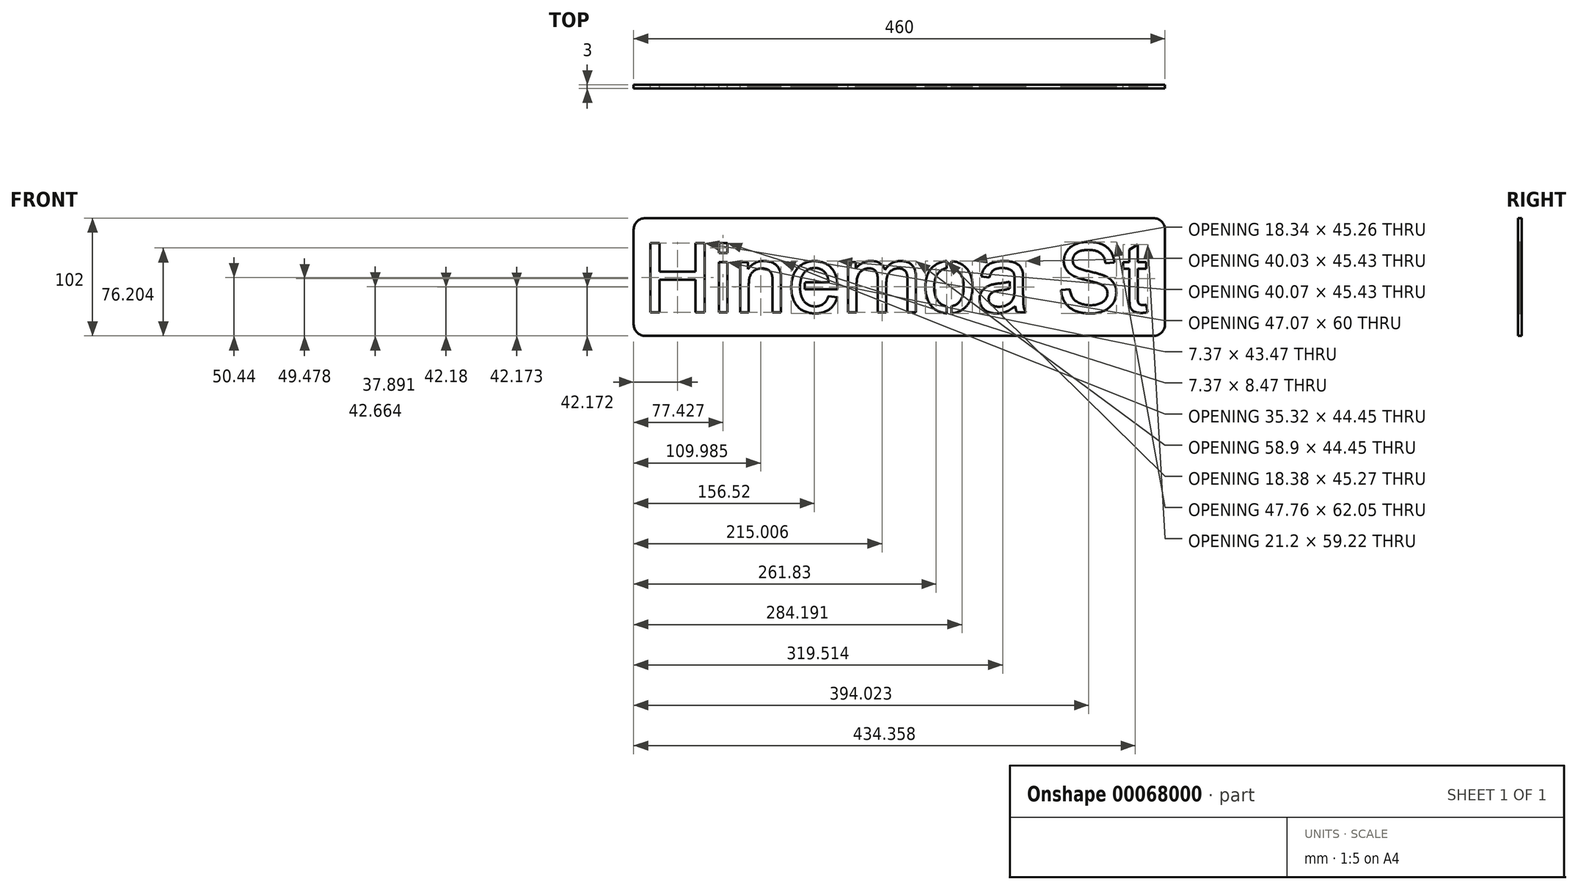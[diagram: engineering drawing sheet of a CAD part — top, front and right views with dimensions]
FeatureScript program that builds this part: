
annotation { "Feature Type Name" : "Feature", "Feature Type Description" : "" }
export const myFeature = defineFeature(function(context is Context, id is Id, definition is map)
    precondition{}
    {
        {
            var Q0;
            Q0=qCreatedBy(makeId("Front.planeOp"),FACE);
            var sketch = newSketch(context, id + "F0", { "sketchPlane" : qUnion([Q0])});
            skLineSegment(sketch, "E0", {"start": v(45.02, -25.34) * mm, "end": v(45.02, -31.45) * mm});
            skLineSegment(sketch, "E1", {"start": v(45.02, -25.34) * mm, "end": v(45.65, -25.22) * mm});
            skLineSegment(sketch, "E2", {"start": v(45.65, -25.22) * mm, "end": v(46.27, -25.08) * mm});
            skLineSegment(sketch, "E3", {"start": v(46.27, -25.08) * mm, "end": v(46.87, -24.9) * mm});
            skLineSegment(sketch, "E4", {"start": v(46.87, -24.9) * mm, "end": v(47.47, -24.69) * mm});
            skLineSegment(sketch, "E5", {"start": v(47.47, -24.69) * mm, "end": v(48.04, -24.44) * mm});
            skLineSegment(sketch, "E6", {"start": v(48.04, -24.44) * mm, "end": v(48.6, -24.16) * mm});
            skLineSegment(sketch, "E7", {"start": v(48.6, -24.16) * mm, "end": v(49.16, -23.85) * mm});
            skLineSegment(sketch, "E8", {"start": v(49.16, -23.85) * mm, "end": v(49.7, -23.51) * mm});
            skLineSegment(sketch, "E9", {"start": v(49.7, -23.51) * mm, "end": v(50.21, -23.14) * mm});
            skLineSegment(sketch, "E10", {"start": v(50.21, -23.14) * mm, "end": v(50.72, -22.73) * mm});
            skLineSegment(sketch, "E11", {"start": v(50.72, -22.73) * mm, "end": v(51.2, -22.29) * mm});
            skLineSegment(sketch, "E12", {"start": v(51.2, -22.29) * mm, "end": v(51.69, -21.82) * mm});
            skLineSegment(sketch, "E13", {"start": v(51.69, -21.82) * mm, "end": v(52.15, -21.31) * mm});
            skLineSegment(sketch, "E14", {"start": v(52.15, -21.31) * mm, "end": v(52.59, -20.77) * mm});
            skLineSegment(sketch, "E15", {"start": v(52.59, -20.77) * mm, "end": v(53, -20.2) * mm});
            skLineSegment(sketch, "E16", {"start": v(53, -20.2) * mm, "end": v(53.39, -19.6) * mm});
            skLineSegment(sketch, "E17", {"start": v(53.39, -19.6) * mm, "end": v(53.74, -18.95) * mm});
            skLineSegment(sketch, "E18", {"start": v(53.74, -18.95) * mm, "end": v(54.07, -18.27) * mm});
            skLineSegment(sketch, "E19", {"start": v(54.07, -18.27) * mm, "end": v(54.37, -17.56) * mm});
            skLineSegment(sketch, "E20", {"start": v(54.37, -17.56) * mm, "end": v(54.64, -16.82) * mm});
            skLineSegment(sketch, "E21", {"start": v(54.64, -16.82) * mm, "end": v(54.88, -16.04) * mm});
            skLineSegment(sketch, "E22", {"start": v(54.88, -16.04) * mm, "end": v(55.1, -15.23) * mm});
            skLineSegment(sketch, "E23", {"start": v(55.1, -15.23) * mm, "end": v(55.28, -14.38) * mm});
            skLineSegment(sketch, "E24", {"start": v(55.28, -14.38) * mm, "end": v(55.43, -13.5) * mm});
            skLineSegment(sketch, "E25", {"start": v(55.43, -13.5) * mm, "end": v(55.56, -12.59) * mm});
            skLineSegment(sketch, "E26", {"start": v(55.56, -12.59) * mm, "end": v(55.66, -11.64) * mm});
            skLineSegment(sketch, "E27", {"start": v(55.66, -11.64) * mm, "end": v(55.73, -10.65) * mm});
            skLineSegment(sketch, "E28", {"start": v(55.73, -10.65) * mm, "end": v(55.78, -9.63) * mm});
            skLineSegment(sketch, "E29", {"start": v(55.78, -9.63) * mm, "end": v(55.8, -8.58) * mm});
            skLineSegment(sketch, "E30", {"start": v(55.8, -8.58) * mm, "end": v(55.78, -7.59) * mm});
            skLineSegment(sketch, "E31", {"start": v(55.78, -7.59) * mm, "end": v(55.73, -6.63) * mm});
            skLineSegment(sketch, "E32", {"start": v(55.73, -6.63) * mm, "end": v(55.66, -5.7) * mm});
            skLineSegment(sketch, "E33", {"start": v(55.66, -5.7) * mm, "end": v(55.56, -4.8) * mm});
            skLineSegment(sketch, "E34", {"start": v(55.56, -4.8) * mm, "end": v(55.43, -3.92) * mm});
            skLineSegment(sketch, "E35", {"start": v(55.43, -3.92) * mm, "end": v(55.28, -3.08) * mm});
            skLineSegment(sketch, "E36", {"start": v(55.28, -3.08) * mm, "end": v(55.09, -2.28) * mm});
            skLineSegment(sketch, "E37", {"start": v(55.09, -2.28) * mm, "end": v(54.87, -1.5) * mm});
            skLineSegment(sketch, "E38", {"start": v(54.87, -1.5) * mm, "end": v(54.63, -0.75) * mm});
            skLineSegment(sketch, "E39", {"start": v(54.63, -0.75) * mm, "end": v(54.36, -0.03) * mm});
            skLineSegment(sketch, "E40", {"start": v(54.36, -0.03) * mm, "end": v(54.06, 0.66) * mm});
            skLineSegment(sketch, "E41", {"start": v(54.06, 0.66) * mm, "end": v(53.73, 1.31) * mm});
            skLineSegment(sketch, "E42", {"start": v(53.73, 1.31) * mm, "end": v(53.37, 1.94) * mm});
            skLineSegment(sketch, "E43", {"start": v(53.37, 1.94) * mm, "end": v(52.99, 2.54) * mm});
            skLineSegment(sketch, "E44", {"start": v(52.99, 2.54) * mm, "end": v(52.57, 3.1) * mm});
            skLineSegment(sketch, "E45", {"start": v(52.57, 3.1) * mm, "end": v(52.13, 3.64) * mm});
            skLineSegment(sketch, "E46", {"start": v(52.13, 3.64) * mm, "end": v(51.66, 4.14) * mm});
            skLineSegment(sketch, "E47", {"start": v(51.66, 4.14) * mm, "end": v(51.18, 4.6) * mm});
            skLineSegment(sketch, "E48", {"start": v(51.18, 4.6) * mm, "end": v(50.7, 5.05) * mm});
            skLineSegment(sketch, "E49", {"start": v(50.7, 5.05) * mm, "end": v(50.18, 5.45) * mm});
            skLineSegment(sketch, "E50", {"start": v(50.18, 5.45) * mm, "end": v(49.66, 5.83) * mm});
            skLineSegment(sketch, "E51", {"start": v(49.66, 5.83) * mm, "end": v(49.13, 6.17) * mm});
            skLineSegment(sketch, "E52", {"start": v(49.13, 6.17) * mm, "end": v(48.58, 6.47) * mm});
            skLineSegment(sketch, "E53", {"start": v(48.58, 6.47) * mm, "end": v(48.02, 6.75) * mm});
            skLineSegment(sketch, "E54", {"start": v(48.02, 6.75) * mm, "end": v(47.44, 7) * mm});
            skLineSegment(sketch, "E55", {"start": v(47.44, 7) * mm, "end": v(46.85, 7.2) * mm});
            skLineSegment(sketch, "E56", {"start": v(46.85, 7.2) * mm, "end": v(46.25, 7.38) * mm});
            skLineSegment(sketch, "E57", {"start": v(46.25, 7.38) * mm, "end": v(45.63, 7.53) * mm});
            skLineSegment(sketch, "E58", {"start": v(45.63, 7.53) * mm, "end": v(45.02, 7.64) * mm});
            skLineSegment(sketch, "E59", {"start": v(45.02, 13.8) * mm, "end": v(45.02, 7.64) * mm});
            skLineSegment(sketch, "E60", {"start": v(45.02, 13.8) * mm, "end": v(45.21, 13.8) * mm});
            skLineSegment(sketch, "E61", {"start": v(45.21, 13.8) * mm, "end": v(46.27, 13.68) * mm});
            skLineSegment(sketch, "E62", {"start": v(46.27, 13.68) * mm, "end": v(47.3, 13.52) * mm});
            skLineSegment(sketch, "E63", {"start": v(47.3, 13.52) * mm, "end": v(48.3, 13.31) * mm});
            skLineSegment(sketch, "E64", {"start": v(48.3, 13.31) * mm, "end": v(49.28, 13.06) * mm});
            skLineSegment(sketch, "E65", {"start": v(49.28, 13.06) * mm, "end": v(50.24, 12.76) * mm});
            skLineSegment(sketch, "E66", {"start": v(50.24, 12.76) * mm, "end": v(51.17, 12.42) * mm});
            skLineSegment(sketch, "E67", {"start": v(51.17, 12.42) * mm, "end": v(52.07, 12.03) * mm});
            skLineSegment(sketch, "E68", {"start": v(52.07, 12.03) * mm, "end": v(52.95, 11.6) * mm});
            skLineSegment(sketch, "E69", {"start": v(52.95, 11.6) * mm, "end": v(53.8, 11.11) * mm});
            skLineSegment(sketch, "E70", {"start": v(53.8, 11.11) * mm, "end": v(54.62, 10.58) * mm});
            skLineSegment(sketch, "E71", {"start": v(54.62, 10.58) * mm, "end": v(55.42, 10.01) * mm});
            skLineSegment(sketch, "E72", {"start": v(55.42, 10.01) * mm, "end": v(56.2, 9.4) * mm});
            skLineSegment(sketch, "E73", {"start": v(56.2, 9.4) * mm, "end": v(56.95, 8.73) * mm});
            skLineSegment(sketch, "E74", {"start": v(56.95, 8.73) * mm, "end": v(57.67, 8.01) * mm});
            skLineSegment(sketch, "E75", {"start": v(57.67, 8.01) * mm, "end": v(58.36, 7.26) * mm});
            skLineSegment(sketch, "E76", {"start": v(58.36, 7.26) * mm, "end": v(59, 6.48) * mm});
            skLineSegment(sketch, "E77", {"start": v(59, 6.48) * mm, "end": v(59.6, 5.65) * mm});
            skLineSegment(sketch, "E78", {"start": v(59.6, 5.65) * mm, "end": v(60.16, 4.8) * mm});
            skLineSegment(sketch, "E79", {"start": v(60.16, 4.8) * mm, "end": v(60.67, 3.9) * mm});
            skLineSegment(sketch, "E80", {"start": v(60.67, 3.9) * mm, "end": v(61.14, 2.98) * mm});
            skLineSegment(sketch, "E81", {"start": v(61.14, 2.98) * mm, "end": v(61.56, 2.02) * mm});
            skLineSegment(sketch, "E82", {"start": v(61.56, 2.02) * mm, "end": v(61.94, 1.02) * mm});
            skLineSegment(sketch, "E83", {"start": v(61.94, 1.02) * mm, "end": v(62.27, -0.01) * mm});
            skLineSegment(sketch, "E84", {"start": v(62.27, -0.01) * mm, "end": v(62.56, -1.08) * mm});
            skLineSegment(sketch, "E85", {"start": v(62.56, -1.08) * mm, "end": v(62.8, -2.18) * mm});
            skLineSegment(sketch, "E86", {"start": v(62.8, -2.18) * mm, "end": v(63, -3.32) * mm});
            skLineSegment(sketch, "E87", {"start": v(63, -3.32) * mm, "end": v(63.16, -4.49) * mm});
            skLineSegment(sketch, "E88", {"start": v(63.16, -4.49) * mm, "end": v(63.27, -5.7) * mm});
            skLineSegment(sketch, "E89", {"start": v(63.27, -5.7) * mm, "end": v(63.34, -6.94) * mm});
            skLineSegment(sketch, "E90", {"start": v(63.34, -6.94) * mm, "end": v(63.36, -8.21) * mm});
            skLineSegment(sketch, "E91", {"start": v(63.36, -8.21) * mm, "end": v(63.35, -9.25) * mm});
            skLineSegment(sketch, "E92", {"start": v(63.35, -9.25) * mm, "end": v(63.32, -10.26) * mm});
            skLineSegment(sketch, "E93", {"start": v(63.32, -10.26) * mm, "end": v(63.27, -11.23) * mm});
            skLineSegment(sketch, "E94", {"start": v(63.27, -11.23) * mm, "end": v(63.2, -12.18) * mm});
            skLineSegment(sketch, "E95", {"start": v(63.2, -12.18) * mm, "end": v(63.12, -13.1) * mm});
            skLineSegment(sketch, "E96", {"start": v(63.12, -13.1) * mm, "end": v(63, -14) * mm});
            skLineSegment(sketch, "E97", {"start": v(63, -14) * mm, "end": v(62.88, -14.87) * mm});
            skLineSegment(sketch, "E98", {"start": v(62.88, -14.87) * mm, "end": v(62.73, -15.7) * mm});
            skLineSegment(sketch, "E99", {"start": v(62.73, -15.7) * mm, "end": v(62.57, -16.52) * mm});
            skLineSegment(sketch, "E100", {"start": v(62.57, -16.52) * mm, "end": v(62.38, -17.3) * mm});
            skLineSegment(sketch, "E101", {"start": v(62.38, -17.3) * mm, "end": v(62.17, -18.06) * mm});
            skLineSegment(sketch, "E102", {"start": v(62.17, -18.06) * mm, "end": v(61.95, -18.78) * mm});
            skLineSegment(sketch, "E103", {"start": v(61.95, -18.78) * mm, "end": v(61.7, -19.48) * mm});
            skLineSegment(sketch, "E104", {"start": v(61.7, -19.48) * mm, "end": v(61.43, -20.15) * mm});
            skLineSegment(sketch, "E105", {"start": v(61.43, -20.15) * mm, "end": v(61.15, -20.8) * mm});
            skLineSegment(sketch, "E106", {"start": v(61.15, -20.8) * mm, "end": v(60.84, -21.41) * mm});
            skLineSegment(sketch, "E107", {"start": v(60.84, -21.41) * mm, "end": v(60.52, -22) * mm});
            skLineSegment(sketch, "E108", {"start": v(60.52, -22) * mm, "end": v(60.18, -22.58) * mm});
            skLineSegment(sketch, "E109", {"start": v(60.18, -22.58) * mm, "end": v(59.82, -23.14) * mm});
            skLineSegment(sketch, "E110", {"start": v(59.82, -23.14) * mm, "end": v(59.44, -23.68) * mm});
            skLineSegment(sketch, "E111", {"start": v(59.44, -23.68) * mm, "end": v(59.05, -24.2) * mm});
            skLineSegment(sketch, "E112", {"start": v(59.05, -24.2) * mm, "end": v(58.63, -24.72) * mm});
            skLineSegment(sketch, "E113", {"start": v(58.63, -24.72) * mm, "end": v(58.2, -25.2) * mm});
            skLineSegment(sketch, "E114", {"start": v(58.2, -25.2) * mm, "end": v(57.75, -25.68) * mm});
            skLineSegment(sketch, "E115", {"start": v(57.75, -25.68) * mm, "end": v(57.29, -26.14) * mm});
            skLineSegment(sketch, "E116", {"start": v(57.29, -26.14) * mm, "end": v(56.8, -26.58) * mm});
            skLineSegment(sketch, "E117", {"start": v(56.8, -26.58) * mm, "end": v(56.3, -27) * mm});
            skLineSegment(sketch, "E118", {"start": v(56.3, -27) * mm, "end": v(55.78, -27.42) * mm});
            skLineSegment(sketch, "E119", {"start": v(55.78, -27.42) * mm, "end": v(55.24, -27.8) * mm});
            skLineSegment(sketch, "E120", {"start": v(55.24, -27.8) * mm, "end": v(54.69, -28.18) * mm});
            skLineSegment(sketch, "E121", {"start": v(54.69, -28.18) * mm, "end": v(54.11, -28.54) * mm});
            skLineSegment(sketch, "E122", {"start": v(54.11, -28.54) * mm, "end": v(53.52, -28.88) * mm});
            skLineSegment(sketch, "E123", {"start": v(53.52, -28.88) * mm, "end": v(52.3, -29.5) * mm});
            skLineSegment(sketch, "E124", {"start": v(52.3, -29.5) * mm, "end": v(51.06, -30.05) * mm});
            skLineSegment(sketch, "E125", {"start": v(51.06, -30.05) * mm, "end": v(49.79, -30.5) * mm});
            skLineSegment(sketch, "E126", {"start": v(49.79, -30.5) * mm, "end": v(48.49, -30.88) * mm});
            skLineSegment(sketch, "E127", {"start": v(48.49, -30.88) * mm, "end": v(47.16, -31.17) * mm});
            skLineSegment(sketch, "E128", {"start": v(47.16, -31.17) * mm, "end": v(45.81, -31.38) * mm});
            skLineSegment(sketch, "E129", {"start": v(45.81, -31.38) * mm, "end": v(45.02, -31.45) * mm});
            skLineSegment(sketch, "E130", {"start": v(-230, -41) * mm, "end": v(-230, 41) * mm});
            skArc(sketch, "E131", {"start": v(-220, -51) * mm, "mid": v(-227.07, -48.07) * mm, "end": v(-230, -41) * mm});
            skLineSegment(sketch, "E132", {"start": v(220, -51) * mm, "end": v(-220, -51) * mm});
            skArc(sketch, "E133", {"start": v(230, -41) * mm, "mid": v(227.07, -48.07) * mm, "end": v(220, -51) * mm});
            skLineSegment(sketch, "E134", {"start": v(230, 41) * mm, "end": v(230, -41) * mm});
            skArc(sketch, "E135", {"start": v(220, 51) * mm, "mid": v(227.07, 48.07) * mm, "end": v(230, 41) * mm});
            skLineSegment(sketch, "E136", {"start": v(-220, 51) * mm, "end": v(220, 51) * mm});
            skArc(sketch, "E137", {"start": v(-230, 41) * mm, "mid": v(-227.07, 48.07) * mm, "end": v(-220, 51) * mm});
            skLineSegment(sketch, "E138", {"start": v(95.75, -10.01) * mm, "end": v(95.75, -4.06) * mm});
            skLineSegment(sketch, "E139", {"start": v(95.75, -10.01) * mm, "end": v(95.47, -10.08) * mm});
            skLineSegment(sketch, "E140", {"start": v(95.47, -10.08) * mm, "end": v(94.73, -10.26) * mm});
            skLineSegment(sketch, "E141", {"start": v(94.73, -10.26) * mm, "end": v(93.97, -10.43) * mm});
            skLineSegment(sketch, "E142", {"start": v(93.97, -10.43) * mm, "end": v(93.17, -10.6) * mm});
            skLineSegment(sketch, "E143", {"start": v(93.17, -10.6) * mm, "end": v(92.34, -10.76) * mm});
            skLineSegment(sketch, "E144", {"start": v(92.34, -10.76) * mm, "end": v(91.47, -10.92) * mm});
            skLineSegment(sketch, "E145", {"start": v(91.47, -10.92) * mm, "end": v(90.58, -11.08) * mm});
            skLineSegment(sketch, "E146", {"start": v(90.58, -11.08) * mm, "end": v(89.66, -11.23) * mm});
            skLineSegment(sketch, "E147", {"start": v(89.66, -11.23) * mm, "end": v(88.7, -11.38) * mm});
            skLineSegment(sketch, "E148", {"start": v(88.7, -11.38) * mm, "end": v(87.71, -11.53) * mm});
            skLineSegment(sketch, "E149", {"start": v(87.71, -11.53) * mm, "end": v(86.62, -11.7) * mm});
            skLineSegment(sketch, "E150", {"start": v(86.62, -11.7) * mm, "end": v(85.6, -11.87) * mm});
            skLineSegment(sketch, "E151", {"start": v(85.6, -11.87) * mm, "end": v(84.68, -12.04) * mm});
            skLineSegment(sketch, "E152", {"start": v(84.68, -12.04) * mm, "end": v(83.84, -12.22) * mm});
            skLineSegment(sketch, "E153", {"start": v(83.84, -12.22) * mm, "end": v(83.07, -12.41) * mm});
            skLineSegment(sketch, "E154", {"start": v(83.07, -12.41) * mm, "end": v(82.4, -12.6) * mm});
            skLineSegment(sketch, "E155", {"start": v(82.4, -12.6) * mm, "end": v(81.8, -12.8) * mm});
            skLineSegment(sketch, "E156", {"start": v(81.8, -12.8) * mm, "end": v(81.29, -13) * mm});
            skLineSegment(sketch, "E157", {"start": v(81.29, -13) * mm, "end": v(80.83, -13.22) * mm});
            skLineSegment(sketch, "E158", {"start": v(80.83, -13.22) * mm, "end": v(80.4, -13.46) * mm});
            skLineSegment(sketch, "E159", {"start": v(80.4, -13.46) * mm, "end": v(80, -13.72) * mm});
            skLineSegment(sketch, "E160", {"start": v(80, -13.72) * mm, "end": v(79.62, -14) * mm});
            skLineSegment(sketch, "E161", {"start": v(79.62, -14) * mm, "end": v(79.27, -14.32) * mm});
            skLineSegment(sketch, "E162", {"start": v(79.27, -14.32) * mm, "end": v(78.95, -14.66) * mm});
            skLineSegment(sketch, "E163", {"start": v(78.95, -14.66) * mm, "end": v(78.65, -15.01) * mm});
            skLineSegment(sketch, "E164", {"start": v(78.65, -15.01) * mm, "end": v(78.38, -15.4) * mm});
            skLineSegment(sketch, "E165", {"start": v(78.38, -15.4) * mm, "end": v(78.14, -15.8) * mm});
            skLineSegment(sketch, "E166", {"start": v(78.14, -15.8) * mm, "end": v(77.93, -16.2) * mm});
            skLineSegment(sketch, "E167", {"start": v(77.93, -16.2) * mm, "end": v(77.76, -16.63) * mm});
            skLineSegment(sketch, "E168", {"start": v(77.76, -16.63) * mm, "end": v(77.61, -17.06) * mm});
            skLineSegment(sketch, "E169", {"start": v(77.61, -17.06) * mm, "end": v(77.5, -17.5) * mm});
            skLineSegment(sketch, "E170", {"start": v(77.5, -17.5) * mm, "end": v(77.42, -17.96) * mm});
            skLineSegment(sketch, "E171", {"start": v(77.42, -17.96) * mm, "end": v(77.38, -18.42) * mm});
            skLineSegment(sketch, "E172", {"start": v(77.38, -18.42) * mm, "end": v(77.36, -18.9) * mm});
            skLineSegment(sketch, "E173", {"start": v(77.36, -18.9) * mm, "end": v(77.4, -19.62) * mm});
            skLineSegment(sketch, "E174", {"start": v(77.4, -19.62) * mm, "end": v(77.5, -20.3) * mm});
            skLineSegment(sketch, "E175", {"start": v(77.5, -20.3) * mm, "end": v(77.67, -20.97) * mm});
            skLineSegment(sketch, "E176", {"start": v(77.67, -20.97) * mm, "end": v(77.92, -21.6) * mm});
            skLineSegment(sketch, "E177", {"start": v(77.92, -21.6) * mm, "end": v(78.23, -22.2) * mm});
            skLineSegment(sketch, "E178", {"start": v(78.23, -22.2) * mm, "end": v(78.61, -22.76) * mm});
            skLineSegment(sketch, "E179", {"start": v(78.61, -22.76) * mm, "end": v(79.07, -23.3) * mm});
            skLineSegment(sketch, "E180", {"start": v(79.07, -23.3) * mm, "end": v(79.59, -23.8) * mm});
            skLineSegment(sketch, "E181", {"start": v(79.59, -23.8) * mm, "end": v(80.18, -24.27) * mm});
            skLineSegment(sketch, "E182", {"start": v(80.18, -24.27) * mm, "end": v(80.83, -24.67) * mm});
            skLineSegment(sketch, "E183", {"start": v(80.83, -24.67) * mm, "end": v(81.55, -25) * mm});
            skLineSegment(sketch, "E184", {"start": v(81.55, -25) * mm, "end": v(82.34, -25.28) * mm});
            skLineSegment(sketch, "E185", {"start": v(82.34, -25.28) * mm, "end": v(83.19, -25.5) * mm});
            skLineSegment(sketch, "E186", {"start": v(83.19, -25.5) * mm, "end": v(84.1, -25.65) * mm});
            skLineSegment(sketch, "E187", {"start": v(84.1, -25.65) * mm, "end": v(85.08, -25.74) * mm});
            skLineSegment(sketch, "E188", {"start": v(85.08, -25.74) * mm, "end": v(86.12, -25.77) * mm});
            skLineSegment(sketch, "E189", {"start": v(86.12, -25.77) * mm, "end": v(87.17, -25.74) * mm});
            skLineSegment(sketch, "E190", {"start": v(87.17, -25.74) * mm, "end": v(88.19, -25.66) * mm});
            skLineSegment(sketch, "E191", {"start": v(88.19, -25.66) * mm, "end": v(89.18, -25.5) * mm});
            skLineSegment(sketch, "E192", {"start": v(89.18, -25.5) * mm, "end": v(90.14, -25.3) * mm});
            skLineSegment(sketch, "E193", {"start": v(90.14, -25.3) * mm, "end": v(91.07, -25.04) * mm});
            skLineSegment(sketch, "E194", {"start": v(91.07, -25.04) * mm, "end": v(91.97, -24.72) * mm});
            skLineSegment(sketch, "E195", {"start": v(91.97, -24.72) * mm, "end": v(92.85, -24.35) * mm});
            skLineSegment(sketch, "E196", {"start": v(92.85, -24.35) * mm, "end": v(93.69, -23.9) * mm});
            skLineSegment(sketch, "E197", {"start": v(93.69, -23.9) * mm, "end": v(94.5, -23.42) * mm});
            skLineSegment(sketch, "E198", {"start": v(94.5, -23.42) * mm, "end": v(95.24, -22.9) * mm});
            skLineSegment(sketch, "E199", {"start": v(95.24, -22.9) * mm, "end": v(95.93, -22.32) * mm});
            skLineSegment(sketch, "E200", {"start": v(95.93, -22.32) * mm, "end": v(96.56, -21.7) * mm});
            skLineSegment(sketch, "E201", {"start": v(96.56, -21.7) * mm, "end": v(97.15, -21.05) * mm});
            skLineSegment(sketch, "E202", {"start": v(97.15, -21.05) * mm, "end": v(97.67, -20.34) * mm});
            skLineSegment(sketch, "E203", {"start": v(97.67, -20.34) * mm, "end": v(98.14, -19.6) * mm});
            skLineSegment(sketch, "E204", {"start": v(98.14, -19.6) * mm, "end": v(98.56, -18.81) * mm});
            skLineSegment(sketch, "E205", {"start": v(98.56, -18.81) * mm, "end": v(98.84, -18.15) * mm});
            skLineSegment(sketch, "E206", {"start": v(98.84, -18.15) * mm, "end": v(99.08, -17.42) * mm});
            skLineSegment(sketch, "E207", {"start": v(99.08, -17.42) * mm, "end": v(99.28, -16.6) * mm});
            skLineSegment(sketch, "E208", {"start": v(99.28, -16.6) * mm, "end": v(99.45, -15.72) * mm});
            skLineSegment(sketch, "E209", {"start": v(99.45, -15.72) * mm, "end": v(99.58, -14.77) * mm});
            skLineSegment(sketch, "E210", {"start": v(99.58, -14.77) * mm, "end": v(99.67, -13.73) * mm});
            skLineSegment(sketch, "E211", {"start": v(99.67, -13.73) * mm, "end": v(99.73, -12.63) * mm});
            skLineSegment(sketch, "E212", {"start": v(99.73, -12.63) * mm, "end": v(99.75, -11.45) * mm});
            skLineSegment(sketch, "E213", {"start": v(99.75, -11.45) * mm, "end": v(99.76, -2.61) * mm});
            skLineSegment(sketch, "E214", {"start": v(99.76, -2.61) * mm, "end": v(99.76, -2.29) * mm});
            skLineSegment(sketch, "E215", {"start": v(99.76, -2.29) * mm, "end": v(99.77, -2) * mm});
            skLineSegment(sketch, "E216", {"start": v(99.77, -2) * mm, "end": v(99.78, -1.74) * mm});
            skLineSegment(sketch, "E217", {"start": v(99.78, -1.74) * mm, "end": v(99.78, -1.51) * mm});
            skLineSegment(sketch, "E218", {"start": v(99.78, -1.51) * mm, "end": v(99.78, -1.32) * mm});
            skLineSegment(sketch, "E219", {"start": v(99.78, -1.32) * mm, "end": v(99.79, -1.17) * mm});
            skLineSegment(sketch, "E220", {"start": v(99.79, -1.17) * mm, "end": v(99.79, -1.05) * mm});
            skLineSegment(sketch, "E221", {"start": v(99.79, -1.05) * mm, "end": v(99.78, -0.5) * mm});
            skLineSegment(sketch, "E222", {"start": v(99.78, -0.5) * mm, "end": v(99.75, 0.03) * mm});
            skLineSegment(sketch, "E223", {"start": v(99.75, 0.03) * mm, "end": v(99.71, 0.54) * mm});
            skLineSegment(sketch, "E224", {"start": v(99.71, 0.54) * mm, "end": v(99.66, 1.03) * mm});
            skLineSegment(sketch, "E225", {"start": v(99.66, 1.03) * mm, "end": v(99.58, 1.5) * mm});
            skLineSegment(sketch, "E226", {"start": v(99.58, 1.5) * mm, "end": v(99.5, 1.95) * mm});
            skLineSegment(sketch, "E227", {"start": v(99.5, 1.95) * mm, "end": v(99.39, 2.38) * mm});
            skLineSegment(sketch, "E228", {"start": v(99.39, 2.38) * mm, "end": v(99.27, 2.79) * mm});
            skLineSegment(sketch, "E229", {"start": v(99.27, 2.79) * mm, "end": v(99.13, 3.17) * mm});
            skLineSegment(sketch, "E230", {"start": v(99.13, 3.17) * mm, "end": v(98.97, 3.54) * mm});
            skLineSegment(sketch, "E231", {"start": v(98.97, 3.54) * mm, "end": v(98.8, 3.88) * mm});
            skLineSegment(sketch, "E232", {"start": v(98.8, 3.88) * mm, "end": v(98.61, 4.2) * mm});
            skLineSegment(sketch, "E233", {"start": v(98.61, 4.2) * mm, "end": v(98.4, 4.5) * mm});
            skLineSegment(sketch, "E234", {"start": v(98.4, 4.5) * mm, "end": v(98.19, 4.8) * mm});
            skLineSegment(sketch, "E235", {"start": v(98.19, 4.8) * mm, "end": v(97.95, 5.05) * mm});
            skLineSegment(sketch, "E236", {"start": v(97.95, 5.05) * mm, "end": v(97.7, 5.3) * mm});
            skLineSegment(sketch, "E237", {"start": v(97.7, 5.3) * mm, "end": v(97.34, 5.6) * mm});
            skLineSegment(sketch, "E238", {"start": v(97.34, 5.6) * mm, "end": v(96.95, 5.88) * mm});
            skLineSegment(sketch, "E239", {"start": v(96.95, 5.88) * mm, "end": v(96.54, 6.14) * mm});
            skLineSegment(sketch, "E240", {"start": v(96.54, 6.14) * mm, "end": v(96.12, 6.38) * mm});
            skLineSegment(sketch, "E241", {"start": v(96.12, 6.38) * mm, "end": v(95.67, 6.6) * mm});
            skLineSegment(sketch, "E242", {"start": v(95.67, 6.6) * mm, "end": v(95.2, 6.81) * mm});
            skLineSegment(sketch, "E243", {"start": v(95.2, 6.81) * mm, "end": v(94.7, 7) * mm});
            skLineSegment(sketch, "E244", {"start": v(94.7, 7) * mm, "end": v(94.2, 7.17) * mm});
            skLineSegment(sketch, "E245", {"start": v(94.2, 7.17) * mm, "end": v(93.66, 7.31) * mm});
            skLineSegment(sketch, "E246", {"start": v(93.66, 7.31) * mm, "end": v(93.1, 7.44) * mm});
            skLineSegment(sketch, "E247", {"start": v(93.1, 7.44) * mm, "end": v(92.52, 7.55) * mm});
            skLineSegment(sketch, "E248", {"start": v(92.52, 7.55) * mm, "end": v(91.92, 7.63) * mm});
            skLineSegment(sketch, "E249", {"start": v(91.92, 7.63) * mm, "end": v(91.3, 7.7) * mm});
            skLineSegment(sketch, "E250", {"start": v(91.3, 7.7) * mm, "end": v(90.66, 7.75) * mm});
            skLineSegment(sketch, "E251", {"start": v(90.66, 7.75) * mm, "end": v(90, 7.78) * mm});
            skLineSegment(sketch, "E252", {"start": v(90, 7.78) * mm, "end": v(89.3, 7.79) * mm});
            skLineSegment(sketch, "E253", {"start": v(89.3, 7.79) * mm, "end": v(88.67, 7.78) * mm});
            skLineSegment(sketch, "E254", {"start": v(88.67, 7.78) * mm, "end": v(88.05, 7.76) * mm});
            skLineSegment(sketch, "E255", {"start": v(88.05, 7.76) * mm, "end": v(87.46, 7.73) * mm});
            skLineSegment(sketch, "E256", {"start": v(87.46, 7.73) * mm, "end": v(86.88, 7.68) * mm});
            skLineSegment(sketch, "E257", {"start": v(86.88, 7.68) * mm, "end": v(86.33, 7.61) * mm});
            skLineSegment(sketch, "E258", {"start": v(86.33, 7.61) * mm, "end": v(85.8, 7.53) * mm});
            skLineSegment(sketch, "E259", {"start": v(85.8, 7.53) * mm, "end": v(85.28, 7.44) * mm});
            skLineSegment(sketch, "E260", {"start": v(85.28, 7.44) * mm, "end": v(84.8, 7.33) * mm});
            skLineSegment(sketch, "E261", {"start": v(84.8, 7.33) * mm, "end": v(84.32, 7.21) * mm});
            skLineSegment(sketch, "E262", {"start": v(84.32, 7.21) * mm, "end": v(83.88, 7.08) * mm});
            skLineSegment(sketch, "E263", {"start": v(83.88, 7.08) * mm, "end": v(83.45, 6.93) * mm});
            skLineSegment(sketch, "E264", {"start": v(83.45, 6.93) * mm, "end": v(83.04, 6.76) * mm});
            skLineSegment(sketch, "E265", {"start": v(83.04, 6.76) * mm, "end": v(82.66, 6.59) * mm});
            skLineSegment(sketch, "E266", {"start": v(82.66, 6.59) * mm, "end": v(82.3, 6.4) * mm});
            skLineSegment(sketch, "E267", {"start": v(82.3, 6.4) * mm, "end": v(81.96, 6.19) * mm});
            skLineSegment(sketch, "E268", {"start": v(81.96, 6.19) * mm, "end": v(81.64, 5.97) * mm});
            skLineSegment(sketch, "E269", {"start": v(81.64, 5.97) * mm, "end": v(81.33, 5.73) * mm});
            skLineSegment(sketch, "E270", {"start": v(81.33, 5.73) * mm, "end": v(81.04, 5.47) * mm});
            skLineSegment(sketch, "E271", {"start": v(81.04, 5.47) * mm, "end": v(80.75, 5.19) * mm});
            skLineSegment(sketch, "E272", {"start": v(80.75, 5.19) * mm, "end": v(80.48, 4.88) * mm});
            skLineSegment(sketch, "E273", {"start": v(80.48, 4.88) * mm, "end": v(80.21, 4.56) * mm});
            skLineSegment(sketch, "E274", {"start": v(80.21, 4.56) * mm, "end": v(79.96, 4.2) * mm});
            skLineSegment(sketch, "E275", {"start": v(79.96, 4.2) * mm, "end": v(79.72, 3.84) * mm});
            skLineSegment(sketch, "E276", {"start": v(79.72, 3.84) * mm, "end": v(79.48, 3.45) * mm});
            skLineSegment(sketch, "E277", {"start": v(79.48, 3.45) * mm, "end": v(79.26, 3.03) * mm});
            skLineSegment(sketch, "E278", {"start": v(79.26, 3.03) * mm, "end": v(79.04, 2.6) * mm});
            skLineSegment(sketch, "E279", {"start": v(79.04, 2.6) * mm, "end": v(78.84, 2.14) * mm});
            skLineSegment(sketch, "E280", {"start": v(78.84, 2.14) * mm, "end": v(78.65, 1.66) * mm});
            skLineSegment(sketch, "E281", {"start": v(78.65, 1.66) * mm, "end": v(78.46, 1.16) * mm});
            skLineSegment(sketch, "E282", {"start": v(78.46, 1.16) * mm, "end": v(78.29, 0.63) * mm});
            skLineSegment(sketch, "E283", {"start": v(78.29, 0.63) * mm, "end": v(78.13, 0.09) * mm});
            skLineSegment(sketch, "E284", {"start": v(78.13, 0.09) * mm, "end": v(77.97, -0.48) * mm});
            skLineSegment(sketch, "E285", {"start": v(77.97, -0.48) * mm, "end": v(70.77, 0.5) * mm});
            skLineSegment(sketch, "E286", {"start": v(70.77, 0.5) * mm, "end": v(71.04, 1.63) * mm});
            skLineSegment(sketch, "E287", {"start": v(71.04, 1.63) * mm, "end": v(71.34, 2.7) * mm});
            skLineSegment(sketch, "E288", {"start": v(71.34, 2.7) * mm, "end": v(71.68, 3.72) * mm});
            skLineSegment(sketch, "E289", {"start": v(71.68, 3.72) * mm, "end": v(72.07, 4.68) * mm});
            skLineSegment(sketch, "E290", {"start": v(72.07, 4.68) * mm, "end": v(72.5, 5.59) * mm});
            skLineSegment(sketch, "E291", {"start": v(72.5, 5.59) * mm, "end": v(72.96, 6.44) * mm});
            skLineSegment(sketch, "E292", {"start": v(72.96, 6.44) * mm, "end": v(73.46, 7.23) * mm});
            skLineSegment(sketch, "E293", {"start": v(73.46, 7.23) * mm, "end": v(74, 7.97) * mm});
            skLineSegment(sketch, "E294", {"start": v(74, 7.97) * mm, "end": v(74.6, 8.66) * mm});
            skLineSegment(sketch, "E295", {"start": v(74.6, 8.66) * mm, "end": v(75.25, 9.31) * mm});
            skLineSegment(sketch, "E296", {"start": v(75.25, 9.31) * mm, "end": v(75.97, 9.92) * mm});
            skLineSegment(sketch, "E297", {"start": v(75.97, 9.92) * mm, "end": v(76.76, 10.5) * mm});
            skLineSegment(sketch, "E298", {"start": v(76.76, 10.5) * mm, "end": v(77.6, 11.02) * mm});
            skLineSegment(sketch, "E299", {"start": v(77.6, 11.02) * mm, "end": v(78.5, 11.5) * mm});
            skLineSegment(sketch, "E300", {"start": v(78.5, 11.5) * mm, "end": v(79.48, 11.95) * mm});
            skLineSegment(sketch, "E301", {"start": v(79.48, 11.95) * mm, "end": v(80.51, 12.35) * mm});
            skLineSegment(sketch, "E302", {"start": v(80.51, 12.35) * mm, "end": v(81.6, 12.71) * mm});
            skLineSegment(sketch, "E303", {"start": v(81.6, 12.71) * mm, "end": v(82.72, 13.02) * mm});
            skLineSegment(sketch, "E304", {"start": v(82.72, 13.02) * mm, "end": v(83.9, 13.29) * mm});
            skLineSegment(sketch, "E305", {"start": v(83.9, 13.29) * mm, "end": v(85.1, 13.5) * mm});
            skLineSegment(sketch, "E306", {"start": v(85.1, 13.5) * mm, "end": v(86.36, 13.67) * mm});
            skLineSegment(sketch, "E307", {"start": v(86.36, 13.67) * mm, "end": v(87.65, 13.8) * mm});
            skLineSegment(sketch, "E308", {"start": v(87.65, 13.8) * mm, "end": v(89, 13.86) * mm});
            skLineSegment(sketch, "E309", {"start": v(89, 13.86) * mm, "end": v(90.37, 13.89) * mm});
            skLineSegment(sketch, "E310", {"start": v(90.37, 13.89) * mm, "end": v(91.73, 13.87) * mm});
            skLineSegment(sketch, "E311", {"start": v(91.73, 13.87) * mm, "end": v(93.03, 13.8) * mm});
            skLineSegment(sketch, "E312", {"start": v(93.03, 13.8) * mm, "end": v(94.26, 13.7) * mm});
            skLineSegment(sketch, "E313", {"start": v(94.26, 13.7) * mm, "end": v(95.42, 13.56) * mm});
            skLineSegment(sketch, "E314", {"start": v(95.42, 13.56) * mm, "end": v(96.52, 13.38) * mm});
            skLineSegment(sketch, "E315", {"start": v(96.52, 13.38) * mm, "end": v(97.55, 13.15) * mm});
            skLineSegment(sketch, "E316", {"start": v(97.55, 13.15) * mm, "end": v(98.52, 12.88) * mm});
            skLineSegment(sketch, "E317", {"start": v(98.52, 12.88) * mm, "end": v(99.42, 12.58) * mm});
            skLineSegment(sketch, "E318", {"start": v(99.42, 12.58) * mm, "end": v(100.26, 12.24) * mm});
            skLineSegment(sketch, "E319", {"start": v(100.26, 12.24) * mm, "end": v(101.04, 11.88) * mm});
            skLineSegment(sketch, "E320", {"start": v(101.04, 11.88) * mm, "end": v(101.77, 11.5) * mm});
            skLineSegment(sketch, "E321", {"start": v(101.77, 11.5) * mm, "end": v(102.44, 11.1) * mm});
            skLineSegment(sketch, "E322", {"start": v(102.44, 11.1) * mm, "end": v(103.05, 10.68) * mm});
            skLineSegment(sketch, "E323", {"start": v(103.05, 10.68) * mm, "end": v(103.6, 10.23) * mm});
            skLineSegment(sketch, "E324", {"start": v(103.6, 10.23) * mm, "end": v(104.1, 9.77) * mm});
            skLineSegment(sketch, "E325", {"start": v(104.1, 9.77) * mm, "end": v(104.54, 9.28) * mm});
            skLineSegment(sketch, "E326", {"start": v(104.54, 9.28) * mm, "end": v(104.93, 8.77) * mm});
            skLineSegment(sketch, "E327", {"start": v(104.93, 8.77) * mm, "end": v(105.3, 8.23) * mm});
            skLineSegment(sketch, "E328", {"start": v(105.3, 8.23) * mm, "end": v(105.62, 7.65) * mm});
            skLineSegment(sketch, "E329", {"start": v(105.62, 7.65) * mm, "end": v(105.93, 7.04) * mm});
            skLineSegment(sketch, "E330", {"start": v(105.93, 7.04) * mm, "end": v(106.2, 6.4) * mm});
            skLineSegment(sketch, "E331", {"start": v(106.2, 6.4) * mm, "end": v(106.44, 5.72) * mm});
            skLineSegment(sketch, "E332", {"start": v(106.44, 5.72) * mm, "end": v(106.65, 5.01) * mm});
            skLineSegment(sketch, "E333", {"start": v(106.65, 5.01) * mm, "end": v(106.83, 4.27) * mm});
            skLineSegment(sketch, "E334", {"start": v(106.83, 4.27) * mm, "end": v(106.91, 3.75) * mm});
            skLineSegment(sketch, "E335", {"start": v(106.91, 3.75) * mm, "end": v(106.99, 3.14) * mm});
            skLineSegment(sketch, "E336", {"start": v(106.99, 3.14) * mm, "end": v(107.05, 2.43) * mm});
            skLineSegment(sketch, "E337", {"start": v(107.05, 2.43) * mm, "end": v(107.1, 1.63) * mm});
            skLineSegment(sketch, "E338", {"start": v(107.1, 1.63) * mm, "end": v(107.14, 0.73) * mm});
            skLineSegment(sketch, "E339", {"start": v(107.14, 0.73) * mm, "end": v(107.17, -0.26) * mm});
            skLineSegment(sketch, "E340", {"start": v(107.17, -0.26) * mm, "end": v(107.19, -1.34) * mm});
            skLineSegment(sketch, "E341", {"start": v(107.19, -1.34) * mm, "end": v(107.2, -2.52) * mm});
            skLineSegment(sketch, "E342", {"start": v(107.2, -2.52) * mm, "end": v(107.2, -12.35) * mm});
            skLineSegment(sketch, "E343", {"start": v(107.2, -12.35) * mm, "end": v(107.2, -13.6) * mm});
            skLineSegment(sketch, "E344", {"start": v(107.2, -13.6) * mm, "end": v(107.2, -14.8) * mm});
            skLineSegment(sketch, "E345", {"start": v(107.2, -14.8) * mm, "end": v(107.21, -15.93) * mm});
            skLineSegment(sketch, "E346", {"start": v(107.21, -15.93) * mm, "end": v(107.22, -17.01) * mm});
            skLineSegment(sketch, "E347", {"start": v(107.22, -17.01) * mm, "end": v(107.24, -18.03) * mm});
            skLineSegment(sketch, "E348", {"start": v(107.24, -18.03) * mm, "end": v(107.26, -18.99) * mm});
            skLineSegment(sketch, "E349", {"start": v(107.26, -18.99) * mm, "end": v(107.29, -19.9) * mm});
            skLineSegment(sketch, "E350", {"start": v(107.29, -19.9) * mm, "end": v(107.31, -20.73) * mm});
            skLineSegment(sketch, "E351", {"start": v(107.31, -20.73) * mm, "end": v(107.34, -21.51) * mm});
            skLineSegment(sketch, "E352", {"start": v(107.34, -21.51) * mm, "end": v(107.38, -22.24) * mm});
            skLineSegment(sketch, "E353", {"start": v(107.38, -22.24) * mm, "end": v(107.42, -22.9) * mm});
            skLineSegment(sketch, "E354", {"start": v(107.42, -22.9) * mm, "end": v(107.46, -23.5) * mm});
            skLineSegment(sketch, "E355", {"start": v(107.46, -23.5) * mm, "end": v(107.5, -24.06) * mm});
            skLineSegment(sketch, "E356", {"start": v(107.5, -24.06) * mm, "end": v(107.56, -24.54) * mm});
            skLineSegment(sketch, "E357", {"start": v(107.56, -24.54) * mm, "end": v(107.6, -24.97) * mm});
            skLineSegment(sketch, "E358", {"start": v(107.6, -24.97) * mm, "end": v(107.67, -25.34) * mm});
            skLineSegment(sketch, "E359", {"start": v(107.67, -25.34) * mm, "end": v(107.8, -26.02) * mm});
            skLineSegment(sketch, "E360", {"start": v(107.8, -26.02) * mm, "end": v(107.96, -26.69) * mm});
            skLineSegment(sketch, "E361", {"start": v(107.96, -26.69) * mm, "end": v(108.15, -27.35) * mm});
            skLineSegment(sketch, "E362", {"start": v(108.15, -27.35) * mm, "end": v(108.37, -28) * mm});
            skLineSegment(sketch, "E363", {"start": v(108.37, -28) * mm, "end": v(108.61, -28.66) * mm});
            skLineSegment(sketch, "E364", {"start": v(108.61, -28.66) * mm, "end": v(108.9, -29.3) * mm});
            skLineSegment(sketch, "E365", {"start": v(108.9, -29.3) * mm, "end": v(109.2, -29.93) * mm});
            skLineSegment(sketch, "E366", {"start": v(109.2, -29.93) * mm, "end": v(109.53, -30.56) * mm});
            skLineSegment(sketch, "E367", {"start": v(109.53, -30.56) * mm, "end": v(101.83, -30.56) * mm});
            skLineSegment(sketch, "E368", {"start": v(101.83, -30.56) * mm, "end": v(101.56, -29.97) * mm});
            skLineSegment(sketch, "E369", {"start": v(101.56, -29.97) * mm, "end": v(101.31, -29.37) * mm});
            skLineSegment(sketch, "E370", {"start": v(101.31, -29.37) * mm, "end": v(101.09, -28.73) * mm});
            skLineSegment(sketch, "E371", {"start": v(101.09, -28.73) * mm, "end": v(100.9, -28.07) * mm});
            skLineSegment(sketch, "E372", {"start": v(100.9, -28.07) * mm, "end": v(100.72, -27.4) * mm});
            skLineSegment(sketch, "E373", {"start": v(100.72, -27.4) * mm, "end": v(100.58, -26.68) * mm});
            skLineSegment(sketch, "E374", {"start": v(100.58, -26.68) * mm, "end": v(100.46, -25.95) * mm});
            skLineSegment(sketch, "E375", {"start": v(100.46, -25.95) * mm, "end": v(100.36, -25.2) * mm});
            skLineSegment(sketch, "E376", {"start": v(100.36, -25.2) * mm, "end": v(99.34, -26.04) * mm});
            skLineSegment(sketch, "E377", {"start": v(99.34, -26.04) * mm, "end": v(98.33, -26.8) * mm});
            skLineSegment(sketch, "E378", {"start": v(98.33, -26.8) * mm, "end": v(97.33, -27.52) * mm});
            skLineSegment(sketch, "E379", {"start": v(97.33, -27.52) * mm, "end": v(96.34, -28.17) * mm});
            skLineSegment(sketch, "E380", {"start": v(96.34, -28.17) * mm, "end": v(95.36, -28.75) * mm});
            skLineSegment(sketch, "E381", {"start": v(95.36, -28.75) * mm, "end": v(94.4, -29.27) * mm});
            skLineSegment(sketch, "E382", {"start": v(94.4, -29.27) * mm, "end": v(93.43, -29.72) * mm});
            skLineSegment(sketch, "E383", {"start": v(93.43, -29.72) * mm, "end": v(92.48, -30.1) * mm});
            skLineSegment(sketch, "E384", {"start": v(92.48, -30.1) * mm, "end": v(91.53, -30.45) * mm});
            skLineSegment(sketch, "E385", {"start": v(91.53, -30.45) * mm, "end": v(90.55, -30.74) * mm});
            skLineSegment(sketch, "E386", {"start": v(90.55, -30.74) * mm, "end": v(89.56, -30.98) * mm});
            skLineSegment(sketch, "E387", {"start": v(89.56, -30.98) * mm, "end": v(88.56, -31.18) * mm});
            skLineSegment(sketch, "E388", {"start": v(88.56, -31.18) * mm, "end": v(87.53, -31.34) * mm});
            skLineSegment(sketch, "E389", {"start": v(87.53, -31.34) * mm, "end": v(86.5, -31.45) * mm});
            skLineSegment(sketch, "E390", {"start": v(86.5, -31.45) * mm, "end": v(85.43, -31.52) * mm});
            skLineSegment(sketch, "E391", {"start": v(85.43, -31.52) * mm, "end": v(84.36, -31.54) * mm});
            skLineSegment(sketch, "E392", {"start": v(84.36, -31.54) * mm, "end": v(83.48, -31.53) * mm});
            skLineSegment(sketch, "E393", {"start": v(83.48, -31.53) * mm, "end": v(82.62, -31.49) * mm});
            skLineSegment(sketch, "E394", {"start": v(82.62, -31.49) * mm, "end": v(81.79, -31.42) * mm});
            skLineSegment(sketch, "E395", {"start": v(81.79, -31.42) * mm, "end": v(80.98, -31.32) * mm});
            skLineSegment(sketch, "E396", {"start": v(80.98, -31.32) * mm, "end": v(80.2, -31.2) * mm});
            skLineSegment(sketch, "E397", {"start": v(80.2, -31.2) * mm, "end": v(79.45, -31.05) * mm});
            skLineSegment(sketch, "E398", {"start": v(79.45, -31.05) * mm, "end": v(78.73, -30.87) * mm});
            skLineSegment(sketch, "E399", {"start": v(78.73, -30.87) * mm, "end": v(78.02, -30.67) * mm});
            skLineSegment(sketch, "E400", {"start": v(78.02, -30.67) * mm, "end": v(77.35, -30.44) * mm});
            skLineSegment(sketch, "E401", {"start": v(77.35, -30.44) * mm, "end": v(76.7, -30.18) * mm});
            skLineSegment(sketch, "E402", {"start": v(76.7, -30.18) * mm, "end": v(76.08, -29.89) * mm});
            skLineSegment(sketch, "E403", {"start": v(76.08, -29.89) * mm, "end": v(75.48, -29.57) * mm});
            skLineSegment(sketch, "E404", {"start": v(75.48, -29.57) * mm, "end": v(74.9, -29.23) * mm});
            skLineSegment(sketch, "E405", {"start": v(74.9, -29.23) * mm, "end": v(74.36, -28.86) * mm});
            skLineSegment(sketch, "E406", {"start": v(74.36, -28.86) * mm, "end": v(73.84, -28.47) * mm});
            skLineSegment(sketch, "E407", {"start": v(73.84, -28.47) * mm, "end": v(73.35, -28.04) * mm});
            skLineSegment(sketch, "E408", {"start": v(73.35, -28.04) * mm, "end": v(72.88, -27.6) * mm});
            skLineSegment(sketch, "E409", {"start": v(72.88, -27.6) * mm, "end": v(72.45, -27.14) * mm});
            skLineSegment(sketch, "E410", {"start": v(72.45, -27.14) * mm, "end": v(72.04, -26.66) * mm});
            skLineSegment(sketch, "E411", {"start": v(72.04, -26.66) * mm, "end": v(71.66, -26.17) * mm});
            skLineSegment(sketch, "E412", {"start": v(71.66, -26.17) * mm, "end": v(71.32, -25.67) * mm});
            skLineSegment(sketch, "E413", {"start": v(71.32, -25.67) * mm, "end": v(71, -25.15) * mm});
            skLineSegment(sketch, "E414", {"start": v(71, -25.15) * mm, "end": v(70.72, -24.6) * mm});
            skLineSegment(sketch, "E415", {"start": v(70.72, -24.6) * mm, "end": v(70.46, -24.06) * mm});
            skLineSegment(sketch, "E416", {"start": v(70.46, -24.06) * mm, "end": v(70.24, -23.5) * mm});
            skLineSegment(sketch, "E417", {"start": v(70.24, -23.5) * mm, "end": v(70.04, -22.9) * mm});
            skLineSegment(sketch, "E418", {"start": v(70.04, -22.9) * mm, "end": v(69.88, -22.31) * mm});
            skLineSegment(sketch, "E419", {"start": v(69.88, -22.31) * mm, "end": v(69.74, -21.7) * mm});
            skLineSegment(sketch, "E420", {"start": v(69.74, -21.7) * mm, "end": v(69.64, -21.07) * mm});
            skLineSegment(sketch, "E421", {"start": v(69.64, -21.07) * mm, "end": v(69.56, -20.43) * mm});
            skLineSegment(sketch, "E422", {"start": v(69.56, -20.43) * mm, "end": v(69.52, -19.77) * mm});
            skLineSegment(sketch, "E423", {"start": v(69.52, -19.77) * mm, "end": v(69.5, -19.1) * mm});
            skLineSegment(sketch, "E424", {"start": v(69.5, -19.1) * mm, "end": v(69.52, -18.31) * mm});
            skLineSegment(sketch, "E425", {"start": v(69.52, -18.31) * mm, "end": v(69.6, -17.54) * mm});
            skLineSegment(sketch, "E426", {"start": v(69.6, -17.54) * mm, "end": v(69.7, -16.78) * mm});
            skLineSegment(sketch, "E427", {"start": v(69.7, -16.78) * mm, "end": v(69.86, -16.05) * mm});
            skLineSegment(sketch, "E428", {"start": v(69.86, -16.05) * mm, "end": v(70.07, -15.33) * mm});
            skLineSegment(sketch, "E429", {"start": v(70.07, -15.33) * mm, "end": v(70.32, -14.62) * mm});
            skLineSegment(sketch, "E430", {"start": v(70.32, -14.62) * mm, "end": v(70.61, -13.94) * mm});
            skLineSegment(sketch, "E431", {"start": v(70.61, -13.94) * mm, "end": v(70.95, -13.27) * mm});
            skLineSegment(sketch, "E432", {"start": v(70.95, -13.27) * mm, "end": v(71.33, -12.62) * mm});
            skLineSegment(sketch, "E433", {"start": v(71.33, -12.62) * mm, "end": v(71.74, -12.01) * mm});
            skLineSegment(sketch, "E434", {"start": v(71.74, -12.01) * mm, "end": v(72.17, -11.43) * mm});
            skLineSegment(sketch, "E435", {"start": v(72.17, -11.43) * mm, "end": v(72.63, -10.89) * mm});
            skLineSegment(sketch, "E436", {"start": v(72.63, -10.89) * mm, "end": v(73.12, -10.38) * mm});
            skLineSegment(sketch, "E437", {"start": v(73.12, -10.38) * mm, "end": v(73.64, -9.9) * mm});
            skLineSegment(sketch, "E438", {"start": v(73.64, -9.9) * mm, "end": v(74.19, -9.45) * mm});
            skLineSegment(sketch, "E439", {"start": v(74.19, -9.45) * mm, "end": v(74.76, -9.03) * mm});
            skLineSegment(sketch, "E440", {"start": v(74.76, -9.03) * mm, "end": v(75.36, -8.65) * mm});
            skLineSegment(sketch, "E441", {"start": v(75.36, -8.65) * mm, "end": v(75.97, -8.28) * mm});
            skLineSegment(sketch, "E442", {"start": v(75.97, -8.28) * mm, "end": v(76.6, -7.94) * mm});
            skLineSegment(sketch, "E443", {"start": v(76.6, -7.94) * mm, "end": v(77.26, -7.63) * mm});
            skLineSegment(sketch, "E444", {"start": v(77.26, -7.63) * mm, "end": v(77.93, -7.34) * mm});
            skLineSegment(sketch, "E445", {"start": v(77.93, -7.34) * mm, "end": v(78.62, -7.08) * mm});
            skLineSegment(sketch, "E446", {"start": v(78.62, -7.08) * mm, "end": v(79.33, -6.83) * mm});
            skLineSegment(sketch, "E447", {"start": v(79.33, -6.83) * mm, "end": v(80.06, -6.62) * mm});
            skLineSegment(sketch, "E448", {"start": v(80.06, -6.62) * mm, "end": v(80.64, -6.47) * mm});
            skLineSegment(sketch, "E449", {"start": v(80.64, -6.47) * mm, "end": v(81.28, -6.33) * mm});
            skLineSegment(sketch, "E450", {"start": v(81.28, -6.33) * mm, "end": v(82, -6.2) * mm});
            skLineSegment(sketch, "E451", {"start": v(82, -6.2) * mm, "end": v(82.78, -6.05) * mm});
            skLineSegment(sketch, "E452", {"start": v(82.78, -6.05) * mm, "end": v(83.64, -5.92) * mm});
            skLineSegment(sketch, "E453", {"start": v(83.64, -5.92) * mm, "end": v(84.56, -5.78) * mm});
            skLineSegment(sketch, "E454", {"start": v(84.56, -5.78) * mm, "end": v(85.55, -5.65) * mm});
            skLineSegment(sketch, "E455", {"start": v(85.55, -5.65) * mm, "end": v(86.6, -5.51) * mm});
            skLineSegment(sketch, "E456", {"start": v(86.6, -5.51) * mm, "end": v(87.7, -5.38) * mm});
            skLineSegment(sketch, "E457", {"start": v(87.7, -5.38) * mm, "end": v(88.77, -5.24) * mm});
            skLineSegment(sketch, "E458", {"start": v(88.77, -5.24) * mm, "end": v(89.79, -5.1) * mm});
            skLineSegment(sketch, "E459", {"start": v(89.79, -5.1) * mm, "end": v(90.78, -4.95) * mm});
            skLineSegment(sketch, "E460", {"start": v(90.78, -4.95) * mm, "end": v(91.73, -4.8) * mm});
            skLineSegment(sketch, "E461", {"start": v(91.73, -4.8) * mm, "end": v(92.64, -4.66) * mm});
            skLineSegment(sketch, "E462", {"start": v(92.64, -4.66) * mm, "end": v(93.51, -4.5) * mm});
            skLineSegment(sketch, "E463", {"start": v(93.51, -4.5) * mm, "end": v(94.35, -4.35) * mm});
            skLineSegment(sketch, "E464", {"start": v(94.35, -4.35) * mm, "end": v(95.16, -4.19) * mm});
            skLineSegment(sketch, "E465", {"start": v(95.16, -4.19) * mm, "end": v(95.75, -4.06) * mm});
            skArc(sketch, "E466", {"start": v(-81.6, -4.65) * mm, "mid": v(-81.94, -7.67) * mm, "end": v(-81.9, -10.71) * mm});
            skLineSegment(sketch, "E467", {"start": v(-81.6, -4.65) * mm, "end": v(-61.22, -4.65) * mm});
            skLineSegment(sketch, "E468", {"start": v(-61.22, -4.65) * mm, "end": v(-61.3, -3.98) * mm});
            skLineSegment(sketch, "E469", {"start": v(-61.3, -3.98) * mm, "end": v(-61.37, -3.32) * mm});
            skLineSegment(sketch, "E470", {"start": v(-61.37, -3.32) * mm, "end": v(-61.47, -2.7) * mm});
            skLineSegment(sketch, "E471", {"start": v(-61.47, -2.7) * mm, "end": v(-61.58, -2.08) * mm});
            skLineSegment(sketch, "E472", {"start": v(-61.58, -2.08) * mm, "end": v(-61.7, -1.5) * mm});
            skLineSegment(sketch, "E473", {"start": v(-61.7, -1.5) * mm, "end": v(-61.84, -0.93) * mm});
            skLineSegment(sketch, "E474", {"start": v(-61.84, -0.93) * mm, "end": v(-62, -0.38) * mm});
            skLineSegment(sketch, "E475", {"start": v(-62, -0.38) * mm, "end": v(-62.16, 0.15) * mm});
            skLineSegment(sketch, "E476", {"start": v(-62.16, 0.15) * mm, "end": v(-62.34, 0.65) * mm});
            skLineSegment(sketch, "E477", {"start": v(-62.34, 0.65) * mm, "end": v(-62.54, 1.13) * mm});
            skLineSegment(sketch, "E478", {"start": v(-62.54, 1.13) * mm, "end": v(-62.75, 1.6) * mm});
            skLineSegment(sketch, "E479", {"start": v(-62.75, 1.6) * mm, "end": v(-62.97, 2.03) * mm});
            skLineSegment(sketch, "E480", {"start": v(-62.97, 2.03) * mm, "end": v(-63.2, 2.45) * mm});
            skLineSegment(sketch, "E481", {"start": v(-63.2, 2.45) * mm, "end": v(-63.46, 2.85) * mm});
            skLineSegment(sketch, "E482", {"start": v(-63.46, 2.85) * mm, "end": v(-63.73, 3.22) * mm});
            skLineSegment(sketch, "E483", {"start": v(-63.73, 3.22) * mm, "end": v(-64, 3.57) * mm});
            skLineSegment(sketch, "E484", {"start": v(-64, 3.57) * mm, "end": v(-64.45, 4.09) * mm});
            skLineSegment(sketch, "E485", {"start": v(-64.45, 4.09) * mm, "end": v(-64.92, 4.57) * mm});
            skLineSegment(sketch, "E486", {"start": v(-64.92, 4.57) * mm, "end": v(-65.4, 5.02) * mm});
            skLineSegment(sketch, "E487", {"start": v(-65.4, 5.02) * mm, "end": v(-65.9, 5.44) * mm});
            skLineSegment(sketch, "E488", {"start": v(-65.9, 5.44) * mm, "end": v(-66.4, 5.82) * mm});
            skLineSegment(sketch, "E489", {"start": v(-66.4, 5.82) * mm, "end": v(-66.94, 6.17) * mm});
            skLineSegment(sketch, "E490", {"start": v(-66.94, 6.17) * mm, "end": v(-67.48, 6.48) * mm});
            skLineSegment(sketch, "E491", {"start": v(-67.48, 6.48) * mm, "end": v(-68.05, 6.77) * mm});
            skLineSegment(sketch, "E492", {"start": v(-68.05, 6.77) * mm, "end": v(-68.63, 7.02) * mm});
            skLineSegment(sketch, "E493", {"start": v(-68.63, 7.02) * mm, "end": v(-69.22, 7.23) * mm});
            skLineSegment(sketch, "E494", {"start": v(-69.22, 7.23) * mm, "end": v(-69.83, 7.41) * mm});
            skLineSegment(sketch, "E495", {"start": v(-69.83, 7.41) * mm, "end": v(-70.46, 7.56) * mm});
            skLineSegment(sketch, "E496", {"start": v(-70.46, 7.56) * mm, "end": v(-71.1, 7.68) * mm});
            skLineSegment(sketch, "E497", {"start": v(-71.1, 7.68) * mm, "end": v(-71.76, 7.76) * mm});
            skLineSegment(sketch, "E498", {"start": v(-71.76, 7.76) * mm, "end": v(-72.44, 7.81) * mm});
            skLineSegment(sketch, "E499", {"start": v(-72.44, 7.81) * mm, "end": v(-73.13, 7.83) * mm});
            skLineSegment(sketch, "E500", {"start": v(-73.13, 7.83) * mm, "end": v(-73.76, 7.82) * mm});
            skLineSegment(sketch, "E501", {"start": v(-73.76, 7.82) * mm, "end": v(-74.38, 7.78) * mm});
            skLineSegment(sketch, "E502", {"start": v(-74.38, 7.78) * mm, "end": v(-74.98, 7.71) * mm});
            skLineSegment(sketch, "E503", {"start": v(-74.98, 7.71) * mm, "end": v(-75.57, 7.62) * mm});
            skLineSegment(sketch, "E504", {"start": v(-75.57, 7.62) * mm, "end": v(-76.15, 7.5) * mm});
            skLineSegment(sketch, "E505", {"start": v(-76.15, 7.5) * mm, "end": v(-76.71, 7.35) * mm});
            skLineSegment(sketch, "E506", {"start": v(-76.71, 7.35) * mm, "end": v(-77.26, 7.18) * mm});
            skLineSegment(sketch, "E507", {"start": v(-77.26, 7.18) * mm, "end": v(-77.8, 6.98) * mm});
            skLineSegment(sketch, "E508", {"start": v(-77.8, 6.98) * mm, "end": v(-78.33, 6.76) * mm});
            skLineSegment(sketch, "E509", {"start": v(-78.33, 6.76) * mm, "end": v(-78.84, 6.5) * mm});
            skLineSegment(sketch, "E510", {"start": v(-78.84, 6.5) * mm, "end": v(-79.35, 6.22) * mm});
            skLineSegment(sketch, "E511", {"start": v(-79.35, 6.22) * mm, "end": v(-79.84, 5.92) * mm});
            skLineSegment(sketch, "E512", {"start": v(-79.84, 5.92) * mm, "end": v(-80.31, 5.59) * mm});
            skLineSegment(sketch, "E513", {"start": v(-80.31, 5.59) * mm, "end": v(-80.78, 5.23) * mm});
            skLineSegment(sketch, "E514", {"start": v(-80.78, 5.23) * mm, "end": v(-81.23, 4.84) * mm});
            skLineSegment(sketch, "E515", {"start": v(-81.23, 4.84) * mm, "end": v(-81.67, 4.43) * mm});
            skLineSegment(sketch, "E516", {"start": v(-81.67, 4.43) * mm, "end": v(-82.09, 4) * mm});
            skLineSegment(sketch, "E517", {"start": v(-82.09, 4) * mm, "end": v(-82.48, 3.55) * mm});
            skLineSegment(sketch, "E518", {"start": v(-82.48, 3.55) * mm, "end": v(-82.85, 3.08) * mm});
            skLineSegment(sketch, "E519", {"start": v(-82.85, 3.08) * mm, "end": v(-83.2, 2.6) * mm});
            skLineSegment(sketch, "E520", {"start": v(-83.2, 2.6) * mm, "end": v(-83.53, 2.09) * mm});
            skLineSegment(sketch, "E521", {"start": v(-83.53, 2.09) * mm, "end": v(-83.82, 1.56) * mm});
            skLineSegment(sketch, "E522", {"start": v(-83.82, 1.56) * mm, "end": v(-84.1, 1.02) * mm});
            skLineSegment(sketch, "E523", {"start": v(-84.1, 1.02) * mm, "end": v(-84.35, 0.46) * mm});
            skLineSegment(sketch, "E524", {"start": v(-84.35, 0.46) * mm, "end": v(-84.58, -0.11) * mm});
            skLineSegment(sketch, "E525", {"start": v(-84.58, -0.11) * mm, "end": v(-84.96, -1.32) * mm});
            skArc(sketch, "E526", {"start": v(-84.96, -1.32) * mm, "mid": v(-85.82, -5.98) * mm, "end": v(-85.9, -10.71) * mm});
            skLineSegment(sketch, "E527", {"start": v(-85.9, -10.71) * mm, "end": v(-85.88, -11.01) * mm});
            skArc(sketch, "E528", {"start": v(-85.88, -11.01) * mm, "mid": v(-85.6, -13.33) * mm, "end": v(-85.14, -15.6) * mm});
            skLineSegment(sketch, "E529", {"start": v(-85.14, -15.6) * mm, "end": v(-84.68, -17.03) * mm});
            skLineSegment(sketch, "E530", {"start": v(-84.68, -17.03) * mm, "end": v(-84.42, -17.7) * mm});
            skLineSegment(sketch, "E531", {"start": v(-84.42, -17.7) * mm, "end": v(-84.13, -18.35) * mm});
            skLineSegment(sketch, "E532", {"start": v(-84.13, -18.35) * mm, "end": v(-83.81, -18.97) * mm});
            skLineSegment(sketch, "E533", {"start": v(-83.81, -18.97) * mm, "end": v(-83.47, -19.57) * mm});
            skLineSegment(sketch, "E534", {"start": v(-83.47, -19.57) * mm, "end": v(-83.1, -20.13) * mm});
            skLineSegment(sketch, "E535", {"start": v(-83.1, -20.13) * mm, "end": v(-82.7, -20.67) * mm});
            skLineSegment(sketch, "E536", {"start": v(-82.7, -20.67) * mm, "end": v(-82.3, -21.19) * mm});
            skLineSegment(sketch, "E537", {"start": v(-82.3, -21.19) * mm, "end": v(-81.85, -21.68) * mm});
            skLineSegment(sketch, "E538", {"start": v(-81.85, -21.68) * mm, "end": v(-81.39, -22.14) * mm});
            skLineSegment(sketch, "E539", {"start": v(-81.39, -22.14) * mm, "end": v(-80.91, -22.57) * mm});
            skLineSegment(sketch, "E540", {"start": v(-80.91, -22.57) * mm, "end": v(-80.42, -22.97) * mm});
            skLineSegment(sketch, "E541", {"start": v(-80.42, -22.97) * mm, "end": v(-79.92, -23.34) * mm});
            skLineSegment(sketch, "E542", {"start": v(-79.92, -23.34) * mm, "end": v(-79.4, -23.69) * mm});
            skLineSegment(sketch, "E543", {"start": v(-79.4, -23.69) * mm, "end": v(-78.86, -24) * mm});
            skLineSegment(sketch, "E544", {"start": v(-78.86, -24) * mm, "end": v(-78.32, -24.28) * mm});
            skLineSegment(sketch, "E545", {"start": v(-78.32, -24.28) * mm, "end": v(-77.76, -24.53) * mm});
            skLineSegment(sketch, "E546", {"start": v(-77.76, -24.53) * mm, "end": v(-77.18, -24.76) * mm});
            skLineSegment(sketch, "E547", {"start": v(-77.18, -24.76) * mm, "end": v(-76.6, -24.95) * mm});
            skLineSegment(sketch, "E548", {"start": v(-76.6, -24.95) * mm, "end": v(-75.99, -25.11) * mm});
            skLineSegment(sketch, "E549", {"start": v(-75.99, -25.11) * mm, "end": v(-75.37, -25.25) * mm});
            skLineSegment(sketch, "E550", {"start": v(-75.37, -25.25) * mm, "end": v(-74.74, -25.35) * mm});
            skLineSegment(sketch, "E551", {"start": v(-74.74, -25.35) * mm, "end": v(-74.1, -25.43) * mm});
            skLineSegment(sketch, "E552", {"start": v(-74.1, -25.43) * mm, "end": v(-73.44, -25.47) * mm});
            skLineSegment(sketch, "E553", {"start": v(-73.44, -25.47) * mm, "end": v(-72.76, -25.48) * mm});
            skLineSegment(sketch, "E554", {"start": v(-72.76, -25.48) * mm, "end": v(-71.77, -25.45) * mm});
            skLineSegment(sketch, "E555", {"start": v(-71.77, -25.45) * mm, "end": v(-70.81, -25.35) * mm});
            skLineSegment(sketch, "E556", {"start": v(-70.81, -25.35) * mm, "end": v(-69.9, -25.19) * mm});
            skLineSegment(sketch, "E557", {"start": v(-69.9, -25.19) * mm, "end": v(-69, -24.95) * mm});
            skLineSegment(sketch, "E558", {"start": v(-69, -24.95) * mm, "end": v(-68.16, -24.65) * mm});
            skLineSegment(sketch, "E559", {"start": v(-68.16, -24.65) * mm, "end": v(-67.35, -24.29) * mm});
            skLineSegment(sketch, "E560", {"start": v(-67.35, -24.29) * mm, "end": v(-66.58, -23.86) * mm});
            skLineSegment(sketch, "E561", {"start": v(-66.58, -23.86) * mm, "end": v(-65.85, -23.36) * mm});
            skLineSegment(sketch, "E562", {"start": v(-65.85, -23.36) * mm, "end": v(-65.15, -22.78) * mm});
            skLineSegment(sketch, "E563", {"start": v(-65.15, -22.78) * mm, "end": v(-64.49, -22.13) * mm});
            skLineSegment(sketch, "E564", {"start": v(-64.49, -22.13) * mm, "end": v(-63.87, -21.4) * mm});
            skLineSegment(sketch, "E565", {"start": v(-63.87, -21.4) * mm, "end": v(-63.28, -20.6) * mm});
            skLineSegment(sketch, "E566", {"start": v(-63.28, -20.6) * mm, "end": v(-62.73, -19.7) * mm});
            skLineSegment(sketch, "E567", {"start": v(-62.73, -19.7) * mm, "end": v(-62.22, -18.74) * mm});
            skLineSegment(sketch, "E568", {"start": v(-62.22, -18.74) * mm, "end": v(-61.74, -17.69) * mm});
            skLineSegment(sketch, "E569", {"start": v(-61.74, -17.69) * mm, "end": v(-61.3, -16.56) * mm});
            skLineSegment(sketch, "E570", {"start": v(-61.3, -16.56) * mm, "end": v(-53.7, -17.5) * mm});
            skLineSegment(sketch, "E571", {"start": v(-53.7, -17.5) * mm, "end": v(-53.93, -18.33) * mm});
            skLineSegment(sketch, "E572", {"start": v(-53.93, -18.33) * mm, "end": v(-54.19, -19.13) * mm});
            skLineSegment(sketch, "E573", {"start": v(-54.19, -19.13) * mm, "end": v(-54.47, -19.9) * mm});
            skLineSegment(sketch, "E574", {"start": v(-54.47, -19.9) * mm, "end": v(-54.78, -20.65) * mm});
            skLineSegment(sketch, "E575", {"start": v(-54.78, -20.65) * mm, "end": v(-55.12, -21.38) * mm});
            skLineSegment(sketch, "E576", {"start": v(-55.12, -21.38) * mm, "end": v(-55.47, -22.09) * mm});
            skLineSegment(sketch, "E577", {"start": v(-55.47, -22.09) * mm, "end": v(-55.85, -22.77) * mm});
            skLineSegment(sketch, "E578", {"start": v(-55.85, -22.77) * mm, "end": v(-56.26, -23.43) * mm});
            skLineSegment(sketch, "E579", {"start": v(-56.26, -23.43) * mm, "end": v(-56.69, -24.06) * mm});
            skLineSegment(sketch, "E580", {"start": v(-56.69, -24.06) * mm, "end": v(-57.14, -24.68) * mm});
            skLineSegment(sketch, "E581", {"start": v(-57.14, -24.68) * mm, "end": v(-57.62, -25.26) * mm});
            skLineSegment(sketch, "E582", {"start": v(-57.62, -25.26) * mm, "end": v(-58.12, -25.83) * mm});
            skLineSegment(sketch, "E583", {"start": v(-58.12, -25.83) * mm, "end": v(-58.64, -26.37) * mm});
            skLineSegment(sketch, "E584", {"start": v(-58.64, -26.37) * mm, "end": v(-59.2, -26.9) * mm});
            skLineSegment(sketch, "E585", {"start": v(-59.2, -26.9) * mm, "end": v(-59.77, -27.39) * mm});
            skLineSegment(sketch, "E586", {"start": v(-59.77, -27.39) * mm, "end": v(-60.36, -27.86) * mm});
            skLineSegment(sketch, "E587", {"start": v(-60.36, -27.86) * mm, "end": v(-60.98, -28.3) * mm});
            skLineSegment(sketch, "E588", {"start": v(-60.98, -28.3) * mm, "end": v(-61.62, -28.72) * mm});
            skLineSegment(sketch, "E589", {"start": v(-61.62, -28.72) * mm, "end": v(-62.28, -29.11) * mm});
            skLineSegment(sketch, "E590", {"start": v(-62.28, -29.11) * mm, "end": v(-62.97, -29.47) * mm});
            skLineSegment(sketch, "E591", {"start": v(-62.97, -29.47) * mm, "end": v(-63.67, -29.8) * mm});
            skLineSegment(sketch, "E592", {"start": v(-63.67, -29.8) * mm, "end": v(-64.4, -30.1) * mm});
            skLineSegment(sketch, "E593", {"start": v(-64.4, -30.1) * mm, "end": v(-65.14, -30.38) * mm});
            skLineSegment(sketch, "E594", {"start": v(-65.14, -30.38) * mm, "end": v(-65.9, -30.62) * mm});
            skLineSegment(sketch, "E595", {"start": v(-65.9, -30.62) * mm, "end": v(-66.7, -30.84) * mm});
            skLineSegment(sketch, "E596", {"start": v(-66.7, -30.84) * mm, "end": v(-67.5, -31.02) * mm});
            skLineSegment(sketch, "E597", {"start": v(-67.5, -31.02) * mm, "end": v(-68.34, -31.18) * mm});
            skLineSegment(sketch, "E598", {"start": v(-68.34, -31.18) * mm, "end": v(-69.19, -31.31) * mm});
            skLineSegment(sketch, "E599", {"start": v(-69.19, -31.31) * mm, "end": v(-70.06, -31.41) * mm});
            skLineSegment(sketch, "E600", {"start": v(-70.06, -31.41) * mm, "end": v(-70.95, -31.48) * mm});
            skLineSegment(sketch, "E601", {"start": v(-70.95, -31.48) * mm, "end": v(-71.87, -31.53) * mm});
            skLineSegment(sketch, "E602", {"start": v(-71.87, -31.53) * mm, "end": v(-72.8, -31.54) * mm});
            skLineSegment(sketch, "E603", {"start": v(-72.8, -31.54) * mm, "end": v(-73.98, -31.52) * mm});
            skLineSegment(sketch, "E604", {"start": v(-73.98, -31.52) * mm, "end": v(-75.13, -31.45) * mm});
            skLineSegment(sketch, "E605", {"start": v(-75.13, -31.45) * mm, "end": v(-76.24, -31.34) * mm});
            skLineSegment(sketch, "E606", {"start": v(-76.24, -31.34) * mm, "end": v(-77.33, -31.18) * mm});
            skLineSegment(sketch, "E607", {"start": v(-77.33, -31.18) * mm, "end": v(-78.38, -30.97) * mm});
            skLineSegment(sketch, "E608", {"start": v(-78.38, -30.97) * mm, "end": v(-79.4, -30.72) * mm});
            skLineSegment(sketch, "E609", {"start": v(-79.4, -30.72) * mm, "end": v(-80.4, -30.42) * mm});
            skLineSegment(sketch, "E610", {"start": v(-80.4, -30.42) * mm, "end": v(-81.35, -30.07) * mm});
            skLineSegment(sketch, "E611", {"start": v(-81.35, -30.07) * mm, "end": v(-82.28, -29.68) * mm});
            skLineSegment(sketch, "E612", {"start": v(-82.28, -29.68) * mm, "end": v(-83.18, -29.25) * mm});
            skLineSegment(sketch, "E613", {"start": v(-83.18, -29.25) * mm, "end": v(-84.05, -28.77) * mm});
            skLineSegment(sketch, "E614", {"start": v(-84.05, -28.77) * mm, "end": v(-84.89, -28.24) * mm});
            skLineSegment(sketch, "E615", {"start": v(-84.89, -28.24) * mm, "end": v(-85.7, -27.67) * mm});
            skLineSegment(sketch, "E616", {"start": v(-85.7, -27.67) * mm, "end": v(-86.47, -27.05) * mm});
            skLineSegment(sketch, "E617", {"start": v(-86.47, -27.05) * mm, "end": v(-87.21, -26.38) * mm});
            skLineSegment(sketch, "E618", {"start": v(-87.21, -26.38) * mm, "end": v(-87.93, -25.67) * mm});
            skLineSegment(sketch, "E619", {"start": v(-87.93, -25.67) * mm, "end": v(-88.6, -24.92) * mm});
            skLineSegment(sketch, "E620", {"start": v(-88.6, -24.92) * mm, "end": v(-89.24, -24.13) * mm});
            skLineSegment(sketch, "E621", {"start": v(-89.24, -24.13) * mm, "end": v(-89.83, -23.3) * mm});
            skLineSegment(sketch, "E622", {"start": v(-89.83, -23.3) * mm, "end": v(-90.37, -22.44) * mm});
            skLineSegment(sketch, "E623", {"start": v(-90.37, -22.44) * mm, "end": v(-90.87, -21.54) * mm});
            skLineSegment(sketch, "E624", {"start": v(-90.87, -21.54) * mm, "end": v(-91.33, -20.6) * mm});
            skLineSegment(sketch, "E625", {"start": v(-91.33, -20.6) * mm, "end": v(-91.75, -19.63) * mm});
            skLineSegment(sketch, "E626", {"start": v(-91.75, -19.63) * mm, "end": v(-92.12, -18.61) * mm});
            skLineSegment(sketch, "E627", {"start": v(-92.12, -18.61) * mm, "end": v(-92.44, -17.57) * mm});
            skLineSegment(sketch, "E628", {"start": v(-92.44, -17.57) * mm, "end": v(-92.73, -16.48) * mm});
            skLineSegment(sketch, "E629", {"start": v(-92.73, -16.48) * mm, "end": v(-92.97, -15.36) * mm});
            skLineSegment(sketch, "E630", {"start": v(-92.97, -15.36) * mm, "end": v(-93.16, -14.2) * mm});
            skLineSegment(sketch, "E631", {"start": v(-93.16, -14.2) * mm, "end": v(-93.32, -13) * mm});
            skLineSegment(sketch, "E632", {"start": v(-93.32, -13) * mm, "end": v(-93.43, -11.77) * mm});
            skLineSegment(sketch, "E633", {"start": v(-93.43, -11.77) * mm, "end": v(-93.5, -10.5) * mm});
            skLineSegment(sketch, "E634", {"start": v(-93.5, -10.5) * mm, "end": v(-93.51, -9.2) * mm});
            skLineSegment(sketch, "E635", {"start": v(-93.51, -9.2) * mm, "end": v(-93.5, -7.84) * mm});
            skLineSegment(sketch, "E636", {"start": v(-93.5, -7.84) * mm, "end": v(-93.43, -6.53) * mm});
            skLineSegment(sketch, "E637", {"start": v(-93.43, -6.53) * mm, "end": v(-93.32, -5.26) * mm});
            skLineSegment(sketch, "E638", {"start": v(-93.32, -5.26) * mm, "end": v(-93.16, -4.02) * mm});
            skLineSegment(sketch, "E639", {"start": v(-93.16, -4.02) * mm, "end": v(-92.96, -2.82) * mm});
            skLineSegment(sketch, "E640", {"start": v(-92.96, -2.82) * mm, "end": v(-92.72, -1.66) * mm});
            skLineSegment(sketch, "E641", {"start": v(-92.72, -1.66) * mm, "end": v(-92.43, -0.54) * mm});
            skLineSegment(sketch, "E642", {"start": v(-92.43, -0.54) * mm, "end": v(-92.1, 0.55) * mm});
            skLineSegment(sketch, "E643", {"start": v(-92.1, 0.55) * mm, "end": v(-91.73, 1.6) * mm});
            skLineSegment(sketch, "E644", {"start": v(-91.73, 1.6) * mm, "end": v(-91.3, 2.6) * mm});
            skLineSegment(sketch, "E645", {"start": v(-91.3, 2.6) * mm, "end": v(-90.84, 3.56) * mm});
            skLineSegment(sketch, "E646", {"start": v(-90.84, 3.56) * mm, "end": v(-90.34, 4.5) * mm});
            skLineSegment(sketch, "E647", {"start": v(-90.34, 4.5) * mm, "end": v(-89.79, 5.39) * mm});
            skLineSegment(sketch, "E648", {"start": v(-89.79, 5.39) * mm, "end": v(-89.19, 6.24) * mm});
            skLineSegment(sketch, "E649", {"start": v(-89.19, 6.24) * mm, "end": v(-88.55, 7.05) * mm});
            skLineSegment(sketch, "E650", {"start": v(-88.55, 7.05) * mm, "end": v(-87.87, 7.83) * mm});
            skLineSegment(sketch, "E651", {"start": v(-87.87, 7.83) * mm, "end": v(-87.15, 8.56) * mm});
            skLineSegment(sketch, "E652", {"start": v(-87.15, 8.56) * mm, "end": v(-86.4, 9.25) * mm});
            skLineSegment(sketch, "E653", {"start": v(-86.4, 9.25) * mm, "end": v(-85.63, 9.89) * mm});
            skLineSegment(sketch, "E654", {"start": v(-85.63, 9.89) * mm, "end": v(-84.83, 10.48) * mm});
            skLineSegment(sketch, "E655", {"start": v(-84.83, 10.48) * mm, "end": v(-84, 11.02) * mm});
            skLineSegment(sketch, "E656", {"start": v(-84, 11.02) * mm, "end": v(-83.16, 11.52) * mm});
            skLineSegment(sketch, "E657", {"start": v(-83.16, 11.52) * mm, "end": v(-82.28, 11.97) * mm});
            skLineSegment(sketch, "E658", {"start": v(-82.28, 11.97) * mm, "end": v(-81.38, 12.37) * mm});
            skLineSegment(sketch, "E659", {"start": v(-81.38, 12.37) * mm, "end": v(-80.45, 12.73) * mm});
            skLineSegment(sketch, "E660", {"start": v(-80.45, 12.73) * mm, "end": v(-79.5, 13.04) * mm});
            skLineSegment(sketch, "E661", {"start": v(-79.5, 13.04) * mm, "end": v(-78.51, 13.3) * mm});
            skLineSegment(sketch, "E662", {"start": v(-78.51, 13.3) * mm, "end": v(-77.5, 13.5) * mm});
            skLineSegment(sketch, "E663", {"start": v(-77.5, 13.5) * mm, "end": v(-76.47, 13.67) * mm});
            skLineSegment(sketch, "E664", {"start": v(-76.47, 13.67) * mm, "end": v(-75.41, 13.8) * mm});
            skLineSegment(sketch, "E665", {"start": v(-75.41, 13.8) * mm, "end": v(-74.33, 13.86) * mm});
            skLineSegment(sketch, "E666", {"start": v(-74.33, 13.86) * mm, "end": v(-73.21, 13.89) * mm});
            skLineSegment(sketch, "E667", {"start": v(-73.21, 13.89) * mm, "end": v(-72.14, 13.86) * mm});
            skLineSegment(sketch, "E668", {"start": v(-72.14, 13.86) * mm, "end": v(-71.08, 13.8) * mm});
            skLineSegment(sketch, "E669", {"start": v(-71.08, 13.8) * mm, "end": v(-70.06, 13.68) * mm});
            skLineSegment(sketch, "E670", {"start": v(-70.06, 13.68) * mm, "end": v(-69.05, 13.52) * mm});
            skLineSegment(sketch, "E671", {"start": v(-69.05, 13.52) * mm, "end": v(-68.08, 13.3) * mm});
            skLineSegment(sketch, "E672", {"start": v(-68.08, 13.3) * mm, "end": v(-67.12, 13.05) * mm});
            skLineSegment(sketch, "E673", {"start": v(-67.12, 13.05) * mm, "end": v(-66.2, 12.75) * mm});
            skLineSegment(sketch, "E674", {"start": v(-66.2, 12.75) * mm, "end": v(-65.3, 12.4) * mm});
            skLineSegment(sketch, "E675", {"start": v(-65.3, 12.4) * mm, "end": v(-64.42, 12) * mm});
            skLineSegment(sketch, "E676", {"start": v(-64.42, 12) * mm, "end": v(-63.56, 11.57) * mm});
            skLineSegment(sketch, "E677", {"start": v(-63.56, 11.57) * mm, "end": v(-62.74, 11.08) * mm});
            skLineSegment(sketch, "E678", {"start": v(-62.74, 11.08) * mm, "end": v(-61.93, 10.55) * mm});
            skLineSegment(sketch, "E679", {"start": v(-61.93, 10.55) * mm, "end": v(-61.16, 9.97) * mm});
            skLineSegment(sketch, "E680", {"start": v(-61.16, 9.97) * mm, "end": v(-60.4, 9.34) * mm});
            skLineSegment(sketch, "E681", {"start": v(-60.4, 9.34) * mm, "end": v(-59.67, 8.67) * mm});
            skLineSegment(sketch, "E682", {"start": v(-59.67, 8.67) * mm, "end": v(-58.97, 7.95) * mm});
            skLineSegment(sketch, "E683", {"start": v(-58.97, 7.95) * mm, "end": v(-58.3, 7.2) * mm});
            skLineSegment(sketch, "E684", {"start": v(-58.3, 7.2) * mm, "end": v(-57.68, 6.4) * mm});
            skLineSegment(sketch, "E685", {"start": v(-57.68, 6.4) * mm, "end": v(-57.1, 5.56) * mm});
            skLineSegment(sketch, "E686", {"start": v(-57.1, 5.56) * mm, "end": v(-56.55, 4.68) * mm});
            skLineSegment(sketch, "E687", {"start": v(-56.55, 4.68) * mm, "end": v(-56.06, 3.77) * mm});
            skLineSegment(sketch, "E688", {"start": v(-56.06, 3.77) * mm, "end": v(-55.6, 2.82) * mm});
            skLineSegment(sketch, "E689", {"start": v(-55.6, 2.82) * mm, "end": v(-55.2, 1.84) * mm});
            skLineSegment(sketch, "E690", {"start": v(-55.2, 1.84) * mm, "end": v(-54.83, 0.81) * mm});
            skLineSegment(sketch, "E691", {"start": v(-54.83, 0.81) * mm, "end": v(-54.5, -0.25) * mm});
            skLineSegment(sketch, "E692", {"start": v(-54.5, -0.25) * mm, "end": v(-54.22, -1.35) * mm});
            skLineSegment(sketch, "E693", {"start": v(-54.22, -1.35) * mm, "end": v(-53.99, -2.49) * mm});
            skLineSegment(sketch, "E694", {"start": v(-53.99, -2.49) * mm, "end": v(-53.8, -3.67) * mm});
            skLineSegment(sketch, "E695", {"start": v(-53.8, -3.67) * mm, "end": v(-53.64, -4.88) * mm});
            skLineSegment(sketch, "E696", {"start": v(-53.64, -4.88) * mm, "end": v(-53.53, -6.13) * mm});
            skLineSegment(sketch, "E697", {"start": v(-53.53, -6.13) * mm, "end": v(-53.47, -7.42) * mm});
            skLineSegment(sketch, "E698", {"start": v(-53.47, -7.42) * mm, "end": v(-53.45, -8.75) * mm});
            skLineSegment(sketch, "E699", {"start": v(-53.45, -8.75) * mm, "end": v(-53.45, -9.11) * mm});
            skLineSegment(sketch, "E700", {"start": v(-53.45, -9.11) * mm, "end": v(-53.46, -9.56) * mm});
            skLineSegment(sketch, "E701", {"start": v(-53.46, -9.56) * mm, "end": v(-53.47, -10.1) * mm});
            skLineSegment(sketch, "E702", {"start": v(-53.47, -10.1) * mm, "end": v(-53.49, -10.71) * mm});
            skLineSegment(sketch, "E703", {"start": v(-53.49, -10.71) * mm, "end": v(-81.9, -10.71) * mm});
            skLineSegment(sketch, "E704", {"start": v(213.4, -24.04) * mm, "end": v(213.9, -23.97) * mm});
            skLineSegment(sketch, "E705", {"start": v(213.9, -23.97) * mm, "end": v(214.96, -30.48) * mm});
            skLineSegment(sketch, "E706", {"start": v(214.96, -30.48) * mm, "end": v(214.2, -30.63) * mm});
            skLineSegment(sketch, "E707", {"start": v(214.2, -30.63) * mm, "end": v(213.44, -30.76) * mm});
            skLineSegment(sketch, "E708", {"start": v(213.44, -30.76) * mm, "end": v(212.72, -30.88) * mm});
            skLineSegment(sketch, "E709", {"start": v(212.72, -30.88) * mm, "end": v(212.01, -30.97) * mm});
            skLineSegment(sketch, "E710", {"start": v(212.01, -30.97) * mm, "end": v(211.33, -31.04) * mm});
            skLineSegment(sketch, "E711", {"start": v(211.33, -31.04) * mm, "end": v(210.66, -31.1) * mm});
            skLineSegment(sketch, "E712", {"start": v(210.66, -31.1) * mm, "end": v(210.02, -31.12) * mm});
            skLineSegment(sketch, "E713", {"start": v(210.02, -31.12) * mm, "end": v(209.4, -31.13) * mm});
            skLineSegment(sketch, "E714", {"start": v(209.4, -31.13) * mm, "end": v(208.42, -31.11) * mm});
            skLineSegment(sketch, "E715", {"start": v(208.42, -31.11) * mm, "end": v(207.5, -31.05) * mm});
            skLineSegment(sketch, "E716", {"start": v(207.5, -31.05) * mm, "end": v(206.64, -30.95) * mm});
            skLineSegment(sketch, "E717", {"start": v(206.64, -30.95) * mm, "end": v(205.83, -30.82) * mm});
            skLineSegment(sketch, "E718", {"start": v(205.83, -30.82) * mm, "end": v(205.08, -30.64) * mm});
            skLineSegment(sketch, "E719", {"start": v(205.08, -30.64) * mm, "end": v(204.39, -30.42) * mm});
            skLineSegment(sketch, "E720", {"start": v(204.39, -30.42) * mm, "end": v(203.75, -30.16) * mm});
            skLineSegment(sketch, "E721", {"start": v(203.75, -30.16) * mm, "end": v(203.17, -29.86) * mm});
            skLineSegment(sketch, "E722", {"start": v(203.17, -29.86) * mm, "end": v(202.64, -29.53) * mm});
            skLineSegment(sketch, "E723", {"start": v(202.64, -29.53) * mm, "end": v(202.15, -29.18) * mm});
            skLineSegment(sketch, "E724", {"start": v(202.15, -29.18) * mm, "end": v(201.7, -28.8) * mm});
            skLineSegment(sketch, "E725", {"start": v(201.7, -28.8) * mm, "end": v(201.29, -28.4) * mm});
            skLineSegment(sketch, "E726", {"start": v(201.29, -28.4) * mm, "end": v(200.92, -27.97) * mm});
            skLineSegment(sketch, "E727", {"start": v(200.92, -27.97) * mm, "end": v(200.6, -27.51) * mm});
            skLineSegment(sketch, "E728", {"start": v(200.6, -27.51) * mm, "end": v(200.3, -27.03) * mm});
            skLineSegment(sketch, "E729", {"start": v(200.3, -27.03) * mm, "end": v(200.06, -26.53) * mm});
            skLineSegment(sketch, "E730", {"start": v(200.06, -26.53) * mm, "end": v(199.95, -26.25) * mm});
            skLineSegment(sketch, "E731", {"start": v(199.95, -26.25) * mm, "end": v(199.85, -25.94) * mm});
            skLineSegment(sketch, "E732", {"start": v(199.85, -25.94) * mm, "end": v(199.75, -25.6) * mm});
            skLineSegment(sketch, "E733", {"start": v(199.75, -25.6) * mm, "end": v(199.67, -25.2) * mm});
            skLineSegment(sketch, "E734", {"start": v(199.67, -25.2) * mm, "end": v(199.59, -24.8) * mm});
            skLineSegment(sketch, "E735", {"start": v(199.59, -24.8) * mm, "end": v(199.51, -24.34) * mm});
            skLineSegment(sketch, "E736", {"start": v(199.51, -24.34) * mm, "end": v(199.44, -23.85) * mm});
            skLineSegment(sketch, "E737", {"start": v(199.44, -23.85) * mm, "end": v(199.38, -23.32) * mm});
            skLineSegment(sketch, "E738", {"start": v(199.38, -23.32) * mm, "end": v(199.33, -22.76) * mm});
            skLineSegment(sketch, "E739", {"start": v(199.33, -22.76) * mm, "end": v(199.29, -22.16) * mm});
            skLineSegment(sketch, "E740", {"start": v(199.29, -22.16) * mm, "end": v(199.25, -21.53) * mm});
            skLineSegment(sketch, "E741", {"start": v(199.25, -21.53) * mm, "end": v(199.22, -20.86) * mm});
            skLineSegment(sketch, "E742", {"start": v(199.22, -20.86) * mm, "end": v(199.2, -20.16) * mm});
            skLineSegment(sketch, "E743", {"start": v(199.2, -20.16) * mm, "end": v(199.17, -19.42) * mm});
            skLineSegment(sketch, "E744", {"start": v(199.17, -19.42) * mm, "end": v(199.16, -18.64) * mm});
            skLineSegment(sketch, "E745", {"start": v(199.16, -18.64) * mm, "end": v(199.16, -17.83) * mm});
            skLineSegment(sketch, "E746", {"start": v(199.16, -17.83) * mm, "end": v(199.16, 7.18) * mm});
            skLineSegment(sketch, "E747", {"start": v(199.16, 7.18) * mm, "end": v(193.76, 7.18) * mm});
            skLineSegment(sketch, "E748", {"start": v(193.76, 7.18) * mm, "end": v(193.76, 12.9) * mm});
            skLineSegment(sketch, "E749", {"start": v(193.76, 12.9) * mm, "end": v(199.16, 12.9) * mm});
            skLineSegment(sketch, "E750", {"start": v(199.16, 12.9) * mm, "end": v(199.16, 23.67) * mm});
            skLineSegment(sketch, "E751", {"start": v(199.16, 23.67) * mm, "end": v(206.49, 28.09) * mm});
            skLineSegment(sketch, "E752", {"start": v(206.49, 28.09) * mm, "end": v(206.49, 12.9) * mm});
            skLineSegment(sketch, "E753", {"start": v(206.49, 12.9) * mm, "end": v(213.9, 12.9) * mm});
            skLineSegment(sketch, "E754", {"start": v(213.9, 12.9) * mm, "end": v(213.9, 7.18) * mm});
            skLineSegment(sketch, "E755", {"start": v(213.9, 7.18) * mm, "end": v(206.49, 7.18) * mm});
            skLineSegment(sketch, "E756", {"start": v(206.49, 7.18) * mm, "end": v(206.49, -18.24) * mm});
            skLineSegment(sketch, "E757", {"start": v(206.49, -18.24) * mm, "end": v(206.5, -19) * mm});
            skLineSegment(sketch, "E758", {"start": v(206.5, -19) * mm, "end": v(206.51, -19.68) * mm});
            skLineSegment(sketch, "E759", {"start": v(206.51, -19.68) * mm, "end": v(206.54, -20.29) * mm});
            skLineSegment(sketch, "E760", {"start": v(206.54, -20.29) * mm, "end": v(206.58, -20.83) * mm});
            skLineSegment(sketch, "E761", {"start": v(206.58, -20.83) * mm, "end": v(206.64, -21.3) * mm});
            skLineSegment(sketch, "E762", {"start": v(206.64, -21.3) * mm, "end": v(206.7, -21.7) * mm});
            skLineSegment(sketch, "E763", {"start": v(206.7, -21.7) * mm, "end": v(206.78, -22.03) * mm});
            skLineSegment(sketch, "E764", {"start": v(206.78, -22.03) * mm, "end": v(206.87, -22.3) * mm});
            skLineSegment(sketch, "E765", {"start": v(206.87, -22.3) * mm, "end": v(207.1, -22.72) * mm});
            skLineSegment(sketch, "E766", {"start": v(207.1, -22.72) * mm, "end": v(207.39, -23.1) * mm});
            skLineSegment(sketch, "E767", {"start": v(207.39, -23.1) * mm, "end": v(207.73, -23.44) * mm});
            skLineSegment(sketch, "E768", {"start": v(207.73, -23.44) * mm, "end": v(208.14, -23.73) * mm});
            skLineSegment(sketch, "E769", {"start": v(208.14, -23.73) * mm, "end": v(208.38, -23.85) * mm});
            skLineSegment(sketch, "E770", {"start": v(208.38, -23.85) * mm, "end": v(208.63, -23.96) * mm});
            skLineSegment(sketch, "E771", {"start": v(208.63, -23.96) * mm, "end": v(208.9, -24.05) * mm});
            skLineSegment(sketch, "E772", {"start": v(208.9, -24.05) * mm, "end": v(209.21, -24.12) * mm});
            skLineSegment(sketch, "E773", {"start": v(209.21, -24.12) * mm, "end": v(209.54, -24.18) * mm});
            skLineSegment(sketch, "E774", {"start": v(209.54, -24.18) * mm, "end": v(209.89, -24.22) * mm});
            skLineSegment(sketch, "E775", {"start": v(209.89, -24.22) * mm, "end": v(210.26, -24.25) * mm});
            skLineSegment(sketch, "E776", {"start": v(210.26, -24.25) * mm, "end": v(210.66, -24.26) * mm});
            skLineSegment(sketch, "E777", {"start": v(210.66, -24.26) * mm, "end": v(210.98, -24.25) * mm});
            skLineSegment(sketch, "E778", {"start": v(210.98, -24.25) * mm, "end": v(211.32, -24.24) * mm});
            skLineSegment(sketch, "E779", {"start": v(211.32, -24.24) * mm, "end": v(211.7, -24.22) * mm});
            skLineSegment(sketch, "E780", {"start": v(211.7, -24.22) * mm, "end": v(212.08, -24.19) * mm});
            skLineSegment(sketch, "E781", {"start": v(212.08, -24.19) * mm, "end": v(212.5, -24.15) * mm});
            skLineSegment(sketch, "E782", {"start": v(212.5, -24.15) * mm, "end": v(212.94, -24.1) * mm});
            skLineSegment(sketch, "E783", {"start": v(212.94, -24.1) * mm, "end": v(213.4, -24.04) * mm});
            skLineSegment(sketch, "E784", {"start": v(140.17, -12.03) * mm, "end": v(140.14, -11.28) * mm});
            skLineSegment(sketch, "E785", {"start": v(140.14, -11.28) * mm, "end": v(147.63, -10.63) * mm});
            skLineSegment(sketch, "E786", {"start": v(147.63, -10.63) * mm, "end": v(147.79, -11.73) * mm});
            skLineSegment(sketch, "E787", {"start": v(147.79, -11.73) * mm, "end": v(147.99, -12.78) * mm});
            skLineSegment(sketch, "E788", {"start": v(147.99, -12.78) * mm, "end": v(148.23, -13.78) * mm});
            skLineSegment(sketch, "E789", {"start": v(148.23, -13.78) * mm, "end": v(148.52, -14.73) * mm});
            skLineSegment(sketch, "E790", {"start": v(148.52, -14.73) * mm, "end": v(148.85, -15.62) * mm});
            skLineSegment(sketch, "E791", {"start": v(148.85, -15.62) * mm, "end": v(149.22, -16.47) * mm});
            skLineSegment(sketch, "E792", {"start": v(149.22, -16.47) * mm, "end": v(149.64, -17.27) * mm});
            skLineSegment(sketch, "E793", {"start": v(149.64, -17.27) * mm, "end": v(150.1, -18.02) * mm});
            skLineSegment(sketch, "E794", {"start": v(150.1, -18.02) * mm, "end": v(150.63, -18.72) * mm});
            skLineSegment(sketch, "E795", {"start": v(150.63, -18.72) * mm, "end": v(151.21, -19.39) * mm});
            skLineSegment(sketch, "E796", {"start": v(151.21, -19.39) * mm, "end": v(151.87, -20.02) * mm});
            skLineSegment(sketch, "E797", {"start": v(151.87, -20.02) * mm, "end": v(152.59, -20.62) * mm});
            skLineSegment(sketch, "E798", {"start": v(152.59, -20.62) * mm, "end": v(153.38, -21.2) * mm});
            skLineSegment(sketch, "E799", {"start": v(153.38, -21.2) * mm, "end": v(154.23, -21.72) * mm});
            skLineSegment(sketch, "E800", {"start": v(154.23, -21.72) * mm, "end": v(155.16, -22.22) * mm});
            skLineSegment(sketch, "E801", {"start": v(155.16, -22.22) * mm, "end": v(156.14, -22.68) * mm});
            skLineSegment(sketch, "E802", {"start": v(156.14, -22.68) * mm, "end": v(157.18, -23.1) * mm});
            skLineSegment(sketch, "E803", {"start": v(157.18, -23.1) * mm, "end": v(158.26, -23.46) * mm});
            skLineSegment(sketch, "E804", {"start": v(158.26, -23.46) * mm, "end": v(159.36, -23.77) * mm});
            skLineSegment(sketch, "E805", {"start": v(159.36, -23.77) * mm, "end": v(160.5, -24.02) * mm});
            skLineSegment(sketch, "E806", {"start": v(160.5, -24.02) * mm, "end": v(161.66, -24.21) * mm});
            skLineSegment(sketch, "E807", {"start": v(161.66, -24.21) * mm, "end": v(162.86, -24.35) * mm});
            skLineSegment(sketch, "E808", {"start": v(162.86, -24.35) * mm, "end": v(164.1, -24.43) * mm});
            skLineSegment(sketch, "E809", {"start": v(164.1, -24.43) * mm, "end": v(165.35, -24.46) * mm});
            skLineSegment(sketch, "E810", {"start": v(165.35, -24.46) * mm, "end": v(166.47, -24.44) * mm});
            skLineSegment(sketch, "E811", {"start": v(166.47, -24.44) * mm, "end": v(167.56, -24.38) * mm});
            skLineSegment(sketch, "E812", {"start": v(167.56, -24.38) * mm, "end": v(168.61, -24.27) * mm});
            skLineSegment(sketch, "E813", {"start": v(168.61, -24.27) * mm, "end": v(169.63, -24.12) * mm});
            skLineSegment(sketch, "E814", {"start": v(169.63, -24.12) * mm, "end": v(170.62, -23.93) * mm});
            skLineSegment(sketch, "E815", {"start": v(170.62, -23.93) * mm, "end": v(171.57, -23.7) * mm});
            skLineSegment(sketch, "E816", {"start": v(171.57, -23.7) * mm, "end": v(172.49, -23.43) * mm});
            skLineSegment(sketch, "E817", {"start": v(172.49, -23.43) * mm, "end": v(173.38, -23.11) * mm});
            skLineSegment(sketch, "E818", {"start": v(173.38, -23.11) * mm, "end": v(174.22, -22.76) * mm});
            skLineSegment(sketch, "E819", {"start": v(174.22, -22.76) * mm, "end": v(175, -22.37) * mm});
            skLineSegment(sketch, "E820", {"start": v(175, -22.37) * mm, "end": v(175.73, -21.96) * mm});
            skLineSegment(sketch, "E821", {"start": v(175.73, -21.96) * mm, "end": v(176.4, -21.5) * mm});
            skLineSegment(sketch, "E822", {"start": v(176.4, -21.5) * mm, "end": v(177.03, -21.03) * mm});
            skLineSegment(sketch, "E823", {"start": v(177.03, -21.03) * mm, "end": v(177.6, -20.52) * mm});
            skLineSegment(sketch, "E824", {"start": v(177.6, -20.52) * mm, "end": v(178.1, -19.98) * mm});
            skLineSegment(sketch, "E825", {"start": v(178.1, -19.98) * mm, "end": v(178.55, -19.4) * mm});
            skLineSegment(sketch, "E826", {"start": v(178.55, -19.4) * mm, "end": v(178.95, -18.81) * mm});
            skLineSegment(sketch, "E827", {"start": v(178.95, -18.81) * mm, "end": v(179.3, -18.2) * mm});
            skLineSegment(sketch, "E828", {"start": v(179.3, -18.2) * mm, "end": v(179.59, -17.58) * mm});
            skLineSegment(sketch, "E829", {"start": v(179.59, -17.58) * mm, "end": v(179.83, -16.95) * mm});
            skLineSegment(sketch, "E830", {"start": v(179.83, -16.95) * mm, "end": v(180.01, -16.3) * mm});
            skLineSegment(sketch, "E831", {"start": v(180.01, -16.3) * mm, "end": v(180.15, -15.64) * mm});
            skLineSegment(sketch, "E832", {"start": v(180.15, -15.64) * mm, "end": v(180.22, -14.96) * mm});
            skLineSegment(sketch, "E833", {"start": v(180.22, -14.96) * mm, "end": v(180.25, -14.27) * mm});
            skLineSegment(sketch, "E834", {"start": v(180.25, -14.27) * mm, "end": v(180.23, -13.58) * mm});
            skLineSegment(sketch, "E835", {"start": v(180.23, -13.58) * mm, "end": v(180.15, -12.9) * mm});
            skLineSegment(sketch, "E836", {"start": v(180.15, -12.9) * mm, "end": v(180.02, -12.25) * mm});
            skLineSegment(sketch, "E837", {"start": v(180.02, -12.25) * mm, "end": v(179.84, -11.63) * mm});
            skLineSegment(sketch, "E838", {"start": v(179.84, -11.63) * mm, "end": v(179.61, -11.02) * mm});
            skLineSegment(sketch, "E839", {"start": v(179.61, -11.02) * mm, "end": v(179.33, -10.44) * mm});
            skLineSegment(sketch, "E840", {"start": v(179.33, -10.44) * mm, "end": v(179, -9.88) * mm});
            skLineSegment(sketch, "E841", {"start": v(179, -9.88) * mm, "end": v(178.61, -9.34) * mm});
            skLineSegment(sketch, "E842", {"start": v(178.61, -9.34) * mm, "end": v(178.17, -8.82) * mm});
            skLineSegment(sketch, "E843", {"start": v(178.17, -8.82) * mm, "end": v(177.66, -8.33) * mm});
            skLineSegment(sketch, "E844", {"start": v(177.66, -8.33) * mm, "end": v(177.09, -7.85) * mm});
            skLineSegment(sketch, "E845", {"start": v(177.09, -7.85) * mm, "end": v(176.45, -7.4) * mm});
            skLineSegment(sketch, "E846", {"start": v(176.45, -7.4) * mm, "end": v(175.74, -6.97) * mm});
            skLineSegment(sketch, "E847", {"start": v(175.74, -6.97) * mm, "end": v(174.96, -6.56) * mm});
            skLineSegment(sketch, "E848", {"start": v(174.96, -6.56) * mm, "end": v(174.12, -6.17) * mm});
            skLineSegment(sketch, "E849", {"start": v(174.12, -6.17) * mm, "end": v(173.21, -5.8) * mm});
            skLineSegment(sketch, "E850", {"start": v(173.21, -5.8) * mm, "end": v(172.89, -5.68) * mm});
            skLineSegment(sketch, "E851", {"start": v(172.89, -5.68) * mm, "end": v(172.52, -5.55) * mm});
            skLineSegment(sketch, "E852", {"start": v(172.52, -5.55) * mm, "end": v(172.1, -5.4) * mm});
            skLineSegment(sketch, "E853", {"start": v(172.1, -5.4) * mm, "end": v(171.64, -5.26) * mm});
            skLineSegment(sketch, "E854", {"start": v(171.64, -5.26) * mm, "end": v(171.13, -5.1) * mm});
            skLineSegment(sketch, "E855", {"start": v(171.13, -5.1) * mm, "end": v(170.58, -4.95) * mm});
            skLineSegment(sketch, "E856", {"start": v(170.58, -4.95) * mm, "end": v(169.98, -4.78) * mm});
            skLineSegment(sketch, "E857", {"start": v(169.98, -4.78) * mm, "end": v(169.33, -4.6) * mm});
            skLineSegment(sketch, "E858", {"start": v(169.33, -4.6) * mm, "end": v(168.64, -4.4) * mm});
            skLineSegment(sketch, "E859", {"start": v(168.64, -4.4) * mm, "end": v(167.9, -4.21) * mm});
            skLineSegment(sketch, "E860", {"start": v(167.9, -4.21) * mm, "end": v(167.13, -4.01) * mm});
            skLineSegment(sketch, "E861", {"start": v(167.13, -4.01) * mm, "end": v(166.3, -3.8) * mm});
            skLineSegment(sketch, "E862", {"start": v(166.3, -3.8) * mm, "end": v(165.42, -3.58) * mm});
            skLineSegment(sketch, "E863", {"start": v(165.42, -3.58) * mm, "end": v(164.5, -3.35) * mm});
            skLineSegment(sketch, "E864", {"start": v(164.5, -3.35) * mm, "end": v(163.54, -3.12) * mm});
            skLineSegment(sketch, "E865", {"start": v(163.54, -3.12) * mm, "end": v(162.53, -2.87) * mm});
            skLineSegment(sketch, "E866", {"start": v(162.53, -2.87) * mm, "end": v(161.52, -2.63) * mm});
            skLineSegment(sketch, "E867", {"start": v(161.52, -2.63) * mm, "end": v(160.54, -2.38) * mm});
            skLineSegment(sketch, "E868", {"start": v(160.54, -2.38) * mm, "end": v(159.6, -2.14) * mm});
            skLineSegment(sketch, "E869", {"start": v(159.6, -2.14) * mm, "end": v(158.7, -1.9) * mm});
            skLineSegment(sketch, "E870", {"start": v(158.7, -1.9) * mm, "end": v(157.85, -1.65) * mm});
            skLineSegment(sketch, "E871", {"start": v(157.85, -1.65) * mm, "end": v(157.03, -1.42) * mm});
            skLineSegment(sketch, "E872", {"start": v(157.03, -1.42) * mm, "end": v(156.24, -1.18) * mm});
            skLineSegment(sketch, "E873", {"start": v(156.24, -1.18) * mm, "end": v(155.5, -0.94) * mm});
            skLineSegment(sketch, "E874", {"start": v(155.5, -0.94) * mm, "end": v(154.8, -0.71) * mm});
            skLineSegment(sketch, "E875", {"start": v(154.8, -0.71) * mm, "end": v(154.13, -0.48) * mm});
            skLineSegment(sketch, "E876", {"start": v(154.13, -0.48) * mm, "end": v(153.5, -0.25) * mm});
            skLineSegment(sketch, "E877", {"start": v(153.5, -0.25) * mm, "end": v(152.91, -0.02) * mm});
            skLineSegment(sketch, "E878", {"start": v(152.91, -0.02) * mm, "end": v(152.36, 0.2) * mm});
            skLineSegment(sketch, "E879", {"start": v(152.36, 0.2) * mm, "end": v(151.85, 0.43) * mm});
            skLineSegment(sketch, "E880", {"start": v(151.85, 0.43) * mm, "end": v(151.38, 0.65) * mm});
            skLineSegment(sketch, "E881", {"start": v(151.38, 0.65) * mm, "end": v(150.95, 0.87) * mm});
            skLineSegment(sketch, "E882", {"start": v(150.95, 0.87) * mm, "end": v(149.9, 1.45) * mm});
            skLineSegment(sketch, "E883", {"start": v(149.9, 1.45) * mm, "end": v(148.94, 2.07) * mm});
            skLineSegment(sketch, "E884", {"start": v(148.94, 2.07) * mm, "end": v(148.03, 2.71) * mm});
            skLineSegment(sketch, "E885", {"start": v(148.03, 2.71) * mm, "end": v(147.2, 3.4) * mm});
            skLineSegment(sketch, "E886", {"start": v(147.2, 3.4) * mm, "end": v(146.43, 4.1) * mm});
            skLineSegment(sketch, "E887", {"start": v(146.43, 4.1) * mm, "end": v(145.73, 4.86) * mm});
            skLineSegment(sketch, "E888", {"start": v(145.73, 4.86) * mm, "end": v(145.1, 5.64) * mm});
            skLineSegment(sketch, "E889", {"start": v(145.1, 5.64) * mm, "end": v(144.54, 6.46) * mm});
            skLineSegment(sketch, "E890", {"start": v(144.54, 6.46) * mm, "end": v(144.05, 7.3) * mm});
            skLineSegment(sketch, "E891", {"start": v(144.05, 7.3) * mm, "end": v(143.62, 8.18) * mm});
            skLineSegment(sketch, "E892", {"start": v(143.62, 8.18) * mm, "end": v(143.26, 9.07) * mm});
            skLineSegment(sketch, "E893", {"start": v(143.26, 9.07) * mm, "end": v(142.96, 10) * mm});
            skLineSegment(sketch, "E894", {"start": v(142.96, 10) * mm, "end": v(142.73, 10.94) * mm});
            skLineSegment(sketch, "E895", {"start": v(142.73, 10.94) * mm, "end": v(142.57, 11.91) * mm});
            skLineSegment(sketch, "E896", {"start": v(142.57, 11.91) * mm, "end": v(142.47, 12.9) * mm});
            skLineSegment(sketch, "E897", {"start": v(142.47, 12.9) * mm, "end": v(142.43, 13.93) * mm});
            skLineSegment(sketch, "E898", {"start": v(142.43, 13.93) * mm, "end": v(142.47, 15.05) * mm});
            skLineSegment(sketch, "E899", {"start": v(142.47, 15.05) * mm, "end": v(142.6, 16.16) * mm});
            skLineSegment(sketch, "E900", {"start": v(142.6, 16.16) * mm, "end": v(142.8, 17.25) * mm});
            skLineSegment(sketch, "E901", {"start": v(142.8, 17.25) * mm, "end": v(143.08, 18.32) * mm});
            skLineSegment(sketch, "E902", {"start": v(143.08, 18.32) * mm, "end": v(143.44, 19.38) * mm});
            skLineSegment(sketch, "E903", {"start": v(143.44, 19.38) * mm, "end": v(143.88, 20.4) * mm});
            skLineSegment(sketch, "E904", {"start": v(143.88, 20.4) * mm, "end": v(144.4, 21.42) * mm});
            skLineSegment(sketch, "E905", {"start": v(144.4, 21.42) * mm, "end": v(145.01, 22.42) * mm});
            skLineSegment(sketch, "E906", {"start": v(145.01, 22.42) * mm, "end": v(145.7, 23.38) * mm});
            skLineSegment(sketch, "E907", {"start": v(145.7, 23.38) * mm, "end": v(146.45, 24.28) * mm});
            skLineSegment(sketch, "E908", {"start": v(146.45, 24.28) * mm, "end": v(147.28, 25.12) * mm});
            skLineSegment(sketch, "E909", {"start": v(147.28, 25.12) * mm, "end": v(148.18, 25.9) * mm});
            skLineSegment(sketch, "E910", {"start": v(148.18, 25.9) * mm, "end": v(149.16, 26.61) * mm});
            skLineSegment(sketch, "E911", {"start": v(149.16, 26.61) * mm, "end": v(150.22, 27.27) * mm});
            skLineSegment(sketch, "E912", {"start": v(150.22, 27.27) * mm, "end": v(151.34, 27.88) * mm});
            skLineSegment(sketch, "E913", {"start": v(151.34, 27.88) * mm, "end": v(152.54, 28.42) * mm});
            skLineSegment(sketch, "E914", {"start": v(152.54, 28.42) * mm, "end": v(153.8, 28.9) * mm});
            skLineSegment(sketch, "E915", {"start": v(153.8, 28.9) * mm, "end": v(155.09, 29.31) * mm});
            skLineSegment(sketch, "E916", {"start": v(155.09, 29.31) * mm, "end": v(156.41, 29.66) * mm});
            skLineSegment(sketch, "E917", {"start": v(156.41, 29.66) * mm, "end": v(157.77, 29.95) * mm});
            skLineSegment(sketch, "E918", {"start": v(157.77, 29.95) * mm, "end": v(159.17, 30.18) * mm});
            skLineSegment(sketch, "E919", {"start": v(159.17, 30.18) * mm, "end": v(160.6, 30.34) * mm});
            skLineSegment(sketch, "E920", {"start": v(160.6, 30.34) * mm, "end": v(162.06, 30.43) * mm});
            skLineSegment(sketch, "E921", {"start": v(162.06, 30.43) * mm, "end": v(163.55, 30.46) * mm});
            skLineSegment(sketch, "E922", {"start": v(163.55, 30.46) * mm, "end": v(165.2, 30.43) * mm});
            skLineSegment(sketch, "E923", {"start": v(165.2, 30.43) * mm, "end": v(166.79, 30.33) * mm});
            skLineSegment(sketch, "E924", {"start": v(166.79, 30.33) * mm, "end": v(168.33, 30.16) * mm});
            skLineSegment(sketch, "E925", {"start": v(168.33, 30.16) * mm, "end": v(169.83, 29.93) * mm});
            skLineSegment(sketch, "E926", {"start": v(169.83, 29.93) * mm, "end": v(171.28, 29.62) * mm});
            skLineSegment(sketch, "E927", {"start": v(171.28, 29.62) * mm, "end": v(172.67, 29.25) * mm});
            skLineSegment(sketch, "E928", {"start": v(172.67, 29.25) * mm, "end": v(174.02, 28.82) * mm});
            skLineSegment(sketch, "E929", {"start": v(174.02, 28.82) * mm, "end": v(175.32, 28.31) * mm});
            skLineSegment(sketch, "E930", {"start": v(175.32, 28.31) * mm, "end": v(175.95, 28.04) * mm});
            skLineSegment(sketch, "E931", {"start": v(175.95, 28.04) * mm, "end": v(176.56, 27.75) * mm});
            skLineSegment(sketch, "E932", {"start": v(176.56, 27.75) * mm, "end": v(177.15, 27.44) * mm});
            skLineSegment(sketch, "E933", {"start": v(177.15, 27.44) * mm, "end": v(177.72, 27.11) * mm});
            skLineSegment(sketch, "E934", {"start": v(177.72, 27.11) * mm, "end": v(178.27, 26.77) * mm});
            skLineSegment(sketch, "E935", {"start": v(178.27, 26.77) * mm, "end": v(178.81, 26.42) * mm});
            skLineSegment(sketch, "E936", {"start": v(178.81, 26.42) * mm, "end": v(179.33, 26.05) * mm});
            skLineSegment(sketch, "E937", {"start": v(179.33, 26.05) * mm, "end": v(179.83, 25.66) * mm});
            skLineSegment(sketch, "E938", {"start": v(179.83, 25.66) * mm, "end": v(180.3, 25.26) * mm});
            skLineSegment(sketch, "E939", {"start": v(180.3, 25.26) * mm, "end": v(180.77, 24.84) * mm});
            skLineSegment(sketch, "E940", {"start": v(180.77, 24.84) * mm, "end": v(181.21, 24.4) * mm});
            skLineSegment(sketch, "E941", {"start": v(181.21, 24.4) * mm, "end": v(181.64, 23.95) * mm});
            skLineSegment(sketch, "E942", {"start": v(181.64, 23.95) * mm, "end": v(182.05, 23.49) * mm});
            skLineSegment(sketch, "E943", {"start": v(182.05, 23.49) * mm, "end": v(182.43, 23) * mm});
            skLineSegment(sketch, "E944", {"start": v(182.43, 23) * mm, "end": v(182.8, 22.5) * mm});
            skLineSegment(sketch, "E945", {"start": v(182.8, 22.5) * mm, "end": v(183.16, 22) * mm});
            skLineSegment(sketch, "E946", {"start": v(183.16, 22) * mm, "end": v(183.8, 20.93) * mm});
            skLineSegment(sketch, "E947", {"start": v(183.8, 20.93) * mm, "end": v(184.37, 19.83) * mm});
            skLineSegment(sketch, "E948", {"start": v(184.37, 19.83) * mm, "end": v(184.86, 18.7) * mm});
            skLineSegment(sketch, "E949", {"start": v(184.86, 18.7) * mm, "end": v(185.26, 17.54) * mm});
            skLineSegment(sketch, "E950", {"start": v(185.26, 17.54) * mm, "end": v(185.6, 16.34) * mm});
            skLineSegment(sketch, "E951", {"start": v(185.6, 16.34) * mm, "end": v(185.84, 15.1) * mm});
            skLineSegment(sketch, "E952", {"start": v(185.84, 15.1) * mm, "end": v(186.01, 13.84) * mm});
            skLineSegment(sketch, "E953", {"start": v(186.01, 13.84) * mm, "end": v(186.1, 12.54) * mm});
            skLineSegment(sketch, "E954", {"start": v(186.1, 12.54) * mm, "end": v(178.5, 11.96) * mm});
            skLineSegment(sketch, "E955", {"start": v(178.5, 11.96) * mm, "end": v(178.4, 12.66) * mm});
            skLineSegment(sketch, "E956", {"start": v(178.4, 12.66) * mm, "end": v(178.3, 13.34) * mm});
            skLineSegment(sketch, "E957", {"start": v(178.3, 13.34) * mm, "end": v(178.16, 14) * mm});
            skLineSegment(sketch, "E958", {"start": v(178.16, 14) * mm, "end": v(178, 14.63) * mm});
            skLineSegment(sketch, "E959", {"start": v(178, 14.63) * mm, "end": v(177.82, 15.25) * mm});
            skLineSegment(sketch, "E960", {"start": v(177.82, 15.25) * mm, "end": v(177.62, 15.84) * mm});
            skLineSegment(sketch, "E961", {"start": v(177.62, 15.84) * mm, "end": v(177.4, 16.4) * mm});
            skLineSegment(sketch, "E962", {"start": v(177.4, 16.4) * mm, "end": v(177.15, 16.96) * mm});
            skLineSegment(sketch, "E963", {"start": v(177.15, 16.96) * mm, "end": v(176.87, 17.48) * mm});
            skLineSegment(sketch, "E964", {"start": v(176.87, 17.48) * mm, "end": v(176.58, 17.99) * mm});
            skLineSegment(sketch, "E965", {"start": v(176.58, 17.99) * mm, "end": v(176.26, 18.47) * mm});
            skLineSegment(sketch, "E966", {"start": v(176.26, 18.47) * mm, "end": v(175.92, 18.93) * mm});
            skLineSegment(sketch, "E967", {"start": v(175.92, 18.93) * mm, "end": v(175.56, 19.37) * mm});
            skLineSegment(sketch, "E968", {"start": v(175.56, 19.37) * mm, "end": v(175.18, 19.79) * mm});
            skLineSegment(sketch, "E969", {"start": v(175.18, 19.79) * mm, "end": v(174.77, 20.18) * mm});
            skLineSegment(sketch, "E970", {"start": v(174.77, 20.18) * mm, "end": v(174.34, 20.56) * mm});
            skLineSegment(sketch, "E971", {"start": v(174.34, 20.56) * mm, "end": v(173.88, 20.91) * mm});
            skLineSegment(sketch, "E972", {"start": v(173.88, 20.91) * mm, "end": v(173.4, 21.24) * mm});
            skLineSegment(sketch, "E973", {"start": v(173.4, 21.24) * mm, "end": v(172.9, 21.55) * mm});
            skLineSegment(sketch, "E974", {"start": v(172.9, 21.55) * mm, "end": v(172.36, 21.83) * mm});
            skLineSegment(sketch, "E975", {"start": v(172.36, 21.83) * mm, "end": v(171.8, 22.1) * mm});
            skLineSegment(sketch, "E976", {"start": v(171.8, 22.1) * mm, "end": v(171.2, 22.33) * mm});
            skLineSegment(sketch, "E977", {"start": v(171.2, 22.33) * mm, "end": v(170.6, 22.55) * mm});
            skLineSegment(sketch, "E978", {"start": v(170.6, 22.55) * mm, "end": v(169.95, 22.74) * mm});
            skLineSegment(sketch, "E979", {"start": v(169.95, 22.74) * mm, "end": v(169.29, 22.9) * mm});
            skLineSegment(sketch, "E980", {"start": v(169.29, 22.9) * mm, "end": v(168.6, 23.06) * mm});
            skLineSegment(sketch, "E981", {"start": v(168.6, 23.06) * mm, "end": v(167.87, 23.18) * mm});
            skLineSegment(sketch, "E982", {"start": v(167.87, 23.18) * mm, "end": v(167.13, 23.28) * mm});
            skLineSegment(sketch, "E983", {"start": v(167.13, 23.28) * mm, "end": v(166.36, 23.36) * mm});
            skLineSegment(sketch, "E984", {"start": v(166.36, 23.36) * mm, "end": v(165.56, 23.42) * mm});
            skLineSegment(sketch, "E985", {"start": v(165.56, 23.42) * mm, "end": v(164.73, 23.45) * mm});
            skLineSegment(sketch, "E986", {"start": v(164.73, 23.45) * mm, "end": v(163.88, 23.46) * mm});
            skLineSegment(sketch, "E987", {"start": v(163.88, 23.46) * mm, "end": v(163, 23.45) * mm});
            skLineSegment(sketch, "E988", {"start": v(163, 23.45) * mm, "end": v(162.14, 23.42) * mm});
            skLineSegment(sketch, "E989", {"start": v(162.14, 23.42) * mm, "end": v(161.32, 23.37) * mm});
            skLineSegment(sketch, "E990", {"start": v(161.32, 23.37) * mm, "end": v(160.52, 23.3) * mm});
            skLineSegment(sketch, "E991", {"start": v(160.52, 23.3) * mm, "end": v(159.76, 23.2) * mm});
            skLineSegment(sketch, "E992", {"start": v(159.76, 23.2) * mm, "end": v(159.03, 23.1) * mm});
            skLineSegment(sketch, "E993", {"start": v(159.03, 23.1) * mm, "end": v(158.33, 22.96) * mm});
            skLineSegment(sketch, "E994", {"start": v(158.33, 22.96) * mm, "end": v(157.65, 22.8) * mm});
            skLineSegment(sketch, "E995", {"start": v(157.65, 22.8) * mm, "end": v(157.01, 22.63) * mm});
            skLineSegment(sketch, "E996", {"start": v(157.01, 22.63) * mm, "end": v(156.4, 22.43) * mm});
            skLineSegment(sketch, "E997", {"start": v(156.4, 22.43) * mm, "end": v(155.82, 22.22) * mm});
            skLineSegment(sketch, "E998", {"start": v(155.82, 22.22) * mm, "end": v(155.27, 21.98) * mm});
            skLineSegment(sketch, "E999", {"start": v(155.27, 21.98) * mm, "end": v(154.76, 21.72) * mm});
            skLineSegment(sketch, "E1000", {"start": v(154.76, 21.72) * mm, "end": v(154.27, 21.44) * mm});
            skLineSegment(sketch, "E1001", {"start": v(154.27, 21.44) * mm, "end": v(153.8, 21.14) * mm});
            skLineSegment(sketch, "E1002", {"start": v(153.8, 21.14) * mm, "end": v(153.38, 20.82) * mm});
            skLineSegment(sketch, "E1003", {"start": v(153.38, 20.82) * mm, "end": v(152.98, 20.5) * mm});
            skLineSegment(sketch, "E1004", {"start": v(152.98, 20.5) * mm, "end": v(152.61, 20.15) * mm});
            skLineSegment(sketch, "E1005", {"start": v(152.61, 20.15) * mm, "end": v(152.26, 19.8) * mm});
            skLineSegment(sketch, "E1006", {"start": v(152.26, 19.8) * mm, "end": v(151.94, 19.44) * mm});
            skLineSegment(sketch, "E1007", {"start": v(151.94, 19.44) * mm, "end": v(151.64, 19.07) * mm});
            skLineSegment(sketch, "E1008", {"start": v(151.64, 19.07) * mm, "end": v(151.37, 18.7) * mm});
            skLineSegment(sketch, "E1009", {"start": v(151.37, 18.7) * mm, "end": v(151.13, 18.3) * mm});
            skLineSegment(sketch, "E1010", {"start": v(151.13, 18.3) * mm, "end": v(150.91, 17.91) * mm});
            skLineSegment(sketch, "E1011", {"start": v(150.91, 17.91) * mm, "end": v(150.72, 17.51) * mm});
            skLineSegment(sketch, "E1012", {"start": v(150.72, 17.51) * mm, "end": v(150.55, 17.1) * mm});
            skLineSegment(sketch, "E1013", {"start": v(150.55, 17.1) * mm, "end": v(150.4, 16.68) * mm});
            skLineSegment(sketch, "E1014", {"start": v(150.4, 16.68) * mm, "end": v(150.3, 16.25) * mm});
            skLineSegment(sketch, "E1015", {"start": v(150.3, 16.25) * mm, "end": v(150.2, 15.82) * mm});
            skLineSegment(sketch, "E1016", {"start": v(150.2, 15.82) * mm, "end": v(150.14, 15.37) * mm});
            skLineSegment(sketch, "E1017", {"start": v(150.14, 15.37) * mm, "end": v(150.1, 14.92) * mm});
            skLineSegment(sketch, "E1018", {"start": v(150.1, 14.92) * mm, "end": v(150.09, 14.46) * mm});
            skLineSegment(sketch, "E1019", {"start": v(150.09, 14.46) * mm, "end": v(150.12, 13.67) * mm});
            skLineSegment(sketch, "E1020", {"start": v(150.12, 13.67) * mm, "end": v(150.23, 12.92) * mm});
            skLineSegment(sketch, "E1021", {"start": v(150.23, 12.92) * mm, "end": v(150.42, 12.2) * mm});
            skLineSegment(sketch, "E1022", {"start": v(150.42, 12.2) * mm, "end": v(150.67, 11.51) * mm});
            skLineSegment(sketch, "E1023", {"start": v(150.67, 11.51) * mm, "end": v(151, 10.87) * mm});
            skLineSegment(sketch, "E1024", {"start": v(151, 10.87) * mm, "end": v(151.4, 10.26) * mm});
            skLineSegment(sketch, "E1025", {"start": v(151.4, 10.26) * mm, "end": v(151.87, 9.68) * mm});
            skLineSegment(sketch, "E1026", {"start": v(151.87, 9.68) * mm, "end": v(152.42, 9.14) * mm});
            skLineSegment(sketch, "E1027", {"start": v(152.42, 9.14) * mm, "end": v(152.74, 8.88) * mm});
            skLineSegment(sketch, "E1028", {"start": v(152.74, 8.88) * mm, "end": v(153.1, 8.62) * mm});
            skLineSegment(sketch, "E1029", {"start": v(153.1, 8.62) * mm, "end": v(153.54, 8.35) * mm});
            skLineSegment(sketch, "E1030", {"start": v(153.54, 8.35) * mm, "end": v(154.03, 8.09) * mm});
            skLineSegment(sketch, "E1031", {"start": v(154.03, 8.09) * mm, "end": v(154.57, 7.83) * mm});
            skLineSegment(sketch, "E1032", {"start": v(154.57, 7.83) * mm, "end": v(155.18, 7.56) * mm});
            skLineSegment(sketch, "E1033", {"start": v(155.18, 7.56) * mm, "end": v(155.84, 7.3) * mm});
            skLineSegment(sketch, "E1034", {"start": v(155.84, 7.3) * mm, "end": v(156.56, 7.03) * mm});
            skLineSegment(sketch, "E1035", {"start": v(156.56, 7.03) * mm, "end": v(157.34, 6.76) * mm});
            skLineSegment(sketch, "E1036", {"start": v(157.34, 6.76) * mm, "end": v(158.17, 6.5) * mm});
            skLineSegment(sketch, "E1037", {"start": v(158.17, 6.5) * mm, "end": v(159.06, 6.22) * mm});
            skLineSegment(sketch, "E1038", {"start": v(159.06, 6.22) * mm, "end": v(160.01, 5.95) * mm});
            skLineSegment(sketch, "E1039", {"start": v(160.01, 5.95) * mm, "end": v(161.02, 5.68) * mm});
            skLineSegment(sketch, "E1040", {"start": v(161.02, 5.68) * mm, "end": v(162.09, 5.4) * mm});
            skLineSegment(sketch, "E1041", {"start": v(162.09, 5.4) * mm, "end": v(163.21, 5.14) * mm});
            skLineSegment(sketch, "E1042", {"start": v(163.21, 5.14) * mm, "end": v(164.4, 4.86) * mm});
            skLineSegment(sketch, "E1043", {"start": v(164.4, 4.86) * mm, "end": v(165.58, 4.6) * mm});
            skLineSegment(sketch, "E1044", {"start": v(165.58, 4.6) * mm, "end": v(166.72, 4.32) * mm});
            skLineSegment(sketch, "E1045", {"start": v(166.72, 4.32) * mm, "end": v(167.8, 4.06) * mm});
            skLineSegment(sketch, "E1046", {"start": v(167.8, 4.06) * mm, "end": v(168.85, 3.8) * mm});
            skLineSegment(sketch, "E1047", {"start": v(168.85, 3.8) * mm, "end": v(169.85, 3.55) * mm});
            skLineSegment(sketch, "E1048", {"start": v(169.85, 3.55) * mm, "end": v(170.8, 3.3) * mm});
            skLineSegment(sketch, "E1049", {"start": v(170.8, 3.3) * mm, "end": v(171.7, 3.05) * mm});
            skLineSegment(sketch, "E1050", {"start": v(171.7, 3.05) * mm, "end": v(172.55, 2.81) * mm});
            skLineSegment(sketch, "E1051", {"start": v(172.55, 2.81) * mm, "end": v(173.36, 2.57) * mm});
            skLineSegment(sketch, "E1052", {"start": v(173.36, 2.57) * mm, "end": v(174.12, 2.34) * mm});
            skLineSegment(sketch, "E1053", {"start": v(174.12, 2.34) * mm, "end": v(174.83, 2.11) * mm});
            skLineSegment(sketch, "E1054", {"start": v(174.83, 2.11) * mm, "end": v(175.5, 1.89) * mm});
            skLineSegment(sketch, "E1055", {"start": v(175.5, 1.89) * mm, "end": v(176.1, 1.67) * mm});
            skLineSegment(sketch, "E1056", {"start": v(176.1, 1.67) * mm, "end": v(176.68, 1.45) * mm});
            skLineSegment(sketch, "E1057", {"start": v(176.68, 1.45) * mm, "end": v(177.2, 1.24) * mm});
            skLineSegment(sketch, "E1058", {"start": v(177.2, 1.24) * mm, "end": v(177.67, 1.04) * mm});
            skLineSegment(sketch, "E1059", {"start": v(177.67, 1.04) * mm, "end": v(178.94, 0.41) * mm});
            skLineSegment(sketch, "E1060", {"start": v(178.94, 0.41) * mm, "end": v(180.12, -0.25) * mm});
            skLineSegment(sketch, "E1061", {"start": v(180.12, -0.25) * mm, "end": v(181.22, -0.96) * mm});
            skLineSegment(sketch, "E1062", {"start": v(181.22, -0.96) * mm, "end": v(182.23, -1.7) * mm});
            skLineSegment(sketch, "E1063", {"start": v(182.23, -1.7) * mm, "end": v(183.15, -2.49) * mm});
            skLineSegment(sketch, "E1064", {"start": v(183.15, -2.49) * mm, "end": v(183.99, -3.31) * mm});
            skLineSegment(sketch, "E1065", {"start": v(183.99, -3.31) * mm, "end": v(184.74, -4.18) * mm});
            skLineSegment(sketch, "E1066", {"start": v(184.74, -4.18) * mm, "end": v(185.4, -5.08) * mm});
            skLineSegment(sketch, "E1067", {"start": v(185.4, -5.08) * mm, "end": v(186, -6.03) * mm});
            skLineSegment(sketch, "E1068", {"start": v(186, -6.03) * mm, "end": v(186.5, -7) * mm});
            skLineSegment(sketch, "E1069", {"start": v(186.5, -7) * mm, "end": v(186.93, -8.02) * mm});
            skLineSegment(sketch, "E1070", {"start": v(186.93, -8.02) * mm, "end": v(187.28, -9.07) * mm});
            skLineSegment(sketch, "E1071", {"start": v(187.28, -9.07) * mm, "end": v(187.55, -10.15) * mm});
            skLineSegment(sketch, "E1072", {"start": v(187.55, -10.15) * mm, "end": v(187.75, -11.27) * mm});
            skLineSegment(sketch, "E1073", {"start": v(187.75, -11.27) * mm, "end": v(187.87, -12.43) * mm});
            skLineSegment(sketch, "E1074", {"start": v(187.87, -12.43) * mm, "end": v(187.9, -13.62) * mm});
            skLineSegment(sketch, "E1075", {"start": v(187.9, -13.62) * mm, "end": v(187.86, -14.8) * mm});
            skLineSegment(sketch, "E1076", {"start": v(187.86, -14.8) * mm, "end": v(187.73, -15.98) * mm});
            skLineSegment(sketch, "E1077", {"start": v(187.73, -15.98) * mm, "end": v(187.52, -17.13) * mm});
            skLineSegment(sketch, "E1078", {"start": v(187.52, -17.13) * mm, "end": v(187.22, -18.27) * mm});
            skLineSegment(sketch, "E1079", {"start": v(187.22, -18.27) * mm, "end": v(186.83, -19.39) * mm});
            skLineSegment(sketch, "E1080", {"start": v(186.83, -19.39) * mm, "end": v(186.36, -20.49) * mm});
            skLineSegment(sketch, "E1081", {"start": v(186.36, -20.49) * mm, "end": v(185.8, -21.57) * mm});
            skLineSegment(sketch, "E1082", {"start": v(185.8, -21.57) * mm, "end": v(185.16, -22.64) * mm});
            skLineSegment(sketch, "E1083", {"start": v(185.16, -22.64) * mm, "end": v(184.44, -23.67) * mm});
            skLineSegment(sketch, "E1084", {"start": v(184.44, -23.67) * mm, "end": v(183.64, -24.64) * mm});
            skLineSegment(sketch, "E1085", {"start": v(183.64, -24.64) * mm, "end": v(182.77, -25.55) * mm});
            skLineSegment(sketch, "E1086", {"start": v(182.77, -25.55) * mm, "end": v(181.82, -26.4) * mm});
            skLineSegment(sketch, "E1087", {"start": v(181.82, -26.4) * mm, "end": v(180.8, -27.2) * mm});
            skLineSegment(sketch, "E1088", {"start": v(180.8, -27.2) * mm, "end": v(179.7, -27.94) * mm});
            skLineSegment(sketch, "E1089", {"start": v(179.7, -27.94) * mm, "end": v(178.53, -28.61) * mm});
            skLineSegment(sketch, "E1090", {"start": v(178.53, -28.61) * mm, "end": v(177.28, -29.23) * mm});
            skLineSegment(sketch, "E1091", {"start": v(177.28, -29.23) * mm, "end": v(175.98, -29.78) * mm});
            skLineSegment(sketch, "E1092", {"start": v(175.98, -29.78) * mm, "end": v(174.64, -30.26) * mm});
            skLineSegment(sketch, "E1093", {"start": v(174.64, -30.26) * mm, "end": v(173.25, -30.66) * mm});
            skLineSegment(sketch, "E1094", {"start": v(173.25, -30.66) * mm, "end": v(171.83, -31) * mm});
            skLineSegment(sketch, "E1095", {"start": v(171.83, -31) * mm, "end": v(170.36, -31.25) * mm});
            skLineSegment(sketch, "E1096", {"start": v(170.36, -31.25) * mm, "end": v(168.85, -31.44) * mm});
            skLineSegment(sketch, "E1097", {"start": v(168.85, -31.44) * mm, "end": v(167.3, -31.55) * mm});
            skLineSegment(sketch, "E1098", {"start": v(167.3, -31.55) * mm, "end": v(165.72, -31.58) * mm});
            skLineSegment(sketch, "E1099", {"start": v(165.72, -31.58) * mm, "end": v(164.71, -31.57) * mm});
            skLineSegment(sketch, "E1100", {"start": v(164.71, -31.57) * mm, "end": v(163.73, -31.55) * mm});
            skLineSegment(sketch, "E1101", {"start": v(163.73, -31.55) * mm, "end": v(162.76, -31.5) * mm});
            skLineSegment(sketch, "E1102", {"start": v(162.76, -31.5) * mm, "end": v(161.81, -31.43) * mm});
            skLineSegment(sketch, "E1103", {"start": v(161.81, -31.43) * mm, "end": v(160.89, -31.35) * mm});
            skLineSegment(sketch, "E1104", {"start": v(160.89, -31.35) * mm, "end": v(159.98, -31.25) * mm});
            skLineSegment(sketch, "E1105", {"start": v(159.98, -31.25) * mm, "end": v(159.1, -31.13) * mm});
            skLineSegment(sketch, "E1106", {"start": v(159.1, -31.13) * mm, "end": v(158.24, -30.99) * mm});
            skLineSegment(sketch, "E1107", {"start": v(158.24, -30.99) * mm, "end": v(157.4, -30.83) * mm});
            skLineSegment(sketch, "E1108", {"start": v(157.4, -30.83) * mm, "end": v(156.57, -30.66) * mm});
            skLineSegment(sketch, "E1109", {"start": v(156.57, -30.66) * mm, "end": v(155.77, -30.46) * mm});
            skLineSegment(sketch, "E1110", {"start": v(155.77, -30.46) * mm, "end": v(154.99, -30.25) * mm});
            skLineSegment(sketch, "E1111", {"start": v(154.99, -30.25) * mm, "end": v(154.23, -30.02) * mm});
            skLineSegment(sketch, "E1112", {"start": v(154.23, -30.02) * mm, "end": v(153.5, -29.77) * mm});
            skLineSegment(sketch, "E1113", {"start": v(153.5, -29.77) * mm, "end": v(152.77, -29.5) * mm});
            skLineSegment(sketch, "E1114", {"start": v(152.77, -29.5) * mm, "end": v(152.07, -29.2) * mm});
            skLineSegment(sketch, "E1115", {"start": v(152.07, -29.2) * mm, "end": v(151.4, -28.9) * mm});
            skLineSegment(sketch, "E1116", {"start": v(151.4, -28.9) * mm, "end": v(150.73, -28.58) * mm});
            skLineSegment(sketch, "E1117", {"start": v(150.73, -28.58) * mm, "end": v(150.1, -28.24) * mm});
            skLineSegment(sketch, "E1118", {"start": v(150.1, -28.24) * mm, "end": v(149.47, -27.87) * mm});
            skLineSegment(sketch, "E1119", {"start": v(149.47, -27.87) * mm, "end": v(148.86, -27.5) * mm});
            skLineSegment(sketch, "E1120", {"start": v(148.86, -27.5) * mm, "end": v(148.28, -27.1) * mm});
            skLineSegment(sketch, "E1121", {"start": v(148.28, -27.1) * mm, "end": v(147.71, -26.67) * mm});
            skLineSegment(sketch, "E1122", {"start": v(147.71, -26.67) * mm, "end": v(147.16, -26.24) * mm});
            skLineSegment(sketch, "E1123", {"start": v(147.16, -26.24) * mm, "end": v(146.63, -25.78) * mm});
            skLineSegment(sketch, "E1124", {"start": v(146.63, -25.78) * mm, "end": v(146.12, -25.3) * mm});
            skLineSegment(sketch, "E1125", {"start": v(146.12, -25.3) * mm, "end": v(145.63, -24.81) * mm});
            skLineSegment(sketch, "E1126", {"start": v(145.63, -24.81) * mm, "end": v(145.15, -24.3) * mm});
            skLineSegment(sketch, "E1127", {"start": v(145.15, -24.3) * mm, "end": v(144.7, -23.77) * mm});
            skLineSegment(sketch, "E1128", {"start": v(144.7, -23.77) * mm, "end": v(144.26, -23.22) * mm});
            skLineSegment(sketch, "E1129", {"start": v(144.26, -23.22) * mm, "end": v(143.84, -22.65) * mm});
            skLineSegment(sketch, "E1130", {"start": v(143.84, -22.65) * mm, "end": v(143.44, -22.07) * mm});
            skLineSegment(sketch, "E1131", {"start": v(143.44, -22.07) * mm, "end": v(143.06, -21.47) * mm});
            skLineSegment(sketch, "E1132", {"start": v(143.06, -21.47) * mm, "end": v(142.7, -20.86) * mm});
            skLineSegment(sketch, "E1133", {"start": v(142.7, -20.86) * mm, "end": v(142.37, -20.24) * mm});
            skLineSegment(sketch, "E1134", {"start": v(142.37, -20.24) * mm, "end": v(142.06, -19.6) * mm});
            skLineSegment(sketch, "E1135", {"start": v(142.06, -19.6) * mm, "end": v(141.77, -18.97) * mm});
            skLineSegment(sketch, "E1136", {"start": v(141.77, -18.97) * mm, "end": v(141.5, -18.32) * mm});
            skLineSegment(sketch, "E1137", {"start": v(141.5, -18.32) * mm, "end": v(141.27, -17.66) * mm});
            skLineSegment(sketch, "E1138", {"start": v(141.27, -17.66) * mm, "end": v(141.05, -16.99) * mm});
            skLineSegment(sketch, "E1139", {"start": v(141.05, -16.99) * mm, "end": v(140.85, -16.3) * mm});
            skLineSegment(sketch, "E1140", {"start": v(140.85, -16.3) * mm, "end": v(140.68, -15.62) * mm});
            skLineSegment(sketch, "E1141", {"start": v(140.68, -15.62) * mm, "end": v(140.53, -14.92) * mm});
            skLineSegment(sketch, "E1142", {"start": v(140.53, -14.92) * mm, "end": v(140.4, -14.21) * mm});
            skLineSegment(sketch, "E1143", {"start": v(140.4, -14.21) * mm, "end": v(140.3, -13.5) * mm});
            skLineSegment(sketch, "E1144", {"start": v(140.3, -13.5) * mm, "end": v(140.23, -12.77) * mm});
            skLineSegment(sketch, "E1145", {"start": v(140.23, -12.77) * mm, "end": v(140.17, -12.03) * mm});
            skLineSegment(sketch, "E1146", {"start": v(22.66, -10.18) * mm, "end": v(22.64, -8.83) * mm});
            skLineSegment(sketch, "E1147", {"start": v(22.64, -8.83) * mm, "end": v(22.66, -7.34) * mm});
            skLineSegment(sketch, "E1148", {"start": v(22.66, -7.34) * mm, "end": v(22.74, -5.9) * mm});
            skLineSegment(sketch, "E1149", {"start": v(22.74, -5.9) * mm, "end": v(22.87, -4.52) * mm});
            skLineSegment(sketch, "E1150", {"start": v(22.87, -4.52) * mm, "end": v(23.06, -3.18) * mm});
            skLineSegment(sketch, "E1151", {"start": v(23.06, -3.18) * mm, "end": v(23.3, -1.9) * mm});
            skLineSegment(sketch, "E1152", {"start": v(23.3, -1.9) * mm, "end": v(23.58, -0.65) * mm});
            skLineSegment(sketch, "E1153", {"start": v(23.58, -0.65) * mm, "end": v(23.92, 0.54) * mm});
            skLineSegment(sketch, "E1154", {"start": v(23.92, 0.54) * mm, "end": v(24.32, 1.68) * mm});
            skLineSegment(sketch, "E1155", {"start": v(24.32, 1.68) * mm, "end": v(24.76, 2.77) * mm});
            skLineSegment(sketch, "E1156", {"start": v(24.76, 2.77) * mm, "end": v(25.26, 3.82) * mm});
            skLineSegment(sketch, "E1157", {"start": v(25.26, 3.82) * mm, "end": v(25.81, 4.81) * mm});
            skLineSegment(sketch, "E1158", {"start": v(25.81, 4.81) * mm, "end": v(26.41, 5.76) * mm});
            skLineSegment(sketch, "E1159", {"start": v(26.41, 5.76) * mm, "end": v(27.07, 6.66) * mm});
            skLineSegment(sketch, "E1160", {"start": v(27.07, 6.66) * mm, "end": v(27.78, 7.5) * mm});
            skLineSegment(sketch, "E1161", {"start": v(27.78, 7.5) * mm, "end": v(28.54, 8.3) * mm});
            skLineSegment(sketch, "E1162", {"start": v(28.54, 8.3) * mm, "end": v(29.35, 9.06) * mm});
            skLineSegment(sketch, "E1163", {"start": v(29.35, 9.06) * mm, "end": v(30.06, 9.64) * mm});
            skLineSegment(sketch, "E1164", {"start": v(30.06, 9.64) * mm, "end": v(30.8, 10.19) * mm});
            skLineSegment(sketch, "E1165", {"start": v(30.8, 10.19) * mm, "end": v(31.54, 10.7) * mm});
            skLineSegment(sketch, "E1166", {"start": v(31.54, 10.7) * mm, "end": v(32.3, 11.17) * mm});
            skLineSegment(sketch, "E1167", {"start": v(32.3, 11.17) * mm, "end": v(33.1, 11.6) * mm});
            skLineSegment(sketch, "E1168", {"start": v(33.1, 11.6) * mm, "end": v(33.9, 12) * mm});
            skLineSegment(sketch, "E1169", {"start": v(33.9, 12) * mm, "end": v(34.73, 12.36) * mm});
            skLineSegment(sketch, "E1170", {"start": v(34.73, 12.36) * mm, "end": v(35.57, 12.68) * mm});
            skLineSegment(sketch, "E1171", {"start": v(35.57, 12.68) * mm, "end": v(36.44, 12.96) * mm});
            skLineSegment(sketch, "E1172", {"start": v(36.44, 12.96) * mm, "end": v(37.32, 13.2) * mm});
            skLineSegment(sketch, "E1173", {"start": v(37.32, 13.2) * mm, "end": v(38.22, 13.42) * mm});
            skLineSegment(sketch, "E1174", {"start": v(38.22, 13.42) * mm, "end": v(39.14, 13.59) * mm});
            skLineSegment(sketch, "E1175", {"start": v(39.14, 13.59) * mm, "end": v(40.08, 13.72) * mm});
            skLineSegment(sketch, "E1176", {"start": v(40.08, 13.72) * mm, "end": v(41.02, 13.8) * mm});
            skLineSegment(sketch, "E1177", {"start": v(41.02, 13.8) * mm, "end": v(41.02, 7.64) * mm});
            skLineSegment(sketch, "E1178", {"start": v(41.02, 7.64) * mm, "end": v(41.01, 7.64) * mm});
            skLineSegment(sketch, "E1179", {"start": v(41.01, 7.64) * mm, "end": v(40.38, 7.53) * mm});
            skLineSegment(sketch, "E1180", {"start": v(40.38, 7.53) * mm, "end": v(39.75, 7.39) * mm});
            skLineSegment(sketch, "E1181", {"start": v(39.75, 7.39) * mm, "end": v(39.14, 7.2) * mm});
            skLineSegment(sketch, "E1182", {"start": v(39.14, 7.2) * mm, "end": v(38.55, 7) * mm});
            skLineSegment(sketch, "E1183", {"start": v(38.55, 7) * mm, "end": v(37.97, 6.76) * mm});
            skLineSegment(sketch, "E1184", {"start": v(37.97, 6.76) * mm, "end": v(37.4, 6.48) * mm});
            skLineSegment(sketch, "E1185", {"start": v(37.4, 6.48) * mm, "end": v(36.85, 6.17) * mm});
            skLineSegment(sketch, "E1186", {"start": v(36.85, 6.17) * mm, "end": v(36.31, 5.84) * mm});
            skLineSegment(sketch, "E1187", {"start": v(36.31, 5.84) * mm, "end": v(35.8, 5.46) * mm});
            skLineSegment(sketch, "E1188", {"start": v(35.8, 5.46) * mm, "end": v(35.29, 5.06) * mm});
            skLineSegment(sketch, "E1189", {"start": v(35.29, 5.06) * mm, "end": v(34.8, 4.62) * mm});
            skLineSegment(sketch, "E1190", {"start": v(34.8, 4.62) * mm, "end": v(34.32, 4.16) * mm});
            skLineSegment(sketch, "E1191", {"start": v(34.32, 4.16) * mm, "end": v(33.85, 3.66) * mm});
            skLineSegment(sketch, "E1192", {"start": v(33.85, 3.66) * mm, "end": v(33.41, 3.12) * mm});
            skLineSegment(sketch, "E1193", {"start": v(33.41, 3.12) * mm, "end": v(33, 2.56) * mm});
            skLineSegment(sketch, "E1194", {"start": v(33, 2.56) * mm, "end": v(32.62, 1.96) * mm});
            skLineSegment(sketch, "E1195", {"start": v(32.62, 1.96) * mm, "end": v(32.26, 1.33) * mm});
            skLineSegment(sketch, "E1196", {"start": v(32.26, 1.33) * mm, "end": v(31.93, 0.66) * mm});
            skLineSegment(sketch, "E1197", {"start": v(31.93, 0.66) * mm, "end": v(31.63, -0.04) * mm});
            skLineSegment(sketch, "E1198", {"start": v(31.63, -0.04) * mm, "end": v(31.36, -0.77) * mm});
            skLineSegment(sketch, "E1199", {"start": v(31.36, -0.77) * mm, "end": v(31.12, -1.53) * mm});
            skLineSegment(sketch, "E1200", {"start": v(31.12, -1.53) * mm, "end": v(30.9, -2.33) * mm});
            skLineSegment(sketch, "E1201", {"start": v(30.9, -2.33) * mm, "end": v(30.72, -3.16) * mm});
            skLineSegment(sketch, "E1202", {"start": v(30.72, -3.16) * mm, "end": v(30.57, -4.02) * mm});
            skLineSegment(sketch, "E1203", {"start": v(30.57, -4.02) * mm, "end": v(30.44, -4.92) * mm});
            skLineSegment(sketch, "E1204", {"start": v(30.44, -4.92) * mm, "end": v(30.34, -5.84) * mm});
            skLineSegment(sketch, "E1205", {"start": v(30.34, -5.84) * mm, "end": v(30.27, -6.8) * mm});
            skLineSegment(sketch, "E1206", {"start": v(30.27, -6.8) * mm, "end": v(30.22, -7.8) * mm});
            skLineSegment(sketch, "E1207", {"start": v(30.22, -7.8) * mm, "end": v(30.21, -8.83) * mm});
            skLineSegment(sketch, "E1208", {"start": v(30.21, -8.83) * mm, "end": v(30.22, -9.85) * mm});
            skLineSegment(sketch, "E1209", {"start": v(30.22, -9.85) * mm, "end": v(30.27, -10.85) * mm});
            skLineSegment(sketch, "E1210", {"start": v(30.27, -10.85) * mm, "end": v(30.34, -11.81) * mm});
            skLineSegment(sketch, "E1211", {"start": v(30.34, -11.81) * mm, "end": v(30.44, -12.74) * mm});
            skLineSegment(sketch, "E1212", {"start": v(30.44, -12.74) * mm, "end": v(30.57, -13.64) * mm});
            skLineSegment(sketch, "E1213", {"start": v(30.57, -13.64) * mm, "end": v(30.72, -14.5) * mm});
            skLineSegment(sketch, "E1214", {"start": v(30.72, -14.5) * mm, "end": v(30.9, -15.33) * mm});
            skLineSegment(sketch, "E1215", {"start": v(30.9, -15.33) * mm, "end": v(31.12, -16.13) * mm});
            skLineSegment(sketch, "E1216", {"start": v(31.12, -16.13) * mm, "end": v(31.36, -16.9) * mm});
            skLineSegment(sketch, "E1217", {"start": v(31.36, -16.9) * mm, "end": v(31.63, -17.63) * mm});
            skLineSegment(sketch, "E1218", {"start": v(31.63, -17.63) * mm, "end": v(31.93, -18.32) * mm});
            skLineSegment(sketch, "E1219", {"start": v(31.93, -18.32) * mm, "end": v(32.26, -19) * mm});
            skLineSegment(sketch, "E1220", {"start": v(32.26, -19) * mm, "end": v(32.62, -19.63) * mm});
            skLineSegment(sketch, "E1221", {"start": v(32.62, -19.63) * mm, "end": v(33, -20.23) * mm});
            skLineSegment(sketch, "E1222", {"start": v(33, -20.23) * mm, "end": v(33.41, -20.8) * mm});
            skLineSegment(sketch, "E1223", {"start": v(33.41, -20.8) * mm, "end": v(33.85, -21.33) * mm});
            skLineSegment(sketch, "E1224", {"start": v(33.85, -21.33) * mm, "end": v(34.32, -21.83) * mm});
            skLineSegment(sketch, "E1225", {"start": v(34.32, -21.83) * mm, "end": v(34.8, -22.3) * mm});
            skLineSegment(sketch, "E1226", {"start": v(34.8, -22.3) * mm, "end": v(35.29, -22.74) * mm});
            skLineSegment(sketch, "E1227", {"start": v(35.29, -22.74) * mm, "end": v(35.8, -23.15) * mm});
            skLineSegment(sketch, "E1228", {"start": v(35.8, -23.15) * mm, "end": v(36.31, -23.52) * mm});
            skLineSegment(sketch, "E1229", {"start": v(36.31, -23.52) * mm, "end": v(36.85, -23.86) * mm});
            skLineSegment(sketch, "E1230", {"start": v(36.85, -23.86) * mm, "end": v(37.4, -24.17) * mm});
            skLineSegment(sketch, "E1231", {"start": v(37.4, -24.17) * mm, "end": v(37.97, -24.45) * mm});
            skLineSegment(sketch, "E1232", {"start": v(37.97, -24.45) * mm, "end": v(38.55, -24.69) * mm});
            skLineSegment(sketch, "E1233", {"start": v(38.55, -24.69) * mm, "end": v(39.14, -24.9) * mm});
            skLineSegment(sketch, "E1234", {"start": v(39.14, -24.9) * mm, "end": v(39.75, -25.08) * mm});
            skLineSegment(sketch, "E1235", {"start": v(39.75, -25.08) * mm, "end": v(40.38, -25.23) * mm});
            skLineSegment(sketch, "E1236", {"start": v(40.38, -25.23) * mm, "end": v(41.01, -25.34) * mm});
            skLineSegment(sketch, "E1237", {"start": v(41.01, -25.34) * mm, "end": v(41.02, -25.34) * mm});
            skLineSegment(sketch, "E1238", {"start": v(41.02, -25.34) * mm, "end": v(41.02, -31.46) * mm});
            skLineSegment(sketch, "E1239", {"start": v(41.02, -31.46) * mm, "end": v(40.8, -31.45) * mm});
            skLineSegment(sketch, "E1240", {"start": v(40.8, -31.45) * mm, "end": v(39.72, -31.34) * mm});
            skLineSegment(sketch, "E1241", {"start": v(39.72, -31.34) * mm, "end": v(38.68, -31.18) * mm});
            skLineSegment(sketch, "E1242", {"start": v(38.68, -31.18) * mm, "end": v(37.66, -30.97) * mm});
            skLineSegment(sketch, "E1243", {"start": v(37.66, -30.97) * mm, "end": v(36.67, -30.72) * mm});
            skLineSegment(sketch, "E1244", {"start": v(36.67, -30.72) * mm, "end": v(35.7, -30.42) * mm});
            skLineSegment(sketch, "E1245", {"start": v(35.7, -30.42) * mm, "end": v(34.77, -30.08) * mm});
            skLineSegment(sketch, "E1246", {"start": v(34.77, -30.08) * mm, "end": v(33.86, -29.7) * mm});
            skLineSegment(sketch, "E1247", {"start": v(33.86, -29.7) * mm, "end": v(32.98, -29.26) * mm});
            skLineSegment(sketch, "E1248", {"start": v(32.98, -29.26) * mm, "end": v(32.13, -28.78) * mm});
            skLineSegment(sketch, "E1249", {"start": v(32.13, -28.78) * mm, "end": v(31.3, -28.25) * mm});
            skLineSegment(sketch, "E1250", {"start": v(31.3, -28.25) * mm, "end": v(30.5, -27.68) * mm});
            skLineSegment(sketch, "E1251", {"start": v(30.5, -27.68) * mm, "end": v(29.73, -27.06) * mm});
            skLineSegment(sketch, "E1252", {"start": v(29.73, -27.06) * mm, "end": v(28.98, -26.4) * mm});
            skLineSegment(sketch, "E1253", {"start": v(28.98, -26.4) * mm, "end": v(28.27, -25.69) * mm});
            skLineSegment(sketch, "E1254", {"start": v(28.27, -25.69) * mm, "end": v(27.58, -24.94) * mm});
            skLineSegment(sketch, "E1255", {"start": v(27.58, -24.94) * mm, "end": v(26.95, -24.15) * mm});
            skLineSegment(sketch, "E1256", {"start": v(26.95, -24.15) * mm, "end": v(26.35, -23.31) * mm});
            skLineSegment(sketch, "E1257", {"start": v(26.35, -23.31) * mm, "end": v(25.8, -22.44) * mm});
            skLineSegment(sketch, "E1258", {"start": v(25.8, -22.44) * mm, "end": v(25.3, -21.53) * mm});
            skLineSegment(sketch, "E1259", {"start": v(25.3, -21.53) * mm, "end": v(24.84, -20.57) * mm});
            skLineSegment(sketch, "E1260", {"start": v(24.84, -20.57) * mm, "end": v(24.42, -19.58) * mm});
            skLineSegment(sketch, "E1261", {"start": v(24.42, -19.58) * mm, "end": v(24.05, -18.55) * mm});
            skLineSegment(sketch, "E1262", {"start": v(24.05, -18.55) * mm, "end": v(23.72, -17.47) * mm});
            skLineSegment(sketch, "E1263", {"start": v(23.72, -17.47) * mm, "end": v(23.43, -16.36) * mm});
            skLineSegment(sketch, "E1264", {"start": v(23.43, -16.36) * mm, "end": v(23.19, -15.2) * mm});
            skLineSegment(sketch, "E1265", {"start": v(23.19, -15.2) * mm, "end": v(23, -14) * mm});
            skLineSegment(sketch, "E1266", {"start": v(23, -14) * mm, "end": v(22.84, -12.77) * mm});
            skLineSegment(sketch, "E1267", {"start": v(22.84, -12.77) * mm, "end": v(22.73, -11.5) * mm});
            skLineSegment(sketch, "E1268", {"start": v(22.73, -11.5) * mm, "end": v(22.66, -10.18) * mm});
            skLineSegment(sketch, "E1269", {"start": v(-37.07, -30.56) * mm, "end": v(-44.44, -30.56) * mm});
            skLineSegment(sketch, "E1270", {"start": v(-44.44, -30.56) * mm, "end": v(-44.44, 12.9) * mm});
            skLineSegment(sketch, "E1271", {"start": v(-44.44, 12.9) * mm, "end": v(-37.85, 12.9) * mm});
            skLineSegment(sketch, "E1272", {"start": v(-37.85, 12.9) * mm, "end": v(-37.85, 6.8) * mm});
            skLineSegment(sketch, "E1273", {"start": v(-37.85, 6.8) * mm, "end": v(-37.32, 7.59) * mm});
            skLineSegment(sketch, "E1274", {"start": v(-37.32, 7.59) * mm, "end": v(-36.74, 8.33) * mm});
            skLineSegment(sketch, "E1275", {"start": v(-36.74, 8.33) * mm, "end": v(-36.13, 9.03) * mm});
            skLineSegment(sketch, "E1276", {"start": v(-36.13, 9.03) * mm, "end": v(-35.47, 9.69) * mm});
            skLineSegment(sketch, "E1277", {"start": v(-35.47, 9.69) * mm, "end": v(-34.77, 10.3) * mm});
            skLineSegment(sketch, "E1278", {"start": v(-34.77, 10.3) * mm, "end": v(-34.02, 10.9) * mm});
            skLineSegment(sketch, "E1279", {"start": v(-34.02, 10.9) * mm, "end": v(-33.24, 11.44) * mm});
            skLineSegment(sketch, "E1280", {"start": v(-33.24, 11.44) * mm, "end": v(-32.4, 11.94) * mm});
            skLineSegment(sketch, "E1281", {"start": v(-32.4, 11.94) * mm, "end": v(-31.55, 12.4) * mm});
            skLineSegment(sketch, "E1282", {"start": v(-31.55, 12.4) * mm, "end": v(-30.65, 12.8) * mm});
            skLineSegment(sketch, "E1283", {"start": v(-30.65, 12.8) * mm, "end": v(-29.73, 13.13) * mm});
            skLineSegment(sketch, "E1284", {"start": v(-29.73, 13.13) * mm, "end": v(-28.78, 13.4) * mm});
            skLineSegment(sketch, "E1285", {"start": v(-28.78, 13.4) * mm, "end": v(-27.8, 13.61) * mm});
            skLineSegment(sketch, "E1286", {"start": v(-27.8, 13.61) * mm, "end": v(-26.78, 13.77) * mm});
            skLineSegment(sketch, "E1287", {"start": v(-26.78, 13.77) * mm, "end": v(-25.74, 13.86) * mm});
            skLineSegment(sketch, "E1288", {"start": v(-25.74, 13.86) * mm, "end": v(-24.67, 13.89) * mm});
            skLineSegment(sketch, "E1289", {"start": v(-24.67, 13.89) * mm, "end": v(-23.5, 13.86) * mm});
            skLineSegment(sketch, "E1290", {"start": v(-23.5, 13.86) * mm, "end": v(-22.37, 13.76) * mm});
            skLineSegment(sketch, "E1291", {"start": v(-22.37, 13.76) * mm, "end": v(-21.3, 13.6) * mm});
            skLineSegment(sketch, "E1292", {"start": v(-21.3, 13.6) * mm, "end": v(-20.28, 13.39) * mm});
            skLineSegment(sketch, "E1293", {"start": v(-20.28, 13.39) * mm, "end": v(-19.32, 13.1) * mm});
            skLineSegment(sketch, "E1294", {"start": v(-19.32, 13.1) * mm, "end": v(-18.4, 12.76) * mm});
            skLineSegment(sketch, "E1295", {"start": v(-18.4, 12.76) * mm, "end": v(-17.55, 12.35) * mm});
            skLineSegment(sketch, "E1296", {"start": v(-17.55, 12.35) * mm, "end": v(-16.75, 11.88) * mm});
            skLineSegment(sketch, "E1297", {"start": v(-16.75, 11.88) * mm, "end": v(-16.01, 11.36) * mm});
            skLineSegment(sketch, "E1298", {"start": v(-16.01, 11.36) * mm, "end": v(-15.32, 10.78) * mm});
            skLineSegment(sketch, "E1299", {"start": v(-15.32, 10.78) * mm, "end": v(-14.7, 10.15) * mm});
            skLineSegment(sketch, "E1300", {"start": v(-14.7, 10.15) * mm, "end": v(-14.12, 9.48) * mm});
            skLineSegment(sketch, "E1301", {"start": v(-14.12, 9.48) * mm, "end": v(-13.6, 8.75) * mm});
            skLineSegment(sketch, "E1302", {"start": v(-13.6, 8.75) * mm, "end": v(-13.14, 7.98) * mm});
            skLineSegment(sketch, "E1303", {"start": v(-13.14, 7.98) * mm, "end": v(-12.74, 7.15) * mm});
            skLineSegment(sketch, "E1304", {"start": v(-12.74, 7.15) * mm, "end": v(-12.4, 6.27) * mm});
            skLineSegment(sketch, "E1305", {"start": v(-12.4, 6.27) * mm, "end": v(-11.74, 7.2) * mm});
            skLineSegment(sketch, "E1306", {"start": v(-11.74, 7.2) * mm, "end": v(-11.06, 8.06) * mm});
            skLineSegment(sketch, "E1307", {"start": v(-11.06, 8.06) * mm, "end": v(-10.35, 8.86) * mm});
            skLineSegment(sketch, "E1308", {"start": v(-10.35, 8.86) * mm, "end": v(-9.62, 9.6) * mm});
            skLineSegment(sketch, "E1309", {"start": v(-9.62, 9.6) * mm, "end": v(-8.87, 10.29) * mm});
            skLineSegment(sketch, "E1310", {"start": v(-8.87, 10.29) * mm, "end": v(-8.1, 10.91) * mm});
            skLineSegment(sketch, "E1311", {"start": v(-8.1, 10.91) * mm, "end": v(-7.29, 11.48) * mm});
            skLineSegment(sketch, "E1312", {"start": v(-7.29, 11.48) * mm, "end": v(-6.46, 11.98) * mm});
            skLineSegment(sketch, "E1313", {"start": v(-6.46, 11.98) * mm, "end": v(-5.6, 12.43) * mm});
            skLineSegment(sketch, "E1314", {"start": v(-5.6, 12.43) * mm, "end": v(-4.73, 12.82) * mm});
            skLineSegment(sketch, "E1315", {"start": v(-4.73, 12.82) * mm, "end": v(-3.83, 13.14) * mm});
            skLineSegment(sketch, "E1316", {"start": v(-3.83, 13.14) * mm, "end": v(-2.91, 13.41) * mm});
            skLineSegment(sketch, "E1317", {"start": v(-2.91, 13.41) * mm, "end": v(-1.96, 13.62) * mm});
            skLineSegment(sketch, "E1318", {"start": v(-1.96, 13.62) * mm, "end": v(-0.99, 13.77) * mm});
            skLineSegment(sketch, "E1319", {"start": v(-0.99, 13.77) * mm, "end": v(0, 13.86) * mm});
            skLineSegment(sketch, "E1320", {"start": v(0, 13.86) * mm, "end": v(1.03, 13.89) * mm});
            skLineSegment(sketch, "E1321", {"start": v(1.03, 13.89) * mm, "end": v(1.83, 13.87) * mm});
            skLineSegment(sketch, "E1322", {"start": v(1.83, 13.87) * mm, "end": v(2.6, 13.83) * mm});
            skLineSegment(sketch, "E1323", {"start": v(2.6, 13.83) * mm, "end": v(3.35, 13.76) * mm});
            skLineSegment(sketch, "E1324", {"start": v(3.35, 13.76) * mm, "end": v(4.08, 13.66) * mm});
            skLineSegment(sketch, "E1325", {"start": v(4.08, 13.66) * mm, "end": v(4.78, 13.54) * mm});
            skLineSegment(sketch, "E1326", {"start": v(4.78, 13.54) * mm, "end": v(5.46, 13.38) * mm});
            skLineSegment(sketch, "E1327", {"start": v(5.46, 13.38) * mm, "end": v(6.12, 13.2) * mm});
            skLineSegment(sketch, "E1328", {"start": v(6.12, 13.2) * mm, "end": v(6.75, 13) * mm});
            skLineSegment(sketch, "E1329", {"start": v(6.75, 13) * mm, "end": v(7.36, 12.75) * mm});
            skLineSegment(sketch, "E1330", {"start": v(7.36, 12.75) * mm, "end": v(7.95, 12.49) * mm});
            skLineSegment(sketch, "E1331", {"start": v(7.95, 12.49) * mm, "end": v(8.5, 12.2) * mm});
            skLineSegment(sketch, "E1332", {"start": v(8.5, 12.2) * mm, "end": v(9.05, 11.87) * mm});
            skLineSegment(sketch, "E1333", {"start": v(9.05, 11.87) * mm, "end": v(9.56, 11.52) * mm});
            skLineSegment(sketch, "E1334", {"start": v(9.56, 11.52) * mm, "end": v(10.06, 11.15) * mm});
            skLineSegment(sketch, "E1335", {"start": v(10.06, 11.15) * mm, "end": v(10.53, 10.74) * mm});
            skLineSegment(sketch, "E1336", {"start": v(10.53, 10.74) * mm, "end": v(10.97, 10.3) * mm});
            skLineSegment(sketch, "E1337", {"start": v(10.97, 10.3) * mm, "end": v(11.4, 9.84) * mm});
            skLineSegment(sketch, "E1338", {"start": v(11.4, 9.84) * mm, "end": v(11.79, 9.35) * mm});
            skLineSegment(sketch, "E1339", {"start": v(11.79, 9.35) * mm, "end": v(12.16, 8.83) * mm});
            skLineSegment(sketch, "E1340", {"start": v(12.16, 8.83) * mm, "end": v(12.5, 8.27) * mm});
            skLineSegment(sketch, "E1341", {"start": v(12.5, 8.27) * mm, "end": v(12.8, 7.7) * mm});
            skLineSegment(sketch, "E1342", {"start": v(12.8, 7.7) * mm, "end": v(13.1, 7.08) * mm});
            skLineSegment(sketch, "E1343", {"start": v(13.1, 7.08) * mm, "end": v(13.35, 6.43) * mm});
            skLineSegment(sketch, "E1344", {"start": v(13.35, 6.43) * mm, "end": v(13.58, 5.76) * mm});
            skLineSegment(sketch, "E1345", {"start": v(13.58, 5.76) * mm, "end": v(13.79, 5.05) * mm});
            skLineSegment(sketch, "E1346", {"start": v(13.79, 5.05) * mm, "end": v(13.96, 4.32) * mm});
            skLineSegment(sketch, "E1347", {"start": v(13.96, 4.32) * mm, "end": v(14.11, 3.55) * mm});
            skLineSegment(sketch, "E1348", {"start": v(14.11, 3.55) * mm, "end": v(14.24, 2.76) * mm});
            skLineSegment(sketch, "E1349", {"start": v(14.24, 2.76) * mm, "end": v(14.33, 1.93) * mm});
            skLineSegment(sketch, "E1350", {"start": v(14.33, 1.93) * mm, "end": v(14.4, 1.08) * mm});
            skLineSegment(sketch, "E1351", {"start": v(14.4, 1.08) * mm, "end": v(14.44, 0.2) * mm});
            skLineSegment(sketch, "E1352", {"start": v(14.44, 0.2) * mm, "end": v(14.45, -0.72) * mm});
            skLineSegment(sketch, "E1353", {"start": v(14.45, -0.72) * mm, "end": v(14.45, -30.56) * mm});
            skLineSegment(sketch, "E1354", {"start": v(14.45, -30.56) * mm, "end": v(7.13, -30.56) * mm});
            skLineSegment(sketch, "E1355", {"start": v(7.13, -30.56) * mm, "end": v(7.13, -3.18) * mm});
            skLineSegment(sketch, "E1356", {"start": v(7.13, -3.18) * mm, "end": v(7.12, -2.11) * mm});
            skLineSegment(sketch, "E1357", {"start": v(7.12, -2.11) * mm, "end": v(7.08, -1.12) * mm});
            skLineSegment(sketch, "E1358", {"start": v(7.08, -1.12) * mm, "end": v(7.03, -0.21) * mm});
            skLineSegment(sketch, "E1359", {"start": v(7.03, -0.21) * mm, "end": v(6.95, 0.62) * mm});
            skLineSegment(sketch, "E1360", {"start": v(6.95, 0.62) * mm, "end": v(6.85, 1.38) * mm});
            skLineSegment(sketch, "E1361", {"start": v(6.85, 1.38) * mm, "end": v(6.72, 2.06) * mm});
            skLineSegment(sketch, "E1362", {"start": v(6.72, 2.06) * mm, "end": v(6.58, 2.66) * mm});
            skLineSegment(sketch, "E1363", {"start": v(6.58, 2.66) * mm, "end": v(6.41, 3.18) * mm});
            skLineSegment(sketch, "E1364", {"start": v(6.41, 3.18) * mm, "end": v(6.21, 3.66) * mm});
            skLineSegment(sketch, "E1365", {"start": v(6.21, 3.66) * mm, "end": v(5.98, 4.1) * mm});
            skLineSegment(sketch, "E1366", {"start": v(5.98, 4.1) * mm, "end": v(5.7, 4.54) * mm});
            skLineSegment(sketch, "E1367", {"start": v(5.7, 4.54) * mm, "end": v(5.4, 4.94) * mm});
            skLineSegment(sketch, "E1368", {"start": v(5.4, 4.94) * mm, "end": v(5.06, 5.32) * mm});
            skLineSegment(sketch, "E1369", {"start": v(5.06, 5.32) * mm, "end": v(4.68, 5.68) * mm});
            skLineSegment(sketch, "E1370", {"start": v(4.68, 5.68) * mm, "end": v(4.26, 6) * mm});
            skLineSegment(sketch, "E1371", {"start": v(4.26, 6) * mm, "end": v(3.81, 6.32) * mm});
            skLineSegment(sketch, "E1372", {"start": v(3.81, 6.32) * mm, "end": v(3.33, 6.6) * mm});
            skLineSegment(sketch, "E1373", {"start": v(3.33, 6.6) * mm, "end": v(2.83, 6.84) * mm});
            skLineSegment(sketch, "E1374", {"start": v(2.83, 6.84) * mm, "end": v(2.3, 7.04) * mm});
            skLineSegment(sketch, "E1375", {"start": v(2.3, 7.04) * mm, "end": v(1.77, 7.2) * mm});
            skLineSegment(sketch, "E1376", {"start": v(1.77, 7.2) * mm, "end": v(1.2, 7.34) * mm});
            skLineSegment(sketch, "E1377", {"start": v(1.2, 7.34) * mm, "end": v(0.62, 7.43) * mm});
            skLineSegment(sketch, "E1378", {"start": v(0.62, 7.43) * mm, "end": v(0.02, 7.48) * mm});
            skLineSegment(sketch, "E1379", {"start": v(0.02, 7.48) * mm, "end": v(-0.6, 7.5) * mm});
            skLineSegment(sketch, "E1380", {"start": v(-0.6, 7.5) * mm, "end": v(-1.18, 7.5) * mm});
            skLineSegment(sketch, "E1381", {"start": v(-1.18, 7.5) * mm, "end": v(-1.73, 7.46) * mm});
            skLineSegment(sketch, "E1382", {"start": v(-1.73, 7.46) * mm, "end": v(-2.27, 7.4) * mm});
            skLineSegment(sketch, "E1383", {"start": v(-2.27, 7.4) * mm, "end": v(-2.8, 7.31) * mm});
            skLineSegment(sketch, "E1384", {"start": v(-2.8, 7.31) * mm, "end": v(-3.32, 7.2) * mm});
            skLineSegment(sketch, "E1385", {"start": v(-3.32, 7.2) * mm, "end": v(-3.83, 7.07) * mm});
            skLineSegment(sketch, "E1386", {"start": v(-3.83, 7.07) * mm, "end": v(-4.32, 6.92) * mm});
            skLineSegment(sketch, "E1387", {"start": v(-4.32, 6.92) * mm, "end": v(-4.8, 6.74) * mm});
            skLineSegment(sketch, "E1388", {"start": v(-4.8, 6.74) * mm, "end": v(-5.27, 6.54) * mm});
            skLineSegment(sketch, "E1389", {"start": v(-5.27, 6.54) * mm, "end": v(-5.73, 6.31) * mm});
            skLineSegment(sketch, "E1390", {"start": v(-5.73, 6.31) * mm, "end": v(-6.18, 6.06) * mm});
            skLineSegment(sketch, "E1391", {"start": v(-6.18, 6.06) * mm, "end": v(-6.6, 5.79) * mm});
            skLineSegment(sketch, "E1392", {"start": v(-6.6, 5.79) * mm, "end": v(-7.03, 5.49) * mm});
            skLineSegment(sketch, "E1393", {"start": v(-7.03, 5.49) * mm, "end": v(-7.44, 5.17) * mm});
            skLineSegment(sketch, "E1394", {"start": v(-7.44, 5.17) * mm, "end": v(-7.84, 4.82) * mm});
            skLineSegment(sketch, "E1395", {"start": v(-7.84, 4.82) * mm, "end": v(-8.22, 4.45) * mm});
            skLineSegment(sketch, "E1396", {"start": v(-8.22, 4.45) * mm, "end": v(-8.59, 4.06) * mm});
            skLineSegment(sketch, "E1397", {"start": v(-8.59, 4.06) * mm, "end": v(-8.93, 3.63) * mm});
            skLineSegment(sketch, "E1398", {"start": v(-8.93, 3.63) * mm, "end": v(-9.25, 3.18) * mm});
            skLineSegment(sketch, "E1399", {"start": v(-9.25, 3.18) * mm, "end": v(-9.55, 2.7) * mm});
            skLineSegment(sketch, "E1400", {"start": v(-9.55, 2.7) * mm, "end": v(-9.82, 2.2) * mm});
            skLineSegment(sketch, "E1401", {"start": v(-9.82, 2.2) * mm, "end": v(-10.07, 1.65) * mm});
            skLineSegment(sketch, "E1402", {"start": v(-10.07, 1.65) * mm, "end": v(-10.3, 1.08) * mm});
            skLineSegment(sketch, "E1403", {"start": v(-10.3, 1.08) * mm, "end": v(-10.5, 0.49) * mm});
            skLineSegment(sketch, "E1404", {"start": v(-10.5, 0.49) * mm, "end": v(-10.67, -0.14) * mm});
            skLineSegment(sketch, "E1405", {"start": v(-10.67, -0.14) * mm, "end": v(-10.82, -0.79) * mm});
            skLineSegment(sketch, "E1406", {"start": v(-10.82, -0.79) * mm, "end": v(-10.95, -1.47) * mm});
            skLineSegment(sketch, "E1407", {"start": v(-10.95, -1.47) * mm, "end": v(-11.06, -2.18) * mm});
            skLineSegment(sketch, "E1408", {"start": v(-11.06, -2.18) * mm, "end": v(-11.14, -2.92) * mm});
            skLineSegment(sketch, "E1409", {"start": v(-11.14, -2.92) * mm, "end": v(-11.2, -3.69) * mm});
            skLineSegment(sketch, "E1410", {"start": v(-11.2, -3.69) * mm, "end": v(-11.24, -4.48) * mm});
            skLineSegment(sketch, "E1411", {"start": v(-11.24, -4.48) * mm, "end": v(-11.25, -5.3) * mm});
            skLineSegment(sketch, "E1412", {"start": v(-11.25, -5.3) * mm, "end": v(-11.25, -30.56) * mm});
            skLineSegment(sketch, "E1413", {"start": v(-11.25, -30.56) * mm, "end": v(-18.62, -30.56) * mm});
            skLineSegment(sketch, "E1414", {"start": v(-18.62, -30.56) * mm, "end": v(-18.62, -2.32) * mm});
            skLineSegment(sketch, "E1415", {"start": v(-18.62, -2.32) * mm, "end": v(-18.64, -1.13) * mm});
            skLineSegment(sketch, "E1416", {"start": v(-18.64, -1.13) * mm, "end": v(-18.73, -0.02) * mm});
            skLineSegment(sketch, "E1417", {"start": v(-18.73, -0.02) * mm, "end": v(-18.87, 1.02) * mm});
            skLineSegment(sketch, "E1418", {"start": v(-18.87, 1.02) * mm, "end": v(-19.07, 1.98) * mm});
            skLineSegment(sketch, "E1419", {"start": v(-19.07, 1.98) * mm, "end": v(-19.32, 2.86) * mm});
            skLineSegment(sketch, "E1420", {"start": v(-19.32, 2.86) * mm, "end": v(-19.63, 3.67) * mm});
            skLineSegment(sketch, "E1421", {"start": v(-19.63, 3.67) * mm, "end": v(-20, 4.4) * mm});
            skLineSegment(sketch, "E1422", {"start": v(-20, 4.4) * mm, "end": v(-20.42, 5.05) * mm});
            skLineSegment(sketch, "E1423", {"start": v(-20.42, 5.05) * mm, "end": v(-20.65, 5.34) * mm});
            skLineSegment(sketch, "E1424", {"start": v(-20.65, 5.34) * mm, "end": v(-20.9, 5.62) * mm});
            skLineSegment(sketch, "E1425", {"start": v(-20.9, 5.62) * mm, "end": v(-21.17, 5.88) * mm});
            skLineSegment(sketch, "E1426", {"start": v(-21.17, 5.88) * mm, "end": v(-21.46, 6.12) * mm});
            skLineSegment(sketch, "E1427", {"start": v(-21.46, 6.12) * mm, "end": v(-21.77, 6.34) * mm});
            skLineSegment(sketch, "E1428", {"start": v(-21.77, 6.34) * mm, "end": v(-22.1, 6.54) * mm});
            skLineSegment(sketch, "E1429", {"start": v(-22.1, 6.54) * mm, "end": v(-22.43, 6.73) * mm});
            skLineSegment(sketch, "E1430", {"start": v(-22.43, 6.73) * mm, "end": v(-22.8, 6.89) * mm});
            skLineSegment(sketch, "E1431", {"start": v(-22.8, 6.89) * mm, "end": v(-23.17, 7.03) * mm});
            skLineSegment(sketch, "E1432", {"start": v(-23.17, 7.03) * mm, "end": v(-23.56, 7.16) * mm});
            skLineSegment(sketch, "E1433", {"start": v(-23.56, 7.16) * mm, "end": v(-23.98, 7.26) * mm});
            skLineSegment(sketch, "E1434", {"start": v(-23.98, 7.26) * mm, "end": v(-24.4, 7.35) * mm});
            skLineSegment(sketch, "E1435", {"start": v(-24.4, 7.35) * mm, "end": v(-24.86, 7.42) * mm});
            skLineSegment(sketch, "E1436", {"start": v(-24.86, 7.42) * mm, "end": v(-25.32, 7.46) * mm});
            skLineSegment(sketch, "E1437", {"start": v(-25.32, 7.46) * mm, "end": v(-25.8, 7.5) * mm});
            skLineSegment(sketch, "E1438", {"start": v(-25.8, 7.5) * mm, "end": v(-26.31, 7.5) * mm});
            skLineSegment(sketch, "E1439", {"start": v(-26.31, 7.5) * mm, "end": v(-27.08, 7.48) * mm});
            skLineSegment(sketch, "E1440", {"start": v(-27.08, 7.48) * mm, "end": v(-27.84, 7.4) * mm});
            skLineSegment(sketch, "E1441", {"start": v(-27.84, 7.4) * mm, "end": v(-28.58, 7.27) * mm});
            skLineSegment(sketch, "E1442", {"start": v(-28.58, 7.27) * mm, "end": v(-29.3, 7.1) * mm});
            skLineSegment(sketch, "E1443", {"start": v(-29.3, 7.1) * mm, "end": v(-30.02, 6.86) * mm});
            skLineSegment(sketch, "E1444", {"start": v(-30.02, 6.86) * mm, "end": v(-30.71, 6.58) * mm});
            skLineSegment(sketch, "E1445", {"start": v(-30.71, 6.58) * mm, "end": v(-31.4, 6.25) * mm});
            skLineSegment(sketch, "E1446", {"start": v(-31.4, 6.25) * mm, "end": v(-32.06, 5.87) * mm});
            skLineSegment(sketch, "E1447", {"start": v(-32.06, 5.87) * mm, "end": v(-32.7, 5.43) * mm});
            skLineSegment(sketch, "E1448", {"start": v(-32.7, 5.43) * mm, "end": v(-33.3, 4.95) * mm});
            skLineSegment(sketch, "E1449", {"start": v(-33.3, 4.95) * mm, "end": v(-33.84, 4.42) * mm});
            skLineSegment(sketch, "E1450", {"start": v(-33.84, 4.42) * mm, "end": v(-34.34, 3.85) * mm});
            skLineSegment(sketch, "E1451", {"start": v(-34.34, 3.85) * mm, "end": v(-34.8, 3.23) * mm});
            skLineSegment(sketch, "E1452", {"start": v(-34.8, 3.23) * mm, "end": v(-35.2, 2.56) * mm});
            skLineSegment(sketch, "E1453", {"start": v(-35.2, 2.56) * mm, "end": v(-35.57, 1.84) * mm});
            skLineSegment(sketch, "E1454", {"start": v(-35.57, 1.84) * mm, "end": v(-35.89, 1.08) * mm});
            skLineSegment(sketch, "E1455", {"start": v(-35.89, 1.08) * mm, "end": v(-36.17, 0.25) * mm});
            skLineSegment(sketch, "E1456", {"start": v(-36.17, 0.25) * mm, "end": v(-36.4, -0.67) * mm});
            skLineSegment(sketch, "E1457", {"start": v(-36.4, -0.67) * mm, "end": v(-36.61, -1.68) * mm});
            skLineSegment(sketch, "E1458", {"start": v(-36.61, -1.68) * mm, "end": v(-36.78, -2.77) * mm});
            skLineSegment(sketch, "E1459", {"start": v(-36.78, -2.77) * mm, "end": v(-36.9, -3.95) * mm});
            skLineSegment(sketch, "E1460", {"start": v(-36.9, -3.95) * mm, "end": v(-37, -5.22) * mm});
            skLineSegment(sketch, "E1461", {"start": v(-37, -5.22) * mm, "end": v(-37.06, -6.57) * mm});
            skLineSegment(sketch, "E1462", {"start": v(-37.06, -6.57) * mm, "end": v(-37.07, -8) * mm});
            skLineSegment(sketch, "E1463", {"start": v(-37.07, -8) * mm, "end": v(-37.07, -30.56) * mm});
            skLineSegment(sketch, "E1464", {"start": v(-130.3, -30.56) * mm, "end": v(-137.68, -30.56) * mm});
            skLineSegment(sketch, "E1465", {"start": v(-137.68, -30.56) * mm, "end": v(-137.68, 12.9) * mm});
            skLineSegment(sketch, "E1466", {"start": v(-137.68, 12.9) * mm, "end": v(-131.04, 12.9) * mm});
            skLineSegment(sketch, "E1467", {"start": v(-131.04, 12.9) * mm, "end": v(-131.04, 6.73) * mm});
            skLineSegment(sketch, "E1468", {"start": v(-131.04, 6.73) * mm, "end": v(-130.43, 7.6) * mm});
            skLineSegment(sketch, "E1469", {"start": v(-130.43, 7.6) * mm, "end": v(-129.78, 8.4) * mm});
            skLineSegment(sketch, "E1470", {"start": v(-129.78, 8.4) * mm, "end": v(-129.1, 9.16) * mm});
            skLineSegment(sketch, "E1471", {"start": v(-129.1, 9.16) * mm, "end": v(-128.38, 9.86) * mm});
            skLineSegment(sketch, "E1472", {"start": v(-128.38, 9.86) * mm, "end": v(-127.64, 10.5) * mm});
            skLineSegment(sketch, "E1473", {"start": v(-127.64, 10.5) * mm, "end": v(-126.85, 11.09) * mm});
            skLineSegment(sketch, "E1474", {"start": v(-126.85, 11.09) * mm, "end": v(-126.04, 11.62) * mm});
            skLineSegment(sketch, "E1475", {"start": v(-126.04, 11.62) * mm, "end": v(-125.2, 12.1) * mm});
            skLineSegment(sketch, "E1476", {"start": v(-125.2, 12.1) * mm, "end": v(-124.31, 12.52) * mm});
            skLineSegment(sketch, "E1477", {"start": v(-124.31, 12.52) * mm, "end": v(-123.4, 12.88) * mm});
            skLineSegment(sketch, "E1478", {"start": v(-123.4, 12.88) * mm, "end": v(-122.45, 13.19) * mm});
            skLineSegment(sketch, "E1479", {"start": v(-122.45, 13.19) * mm, "end": v(-121.47, 13.44) * mm});
            skLineSegment(sketch, "E1480", {"start": v(-121.47, 13.44) * mm, "end": v(-120.45, 13.64) * mm});
            skLineSegment(sketch, "E1481", {"start": v(-120.45, 13.64) * mm, "end": v(-119.4, 13.78) * mm});
            skLineSegment(sketch, "E1482", {"start": v(-119.4, 13.78) * mm, "end": v(-118.33, 13.86) * mm});
            skLineSegment(sketch, "E1483", {"start": v(-118.33, 13.86) * mm, "end": v(-117.21, 13.89) * mm});
            skLineSegment(sketch, "E1484", {"start": v(-117.21, 13.89) * mm, "end": v(-116.24, 13.87) * mm});
            skLineSegment(sketch, "E1485", {"start": v(-116.24, 13.87) * mm, "end": v(-115.29, 13.8) * mm});
            skLineSegment(sketch, "E1486", {"start": v(-115.29, 13.8) * mm, "end": v(-114.35, 13.69) * mm});
            skLineSegment(sketch, "E1487", {"start": v(-114.35, 13.69) * mm, "end": v(-113.44, 13.53) * mm});
            skLineSegment(sketch, "E1488", {"start": v(-113.44, 13.53) * mm, "end": v(-112.55, 13.34) * mm});
            skLineSegment(sketch, "E1489", {"start": v(-112.55, 13.34) * mm, "end": v(-111.67, 13.1) * mm});
            skLineSegment(sketch, "E1490", {"start": v(-111.67, 13.1) * mm, "end": v(-110.82, 12.8) * mm});
            skLineSegment(sketch, "E1491", {"start": v(-110.82, 12.8) * mm, "end": v(-109.99, 12.48) * mm});
            skLineSegment(sketch, "E1492", {"start": v(-109.99, 12.48) * mm, "end": v(-109.19, 12.1) * mm});
            skLineSegment(sketch, "E1493", {"start": v(-109.19, 12.1) * mm, "end": v(-108.44, 11.71) * mm});
            skLineSegment(sketch, "E1494", {"start": v(-108.44, 11.71) * mm, "end": v(-107.75, 11.3) * mm});
            skLineSegment(sketch, "E1495", {"start": v(-107.75, 11.3) * mm, "end": v(-107.1, 10.84) * mm});
            skLineSegment(sketch, "E1496", {"start": v(-107.1, 10.84) * mm, "end": v(-106.52, 10.37) * mm});
            skLineSegment(sketch, "E1497", {"start": v(-106.52, 10.37) * mm, "end": v(-105.98, 9.86) * mm});
            skLineSegment(sketch, "E1498", {"start": v(-105.98, 9.86) * mm, "end": v(-105.5, 9.33) * mm});
            skLineSegment(sketch, "E1499", {"start": v(-105.5, 9.33) * mm, "end": v(-105.06, 8.77) * mm});
            skLineSegment(sketch, "E1500", {"start": v(-105.06, 8.77) * mm, "end": v(-104.66, 8.19) * mm});
            skLineSegment(sketch, "E1501", {"start": v(-104.66, 8.19) * mm, "end": v(-104.3, 7.57) * mm});
            skLineSegment(sketch, "E1502", {"start": v(-104.3, 7.57) * mm, "end": v(-103.97, 6.93) * mm});
            skLineSegment(sketch, "E1503", {"start": v(-103.97, 6.93) * mm, "end": v(-103.66, 6.26) * mm});
            skLineSegment(sketch, "E1504", {"start": v(-103.66, 6.26) * mm, "end": v(-103.4, 5.57) * mm});
            skLineSegment(sketch, "E1505", {"start": v(-103.4, 5.57) * mm, "end": v(-103.15, 4.85) * mm});
            skLineSegment(sketch, "E1506", {"start": v(-103.15, 4.85) * mm, "end": v(-102.94, 4.1) * mm});
            skLineSegment(sketch, "E1507", {"start": v(-102.94, 4.1) * mm, "end": v(-102.76, 3.33) * mm});
            skLineSegment(sketch, "E1508", {"start": v(-102.76, 3.33) * mm, "end": v(-102.71, 3.06) * mm});
            skLineSegment(sketch, "E1509", {"start": v(-102.71, 3.06) * mm, "end": v(-102.67, 2.77) * mm});
            skLineSegment(sketch, "E1510", {"start": v(-102.67, 2.77) * mm, "end": v(-102.62, 2.45) * mm});
            skLineSegment(sketch, "E1511", {"start": v(-102.62, 2.45) * mm, "end": v(-102.58, 2.11) * mm});
            skLineSegment(sketch, "E1512", {"start": v(-102.58, 2.11) * mm, "end": v(-102.55, 1.75) * mm});
            skLineSegment(sketch, "E1513", {"start": v(-102.55, 1.75) * mm, "end": v(-102.51, 1.36) * mm});
            skLineSegment(sketch, "E1514", {"start": v(-102.51, 1.36) * mm, "end": v(-102.48, 0.95) * mm});
            skLineSegment(sketch, "E1515", {"start": v(-102.48, 0.95) * mm, "end": v(-102.46, 0.51) * mm});
            skLineSegment(sketch, "E1516", {"start": v(-102.46, 0.51) * mm, "end": v(-102.43, 0.05) * mm});
            skLineSegment(sketch, "E1517", {"start": v(-102.43, 0.05) * mm, "end": v(-102.41, -0.43) * mm});
            skLineSegment(sketch, "E1518", {"start": v(-102.41, -0.43) * mm, "end": v(-102.4, -0.94) * mm});
            skLineSegment(sketch, "E1519", {"start": v(-102.4, -0.94) * mm, "end": v(-102.38, -1.47) * mm});
            skLineSegment(sketch, "E1520", {"start": v(-102.38, -1.47) * mm, "end": v(-102.37, -2.02) * mm});
            skLineSegment(sketch, "E1521", {"start": v(-102.37, -2.02) * mm, "end": v(-102.36, -2.6) * mm});
            skLineSegment(sketch, "E1522", {"start": v(-102.36, -2.6) * mm, "end": v(-102.36, -3.2) * mm});
            skLineSegment(sketch, "E1523", {"start": v(-102.36, -3.2) * mm, "end": v(-102.35, -3.83) * mm});
            skLineSegment(sketch, "E1524", {"start": v(-102.35, -3.83) * mm, "end": v(-102.35, -30.56) * mm});
            skLineSegment(sketch, "E1525", {"start": v(-102.35, -30.56) * mm, "end": v(-109.72, -30.56) * mm});
            skLineSegment(sketch, "E1526", {"start": v(-109.72, -30.56) * mm, "end": v(-109.72, -4.12) * mm});
            skLineSegment(sketch, "E1527", {"start": v(-109.72, -4.12) * mm, "end": v(-109.73, -3.03) * mm});
            skLineSegment(sketch, "E1528", {"start": v(-109.73, -3.03) * mm, "end": v(-109.78, -2.01) * mm});
            skLineSegment(sketch, "E1529", {"start": v(-109.78, -2.01) * mm, "end": v(-109.84, -1.06) * mm});
            skLineSegment(sketch, "E1530", {"start": v(-109.84, -1.06) * mm, "end": v(-109.94, -0.19) * mm});
            skLineSegment(sketch, "E1531", {"start": v(-109.94, -0.19) * mm, "end": v(-110.06, 0.62) * mm});
            skLineSegment(sketch, "E1532", {"start": v(-110.06, 0.62) * mm, "end": v(-110.2, 1.35) * mm});
            skLineSegment(sketch, "E1533", {"start": v(-110.2, 1.35) * mm, "end": v(-110.38, 2.02) * mm});
            skLineSegment(sketch, "E1534", {"start": v(-110.38, 2.02) * mm, "end": v(-110.58, 2.61) * mm});
            skLineSegment(sketch, "E1535", {"start": v(-110.58, 2.61) * mm, "end": v(-110.82, 3.16) * mm});
            skLineSegment(sketch, "E1536", {"start": v(-110.82, 3.16) * mm, "end": v(-111.1, 3.67) * mm});
            skLineSegment(sketch, "E1537", {"start": v(-111.1, 3.67) * mm, "end": v(-111.41, 4.16) * mm});
            skLineSegment(sketch, "E1538", {"start": v(-111.41, 4.16) * mm, "end": v(-111.77, 4.62) * mm});
            skLineSegment(sketch, "E1539", {"start": v(-111.77, 4.62) * mm, "end": v(-112.17, 5.05) * mm});
            skLineSegment(sketch, "E1540", {"start": v(-112.17, 5.05) * mm, "end": v(-112.62, 5.45) * mm});
            skLineSegment(sketch, "E1541", {"start": v(-112.62, 5.45) * mm, "end": v(-113.1, 5.83) * mm});
            skLineSegment(sketch, "E1542", {"start": v(-113.1, 5.83) * mm, "end": v(-113.63, 6.17) * mm});
            skLineSegment(sketch, "E1543", {"start": v(-113.63, 6.17) * mm, "end": v(-114.19, 6.48) * mm});
            skLineSegment(sketch, "E1544", {"start": v(-114.19, 6.48) * mm, "end": v(-114.77, 6.75) * mm});
            skLineSegment(sketch, "E1545", {"start": v(-114.77, 6.75) * mm, "end": v(-115.38, 6.98) * mm});
            skLineSegment(sketch, "E1546", {"start": v(-115.38, 6.98) * mm, "end": v(-116, 7.17) * mm});
            skLineSegment(sketch, "E1547", {"start": v(-116, 7.17) * mm, "end": v(-116.66, 7.32) * mm});
            skLineSegment(sketch, "E1548", {"start": v(-116.66, 7.32) * mm, "end": v(-117.34, 7.42) * mm});
            skLineSegment(sketch, "E1549", {"start": v(-117.34, 7.42) * mm, "end": v(-118.04, 7.48) * mm});
            skLineSegment(sketch, "E1550", {"start": v(-118.04, 7.48) * mm, "end": v(-118.77, 7.5) * mm});
            skLineSegment(sketch, "E1551", {"start": v(-118.77, 7.5) * mm, "end": v(-119.35, 7.5) * mm});
            skLineSegment(sketch, "E1552", {"start": v(-119.35, 7.5) * mm, "end": v(-119.92, 7.46) * mm});
            skLineSegment(sketch, "E1553", {"start": v(-119.92, 7.46) * mm, "end": v(-120.49, 7.4) * mm});
            skLineSegment(sketch, "E1554", {"start": v(-120.49, 7.4) * mm, "end": v(-121.04, 7.32) * mm});
            skLineSegment(sketch, "E1555", {"start": v(-121.04, 7.32) * mm, "end": v(-121.58, 7.21) * mm});
            skLineSegment(sketch, "E1556", {"start": v(-121.58, 7.21) * mm, "end": v(-122.12, 7.08) * mm});
            skLineSegment(sketch, "E1557", {"start": v(-122.12, 7.08) * mm, "end": v(-122.64, 6.93) * mm});
            skLineSegment(sketch, "E1558", {"start": v(-122.64, 6.93) * mm, "end": v(-123.15, 6.76) * mm});
            skLineSegment(sketch, "E1559", {"start": v(-123.15, 6.76) * mm, "end": v(-123.65, 6.56) * mm});
            skLineSegment(sketch, "E1560", {"start": v(-123.65, 6.56) * mm, "end": v(-124.15, 6.34) * mm});
            skLineSegment(sketch, "E1561", {"start": v(-124.15, 6.34) * mm, "end": v(-124.63, 6.1) * mm});
            skLineSegment(sketch, "E1562", {"start": v(-124.63, 6.1) * mm, "end": v(-125.1, 5.82) * mm});
            skLineSegment(sketch, "E1563", {"start": v(-125.1, 5.82) * mm, "end": v(-125.56, 5.53) * mm});
            skLineSegment(sketch, "E1564", {"start": v(-125.56, 5.53) * mm, "end": v(-126.02, 5.22) * mm});
            skLineSegment(sketch, "E1565", {"start": v(-126.02, 5.22) * mm, "end": v(-126.46, 4.88) * mm});
            skLineSegment(sketch, "E1566", {"start": v(-126.46, 4.88) * mm, "end": v(-126.9, 4.52) * mm});
            skLineSegment(sketch, "E1567", {"start": v(-126.9, 4.52) * mm, "end": v(-127.3, 4.12) * mm});
            skLineSegment(sketch, "E1568", {"start": v(-127.3, 4.12) * mm, "end": v(-127.7, 3.68) * mm});
            skLineSegment(sketch, "E1569", {"start": v(-127.7, 3.68) * mm, "end": v(-128.05, 3.2) * mm});
            skLineSegment(sketch, "E1570", {"start": v(-128.05, 3.2) * mm, "end": v(-128.39, 2.69) * mm});
            skLineSegment(sketch, "E1571", {"start": v(-128.39, 2.69) * mm, "end": v(-128.7, 2.12) * mm});
            skLineSegment(sketch, "E1572", {"start": v(-128.7, 2.12) * mm, "end": v(-128.97, 1.52) * mm});
            skLineSegment(sketch, "E1573", {"start": v(-128.97, 1.52) * mm, "end": v(-129.23, 0.87) * mm});
            skLineSegment(sketch, "E1574", {"start": v(-129.23, 0.87) * mm, "end": v(-129.45, 0.19) * mm});
            skLineSegment(sketch, "E1575", {"start": v(-129.45, 0.19) * mm, "end": v(-129.65, -0.54) * mm});
            skLineSegment(sketch, "E1576", {"start": v(-129.65, -0.54) * mm, "end": v(-129.83, -1.31) * mm});
            skLineSegment(sketch, "E1577", {"start": v(-129.83, -1.31) * mm, "end": v(-129.97, -2.13) * mm});
            skLineSegment(sketch, "E1578", {"start": v(-129.97, -2.13) * mm, "end": v(-130.1, -2.98) * mm});
            skLineSegment(sketch, "E1579", {"start": v(-130.1, -2.98) * mm, "end": v(-130.19, -3.88) * mm});
            skLineSegment(sketch, "E1580", {"start": v(-130.19, -3.88) * mm, "end": v(-130.25, -4.82) * mm});
            skLineSegment(sketch, "E1581", {"start": v(-130.25, -4.82) * mm, "end": v(-130.3, -5.8) * mm});
            skLineSegment(sketch, "E1582", {"start": v(-130.3, -5.8) * mm, "end": v(-130.3, -6.82) * mm});
            skLineSegment(sketch, "E1583", {"start": v(-130.3, -6.82) * mm, "end": v(-130.3, -30.56) * mm});
            skLineSegment(sketch, "E1584", {"start": v(-148.89, 20.97) * mm, "end": v(-156.26, 20.97) * mm});
            skLineSegment(sketch, "E1585", {"start": v(-156.26, 20.97) * mm, "end": v(-156.26, 29.44) * mm});
            skLineSegment(sketch, "E1586", {"start": v(-156.26, 29.44) * mm, "end": v(-148.89, 29.44) * mm});
            skLineSegment(sketch, "E1587", {"start": v(-148.89, 29.44) * mm, "end": v(-148.89, 20.97) * mm});
            skLineSegment(sketch, "E1588", {"start": v(-148.89, -30.56) * mm, "end": v(-156.26, -30.56) * mm});
            skLineSegment(sketch, "E1589", {"start": v(-156.26, -30.56) * mm, "end": v(-156.26, 12.9) * mm});
            skLineSegment(sketch, "E1590", {"start": v(-156.26, 12.9) * mm, "end": v(-148.89, 12.9) * mm});
            skLineSegment(sketch, "E1591", {"start": v(-148.89, 12.9) * mm, "end": v(-148.89, -30.56) * mm});
            skLineSegment(sketch, "E1592", {"start": v(-207.7, -30.56) * mm, "end": v(-215.64, -30.56) * mm});
            skLineSegment(sketch, "E1593", {"start": v(-215.64, -30.56) * mm, "end": v(-215.64, 29.44) * mm});
            skLineSegment(sketch, "E1594", {"start": v(-215.64, 29.44) * mm, "end": v(-207.7, 29.44) * mm});
            skLineSegment(sketch, "E1595", {"start": v(-207.7, 29.44) * mm, "end": v(-207.7, 4.8) * mm});
            skLineSegment(sketch, "E1596", {"start": v(-207.7, 4.8) * mm, "end": v(-176.52, 4.8) * mm});
            skLineSegment(sketch, "E1597", {"start": v(-176.52, 4.8) * mm, "end": v(-176.52, 29.44) * mm});
            skLineSegment(sketch, "E1598", {"start": v(-176.52, 29.44) * mm, "end": v(-168.58, 29.44) * mm});
            skLineSegment(sketch, "E1599", {"start": v(-168.58, 29.44) * mm, "end": v(-168.58, -30.56) * mm});
            skLineSegment(sketch, "E1600", {"start": v(-168.58, -30.56) * mm, "end": v(-176.52, -30.56) * mm});
            skLineSegment(sketch, "E1601", {"start": v(-176.52, -30.56) * mm, "end": v(-176.52, -2.28) * mm});
            skLineSegment(sketch, "E1602", {"start": v(-176.52, -2.28) * mm, "end": v(-207.7, -2.28) * mm});
            skLineSegment(sketch, "E1603", {"start": v(-207.7, -2.28) * mm, "end": v(-207.7, -30.56) * mm});
            skSolve(sketch);
        }
        {
            var Q0;
            Q0=makeQuery(id+"F0.imprint","IMPRINT",FACE,{"disambiguationData":[TD([[makeQuery(id+"F0.imprint","IMPRINT",EDGE,{"derivedFrom":sQuery(id+"F0.wireOp",EDGE,"E0")}),-1.0]])]});
            extrude(context, id + "F1", {"entities" : qUnion([Q0]), "depth" : 3 * mm});
        }
    });
